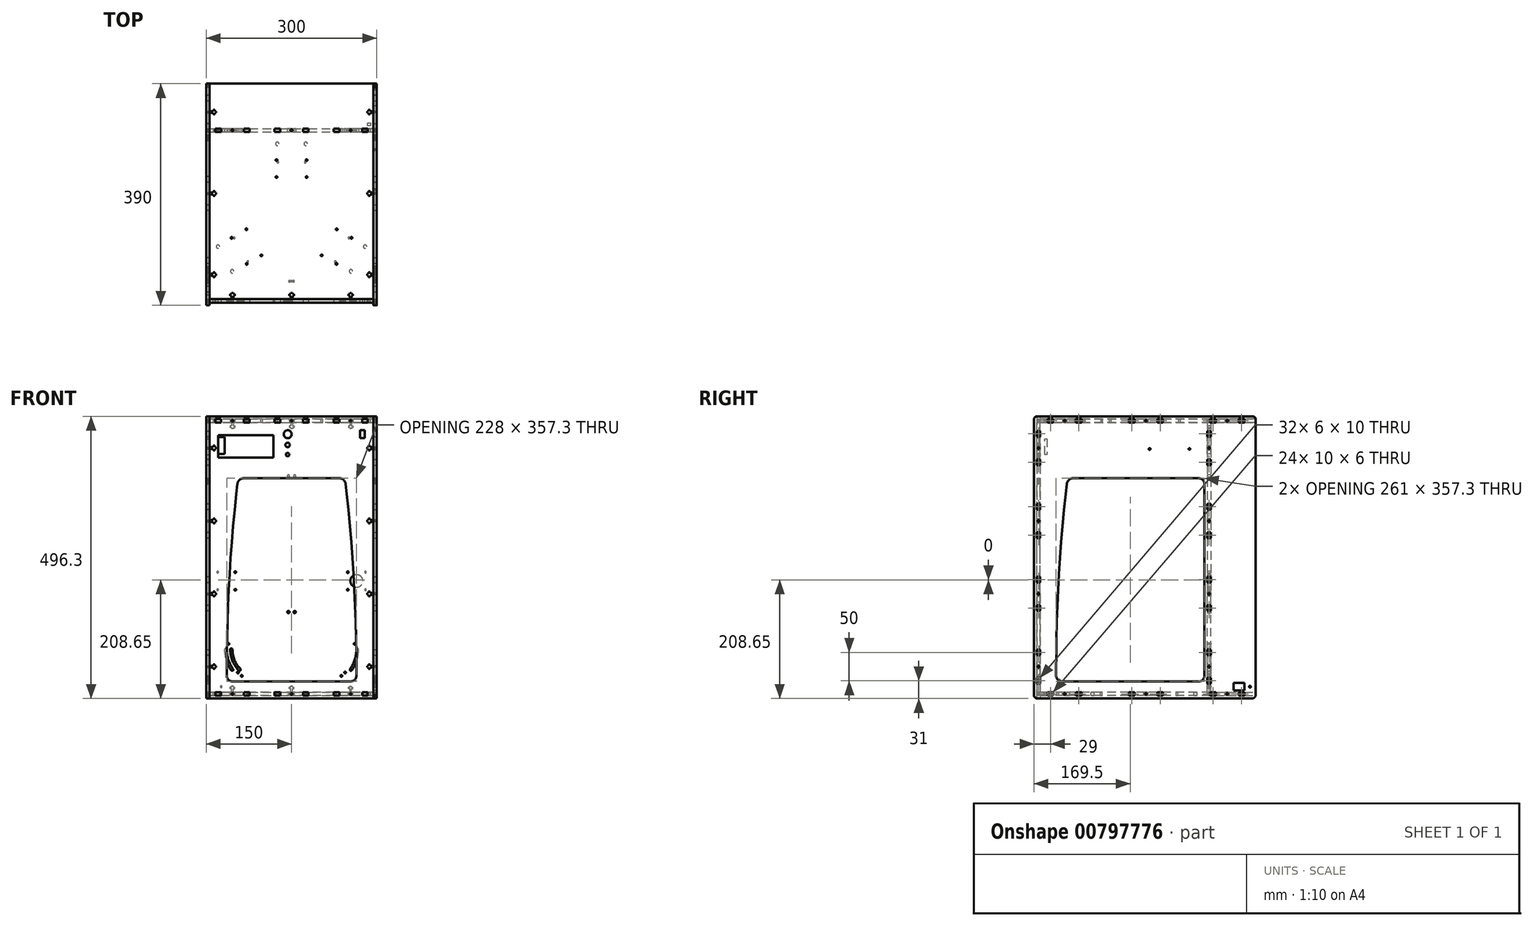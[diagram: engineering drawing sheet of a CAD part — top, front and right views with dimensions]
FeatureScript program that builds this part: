
annotation { "Feature Type Name" : "Feature", "Feature Type Description" : "" }
export const myFeature = defineFeature(function(context is Context, id is Id, definition is map)
    precondition{}
    {
        {
            var Q0;
            Q0=qCreatedBy(makeId("Top.planeOp"),FACE);
            cPlane(context, id + "F0", {"entities" : qUnion([Q0]), "cplaneType" : CPlaneType.OFFSET, "offset" : 237.15 * mm, "width" : 150 * mm, "height" : 150 * mm});
        }
        {
            var Q0;
            Q0=qCreatedBy(makeId("Top.planeOp"),FACE);
            cPlane(context, id + "F1", {"entities" : qUnion([Q0]), "cplaneType" : CPlaneType.OFFSET, "offset" : 237.15 * mm, "oppositeDirection" : true, "width" : 150 * mm, "height" : 150 * mm});
        }
        {
            var Q0;
            Q0=qCreatedBy(id+"F0.planeOp",FACE);
            var sketch = newSketch(context, id + "F2", { "sketchPlane" : qUnion([Q0])});
            skLineSegment(sketch, "E0", {"start": v(-144, 159.5) * mm, "end": v(-150, 159.5) * mm});
            skLineSegment(sketch, "E1", {"start": v(84, 104.5) * mm, "end": v(74, 104.5) * mm});
            skCircle(sketch, "E2", {"center": v(-105.48, -81.65) * mm, "radius": 1.5 * mm});
            skCircle(sketch, "E3", {"center": v(-104, 107.5) * mm, "radius": 1.5 * mm});
            skLineSegment(sketch, "E4", {"start": v(-138, 141) * mm, "end": v(-138, 143.5) * mm});
            skLineSegment(sketch, "E5", {"start": v(-150, 109.5) * mm, "end": v(-150, 119.5) * mm});
            skLineSegment(sketch, "E6", {"start": v(-144, 109.5) * mm, "end": v(-150, 109.5) * mm});
            skLineSegment(sketch, "E7", {"start": v(-144, 119.5) * mm, "end": v(-150, 119.5) * mm});
            skCircle(sketch, "E8", {"center": v(0, 107.5) * mm, "radius": 1.5 * mm});
            skCircle(sketch, "E9", {"center": v(104, 107.5) * mm, "radius": 1.5 * mm});
            skLineSegment(sketch, "E10", {"start": v(-105.5, -189.5) * mm, "end": v(-124, -189.5) * mm});
            skLineSegment(sketch, "E11", {"start": v(-144, -189.5) * mm, "end": v(-144, -176.5) * mm});
            skLineSegment(sketch, "E12", {"start": v(-135, -148) * mm, "end": v(-133, -148) * mm});
            skLineSegment(sketch, "E13", {"start": v(-135, -145) * mm, "end": v(-133, -145) * mm});
            skLineSegment(sketch, "E14", {"start": v(-135, -5) * mm, "end": v(-133, -5) * mm});
            skLineSegment(sketch, "E15", {"start": v(-135, -2) * mm, "end": v(-133, -2) * mm});
            skLineSegment(sketch, "E16", {"start": v(-135, 138) * mm, "end": v(-133, 138) * mm});
            skLineSegment(sketch, "E17", {"start": v(-135, 141) * mm, "end": v(-133, 141) * mm});
            skLineSegment(sketch, "E18", {"start": v(144, 141) * mm, "end": v(138, 141) * mm});
            skLineSegment(sketch, "E19", {"start": v(144, 138) * mm, "end": v(138, 138) * mm});
            skLineSegment(sketch, "E20", {"start": v(144, -2) * mm, "end": v(138, -2) * mm});
            skLineSegment(sketch, "E21", {"start": v(144, -5) * mm, "end": v(138, -5) * mm});
            skLineSegment(sketch, "E22", {"start": v(144, -33.5) * mm, "end": v(144, -116.5) * mm});
            skLineSegment(sketch, "E23", {"start": v(144, -145) * mm, "end": v(138, -145) * mm});
            skLineSegment(sketch, "E24", {"start": v(144, -148) * mm, "end": v(138, -148) * mm});
            skLineSegment(sketch, "E25", {"start": v(-74, -189.5) * mm, "end": v(-74, -195.5) * mm});
            skLineSegment(sketch, "E26", {"start": v(102.5, -180.5) * mm, "end": v(100, -180.5) * mm});
            skLineSegment(sketch, "E27", {"start": v(102.5, -180.5) * mm, "end": v(102.5, -178.5) * mm});
            skLineSegment(sketch, "E28", {"start": v(-105.5, -183.5) * mm, "end": v(-108, -183.5) * mm});
            skLineSegment(sketch, "E29", {"start": v(144, 159.5) * mm, "end": v(144, 141) * mm});
            skLineSegment(sketch, "E30", {"start": v(135, -5) * mm, "end": v(133, -5) * mm});
            skLineSegment(sketch, "E31", {"start": v(-138, -5) * mm, "end": v(-138, -7.5) * mm});
            skLineSegment(sketch, "E32", {"start": v(134, -189.5) * mm, "end": v(134, -195.5) * mm});
            skLineSegment(sketch, "E33", {"start": v(-105.5, -180.5) * mm, "end": v(-108, -180.5) * mm});
            skLineSegment(sketch, "E34", {"start": v(-102.5, -180.5) * mm, "end": v(-100, -180.5) * mm});
            skLineSegment(sketch, "E35", {"start": v(-1.5, -189.5) * mm, "end": v(-20, -189.5) * mm});
            skLineSegment(sketch, "E36", {"start": v(134, 110.5) * mm, "end": v(134, 104.5) * mm});
            skLineSegment(sketch, "E37", {"start": v(-74, 104.5) * mm, "end": v(-74, 110.5) * mm});
            skLineSegment(sketch, "E38", {"start": v(74, 110.5) * mm, "end": v(84, 110.5) * mm});
            skLineSegment(sketch, "E39", {"start": v(144, -33.5) * mm, "end": v(150, -33.5) * mm});
            skLineSegment(sketch, "E40", {"start": v(144, 16.5) * mm, "end": v(144, -2) * mm});
            skLineSegment(sketch, "E41", {"start": v(150, 109.5) * mm, "end": v(150, 119.5) * mm});
            skLineSegment(sketch, "E42", {"start": v(135, 138) * mm, "end": v(133, 138) * mm});
            skLineSegment(sketch, "E43", {"start": v(144, -116.5) * mm, "end": v(150, -116.5) * mm});
            skLineSegment(sketch, "E44", {"start": v(144, 119.5) * mm, "end": v(150, 119.5) * mm});
            skLineSegment(sketch, "E45", {"start": v(144, -176.5) * mm, "end": v(150, -176.5) * mm});
            skLineSegment(sketch, "E46", {"start": v(138, -145) * mm, "end": v(138, -142.5) * mm});
            skLineSegment(sketch, "E47", {"start": v(144, 189.5) * mm, "end": v(144, 169.5) * mm});
            skLineSegment(sketch, "E48", {"start": v(135, -145) * mm, "end": v(135, -142.5) * mm});
            skLineSegment(sketch, "E49", {"start": v(133, -145) * mm, "end": v(133, -148) * mm});
            skLineSegment(sketch, "E50", {"start": v(135, 138) * mm, "end": v(135, 135.5) * mm});
            skLineSegment(sketch, "E51", {"start": v(138, -142.5) * mm, "end": v(135, -142.5) * mm});
            skLineSegment(sketch, "E52", {"start": v(150, -126.5) * mm, "end": v(150, -116.5) * mm});
            skLineSegment(sketch, "E53", {"start": v(138, 141) * mm, "end": v(138, 143.5) * mm});
            skLineSegment(sketch, "E54", {"start": v(144, -126.5) * mm, "end": v(144, -145) * mm});
            skLineSegment(sketch, "E55", {"start": v(144, 138) * mm, "end": v(144, 119.5) * mm});
            skLineSegment(sketch, "E56", {"start": v(150, 159.5) * mm, "end": v(150, 169.5) * mm});
            skLineSegment(sketch, "E57", {"start": v(135, -148) * mm, "end": v(133, -148) * mm});
            skLineSegment(sketch, "E58", {"start": v(135, -148) * mm, "end": v(135, -150.5) * mm});
            skLineSegment(sketch, "E59", {"start": v(138, 138) * mm, "end": v(138, 135.5) * mm});
            skLineSegment(sketch, "E60", {"start": v(144, 169.5) * mm, "end": v(150, 169.5) * mm});
            skLineSegment(sketch, "E61", {"start": v(144, 109.5) * mm, "end": v(144, 26.5) * mm});
            skLineSegment(sketch, "E62", {"start": v(138, -148) * mm, "end": v(138, -150.5) * mm});
            skLineSegment(sketch, "E63", {"start": v(-133, -2) * mm, "end": v(-133, -5) * mm});
            skLineSegment(sketch, "E64", {"start": v(144, -176.5) * mm, "end": v(144, -189.5) * mm});
            skLineSegment(sketch, "E65", {"start": v(144, -189.5) * mm, "end": v(134, -189.5) * mm});
            skLineSegment(sketch, "E66", {"start": v(105.5, -189.5) * mm, "end": v(105.5, -183.5) * mm});
            skLineSegment(sketch, "E67", {"start": v(105.5, -183.5) * mm, "end": v(108, -183.5) * mm});
            skLineSegment(sketch, "E68", {"start": v(108, -183.5) * mm, "end": v(108, -180.5) * mm});
            skLineSegment(sketch, "E69", {"start": v(100, -183.5) * mm, "end": v(100, -180.5) * mm});
            skLineSegment(sketch, "E70", {"start": v(102.5, -183.5) * mm, "end": v(100, -183.5) * mm});
            skLineSegment(sketch, "E71", {"start": v(102.5, -189.5) * mm, "end": v(102.5, -183.5) * mm});
            skLineSegment(sketch, "E72", {"start": v(74, -189.5) * mm, "end": v(30, -189.5) * mm});
            skLineSegment(sketch, "E73", {"start": v(-134, -189.5) * mm, "end": v(-144, -189.5) * mm});
            skLineSegment(sketch, "E74", {"start": v(-84, -189.5) * mm, "end": v(-102.5, -189.5) * mm});
            skLineSegment(sketch, "E75", {"start": v(124, -195.5) * mm, "end": v(134, -195.5) * mm});
            skLineSegment(sketch, "E76", {"start": v(-102.5, -180.5) * mm, "end": v(-102.5, -178.5) * mm});
            skLineSegment(sketch, "E77", {"start": v(-144, -5) * mm, "end": v(-138, -5) * mm});
            skLineSegment(sketch, "E78", {"start": v(-150, -166.5) * mm, "end": v(-150, -176.5) * mm});
            skLineSegment(sketch, "E79", {"start": v(-144, -166.5) * mm, "end": v(-144, -148) * mm});
            skLineSegment(sketch, "E80", {"start": v(-138, 135.5) * mm, "end": v(-135, 135.5) * mm});
            skLineSegment(sketch, "E81", {"start": v(-144, -148) * mm, "end": v(-138, -148) * mm});
            skLineSegment(sketch, "E82", {"start": v(-144, -2) * mm, "end": v(-144, 16.5) * mm});
            skLineSegment(sketch, "E83", {"start": v(-150, 26.5) * mm, "end": v(-150, 16.5) * mm});
            skLineSegment(sketch, "E84", {"start": v(135, -145) * mm, "end": v(133, -145) * mm});
            skLineSegment(sketch, "E85", {"start": v(-135, -2) * mm, "end": v(-135, 0.5) * mm});
            skLineSegment(sketch, "E86", {"start": v(-144, -23.5) * mm, "end": v(-144, -5) * mm});
            skLineSegment(sketch, "E87", {"start": v(-150, -116.5) * mm, "end": v(-150, -126.5) * mm});
            skLineSegment(sketch, "E88", {"start": v(144, 26.5) * mm, "end": v(150, 26.5) * mm});
            skLineSegment(sketch, "E89", {"start": v(-138, -148) * mm, "end": v(-138, -150.5) * mm});
            skLineSegment(sketch, "E90", {"start": v(-133, 138) * mm, "end": v(-133, 141) * mm});
            skLineSegment(sketch, "E91", {"start": v(144, 16.5) * mm, "end": v(150, 16.5) * mm});
            skLineSegment(sketch, "E92", {"start": v(-102.5, -178.5) * mm, "end": v(-105.5, -178.5) * mm});
            skLineSegment(sketch, "E93", {"start": v(-102.5, -183.5) * mm, "end": v(-100, -183.5) * mm});
            skLineSegment(sketch, "E94", {"start": v(105.5, -178.5) * mm, "end": v(102.5, -178.5) * mm});
            skLineSegment(sketch, "E95", {"start": v(84, -189.5) * mm, "end": v(84, -195.5) * mm});
            skLineSegment(sketch, "E96", {"start": v(105.5, -180.5) * mm, "end": v(105.5, -178.5) * mm});
            skLineSegment(sketch, "E97", {"start": v(135, 141) * mm, "end": v(135, 143.5) * mm});
            skLineSegment(sketch, "E98", {"start": v(144, 109.5) * mm, "end": v(150, 109.5) * mm});
            skLineSegment(sketch, "E99", {"start": v(150, -176.5) * mm, "end": v(150, -166.5) * mm});
            skLineSegment(sketch, "E100", {"start": v(144, -166.5) * mm, "end": v(150, -166.5) * mm});
            skLineSegment(sketch, "E101", {"start": v(144, 159.5) * mm, "end": v(150, 159.5) * mm});
            skLineSegment(sketch, "E102", {"start": v(138, 143.5) * mm, "end": v(135, 143.5) * mm});
            skLineSegment(sketch, "E103", {"start": v(135, 141) * mm, "end": v(133, 141) * mm});
            skLineSegment(sketch, "E104", {"start": v(-133, -148) * mm, "end": v(-133, -145) * mm});
            skLineSegment(sketch, "E105", {"start": v(144, -148) * mm, "end": v(144, -166.5) * mm});
            skLineSegment(sketch, "E106", {"start": v(144, -126.5) * mm, "end": v(150, -126.5) * mm});
            skLineSegment(sketch, "E107", {"start": v(-144, -145) * mm, "end": v(-144, -126.5) * mm});
            skLineSegment(sketch, "E108", {"start": v(-144, -145) * mm, "end": v(-138, -145) * mm});
            skLineSegment(sketch, "E109", {"start": v(150, -33.5) * mm, "end": v(150, -23.5) * mm});
            skLineSegment(sketch, "E110", {"start": v(-135, 141) * mm, "end": v(-135, 143.5) * mm});
            skLineSegment(sketch, "E111", {"start": v(-144, 169.5) * mm, "end": v(-150, 169.5) * mm});
            skLineSegment(sketch, "E112", {"start": v(-144, 141) * mm, "end": v(-138, 141) * mm});
            skLineSegment(sketch, "E113", {"start": v(-20, 104.5) * mm, "end": v(-30, 104.5) * mm});
            skLineSegment(sketch, "E114", {"start": v(-84, 104.5) * mm, "end": v(-74, 104.5) * mm});
            skLineSegment(sketch, "E115", {"start": v(-134, 104.5) * mm, "end": v(-134, 110.5) * mm});
            skLineSegment(sketch, "E116", {"start": v(30, 110.5) * mm, "end": v(30, 104.5) * mm});
            skLineSegment(sketch, "E117", {"start": v(-135, -145) * mm, "end": v(-135, -142.5) * mm});
            skLineSegment(sketch, "E118", {"start": v(-138, -142.5) * mm, "end": v(-135, -142.5) * mm});
            skLineSegment(sketch, "E119", {"start": v(-134, 110.5) * mm, "end": v(-124, 110.5) * mm});
            skLineSegment(sketch, "E120", {"start": v(144, -23.5) * mm, "end": v(150, -23.5) * mm});
            skLineSegment(sketch, "E121", {"start": v(-138, -7.5) * mm, "end": v(-135, -7.5) * mm});
            skLineSegment(sketch, "E122", {"start": v(-144, -116.5) * mm, "end": v(-150, -116.5) * mm});
            skLineSegment(sketch, "E123", {"start": v(-135, -5) * mm, "end": v(-135, -7.5) * mm});
            skLineSegment(sketch, "E124", {"start": v(-144, -116.5) * mm, "end": v(-144, -33.5) * mm});
            skLineSegment(sketch, "E125", {"start": v(-150, -23.5) * mm, "end": v(-150, -33.5) * mm});
            skLineSegment(sketch, "E126", {"start": v(-124, -195.5) * mm, "end": v(-124, -189.5) * mm});
            skLineSegment(sketch, "E127", {"start": v(-84, -195.5) * mm, "end": v(-74, -195.5) * mm});
            skLineSegment(sketch, "E128", {"start": v(102.5, -189.5) * mm, "end": v(84, -189.5) * mm});
            skLineSegment(sketch, "E129", {"start": v(124, -189.5) * mm, "end": v(105.5, -189.5) * mm});
            skLineSegment(sketch, "E130", {"start": v(-105.5, -180.5) * mm, "end": v(-105.5, -178.5) * mm});
            skLineSegment(sketch, "E131", {"start": v(133, 141) * mm, "end": v(133, 138) * mm});
            skLineSegment(sketch, "E132", {"start": v(138, 135.5) * mm, "end": v(135, 135.5) * mm});
            skLineSegment(sketch, "E133", {"start": v(-1.5, -189.5) * mm, "end": v(-1.5, -183.5) * mm});
            skLineSegment(sketch, "E134", {"start": v(4, -183.5) * mm, "end": v(4, -180.5) * mm});
            skLineSegment(sketch, "E135", {"start": v(-1.5, -183.5) * mm, "end": v(-4, -183.5) * mm});
            skLineSegment(sketch, "E136", {"start": v(20, -189.5) * mm, "end": v(20, -195.5) * mm});
            skLineSegment(sketch, "E137", {"start": v(1.5, -178.5) * mm, "end": v(-1.5, -178.5) * mm});
            skLineSegment(sketch, "E138", {"start": v(-30, -195.5) * mm, "end": v(-20, -195.5) * mm});
            skLineSegment(sketch, "E139", {"start": v(-1.5, -180.5) * mm, "end": v(-1.5, -178.5) * mm});
            skLineSegment(sketch, "E140", {"start": v(1.5, -189.5) * mm, "end": v(1.5, -183.5) * mm});
            skLineSegment(sketch, "E141", {"start": v(30, -189.5) * mm, "end": v(30, -195.5) * mm});
            skLineSegment(sketch, "E142", {"start": v(1.5, -180.5) * mm, "end": v(1.5, -178.5) * mm});
            skLineSegment(sketch, "E143", {"start": v(1.5, -180.5) * mm, "end": v(4, -180.5) * mm});
            skLineSegment(sketch, "E144", {"start": v(20, -195.5) * mm, "end": v(30, -195.5) * mm});
            skLineSegment(sketch, "E145", {"start": v(-4, -183.5) * mm, "end": v(-4, -180.5) * mm});
            skLineSegment(sketch, "E146", {"start": v(-20, -189.5) * mm, "end": v(-20, -195.5) * mm});
            skLineSegment(sketch, "E147", {"start": v(138, -2) * mm, "end": v(138, 0.5) * mm});
            skLineSegment(sketch, "E148", {"start": v(-144, 119.5) * mm, "end": v(-144, 138) * mm});
            skLineSegment(sketch, "E149", {"start": v(-144, 26.5) * mm, "end": v(-144, 109.5) * mm});
            skLineSegment(sketch, "E150", {"start": v(-138, 138) * mm, "end": v(-138, 135.5) * mm});
            skLineSegment(sketch, "E151", {"start": v(-138, -150.5) * mm, "end": v(-135, -150.5) * mm});
            skLineSegment(sketch, "E152", {"start": v(135, -5) * mm, "end": v(135, -7.5) * mm});
            skLineSegment(sketch, "E153", {"start": v(-144, -126.5) * mm, "end": v(-150, -126.5) * mm});
            skLineSegment(sketch, "E154", {"start": v(-30, -189.5) * mm, "end": v(-30, -195.5) * mm});
            skLineSegment(sketch, "E155", {"start": v(138, -150.5) * mm, "end": v(135, -150.5) * mm});
            skLineSegment(sketch, "E156", {"start": v(-138, 0.5) * mm, "end": v(-135, 0.5) * mm});
            skLineSegment(sketch, "E157", {"start": v(-102.5, -189.5) * mm, "end": v(-102.5, -183.5) * mm});
            skLineSegment(sketch, "E158", {"start": v(74, -195.5) * mm, "end": v(84, -195.5) * mm});
            skLineSegment(sketch, "E159", {"start": v(-100, -183.5) * mm, "end": v(-100, -180.5) * mm});
            skLineSegment(sketch, "E160", {"start": v(-150, 169.5) * mm, "end": v(-150, 159.5) * mm});
            skLineSegment(sketch, "E161", {"start": v(-135, 138) * mm, "end": v(-135, 135.5) * mm});
            skLineSegment(sketch, "E162", {"start": v(-144, 141) * mm, "end": v(-144, 159.5) * mm});
            skLineSegment(sketch, "E163", {"start": v(-144, 26.5) * mm, "end": v(-150, 26.5) * mm});
            skLineSegment(sketch, "E164", {"start": v(135, -2) * mm, "end": v(133, -2) * mm});
            skLineSegment(sketch, "E165", {"start": v(-144, 169.5) * mm, "end": v(-144, 189.5) * mm});
            skLineSegment(sketch, "E166", {"start": v(-144, 16.5) * mm, "end": v(-150, 16.5) * mm});
            skLineSegment(sketch, "E167", {"start": v(-135, -148) * mm, "end": v(-135, -150.5) * mm});
            skLineSegment(sketch, "E168", {"start": v(-138, -145) * mm, "end": v(-138, -142.5) * mm});
            skLineSegment(sketch, "E169", {"start": v(138, 0.5) * mm, "end": v(135, 0.5) * mm});
            skLineSegment(sketch, "E170", {"start": v(-144, -2) * mm, "end": v(-138, -2) * mm});
            skLineSegment(sketch, "E171", {"start": v(138, -7.5) * mm, "end": v(135, -7.5) * mm});
            skLineSegment(sketch, "E172", {"start": v(-144, -176.5) * mm, "end": v(-150, -176.5) * mm});
            skLineSegment(sketch, "E173", {"start": v(133, -2) * mm, "end": v(133, -5) * mm});
            skLineSegment(sketch, "E174", {"start": v(-134, -189.5) * mm, "end": v(-134, -195.5) * mm});
            skLineSegment(sketch, "E175", {"start": v(-144, 189.5) * mm, "end": v(144, 189.5) * mm});
            skLineSegment(sketch, "E176", {"start": v(-124, 110.5) * mm, "end": v(-124, 104.5) * mm});
            skLineSegment(sketch, "E177", {"start": v(-30, 110.5) * mm, "end": v(-20, 110.5) * mm});
            skLineSegment(sketch, "E178", {"start": v(20, 104.5) * mm, "end": v(30, 104.5) * mm});
            skLineSegment(sketch, "E179", {"start": v(74, 104.5) * mm, "end": v(74, 110.5) * mm});
            skLineSegment(sketch, "E180", {"start": v(134, 104.5) * mm, "end": v(124, 104.5) * mm});
            skLineSegment(sketch, "E181", {"start": v(-20, 110.5) * mm, "end": v(-20, 104.5) * mm});
            skLineSegment(sketch, "E182", {"start": v(-30, 104.5) * mm, "end": v(-30, 110.5) * mm});
            skLineSegment(sketch, "E183", {"start": v(-84, 110.5) * mm, "end": v(-84, 104.5) * mm});
            skLineSegment(sketch, "E184", {"start": v(-138, 143.5) * mm, "end": v(-135, 143.5) * mm});
            skLineSegment(sketch, "E185", {"start": v(-144, 138) * mm, "end": v(-138, 138) * mm});
            skLineSegment(sketch, "E186", {"start": v(144, -5) * mm, "end": v(144, -23.5) * mm});
            skLineSegment(sketch, "E187", {"start": v(-144, -166.5) * mm, "end": v(-150, -166.5) * mm});
            skLineSegment(sketch, "E188", {"start": v(138, -5) * mm, "end": v(138, -7.5) * mm});
            skLineSegment(sketch, "E189", {"start": v(135, -2) * mm, "end": v(135, 0.5) * mm});
            skLineSegment(sketch, "E190", {"start": v(-144, -23.5) * mm, "end": v(-150, -23.5) * mm});
            skLineSegment(sketch, "E191", {"start": v(150, 16.5) * mm, "end": v(150, 26.5) * mm});
            skLineSegment(sketch, "E192", {"start": v(-144, -33.5) * mm, "end": v(-150, -33.5) * mm});
            skLineSegment(sketch, "E193", {"start": v(-84, -189.5) * mm, "end": v(-84, -195.5) * mm});
            skLineSegment(sketch, "E194", {"start": v(74, -189.5) * mm, "end": v(74, -195.5) * mm});
            skLineSegment(sketch, "E195", {"start": v(105.5, -180.5) * mm, "end": v(108, -180.5) * mm});
            skLineSegment(sketch, "E196", {"start": v(-108, -183.5) * mm, "end": v(-108, -180.5) * mm});
            skLineSegment(sketch, "E197", {"start": v(124, -189.5) * mm, "end": v(124, -195.5) * mm});
            skLineSegment(sketch, "E198", {"start": v(-124, -195.5) * mm, "end": v(-134, -195.5) * mm});
            skLineSegment(sketch, "E199", {"start": v(-105.5, -189.5) * mm, "end": v(-105.5, -183.5) * mm});
            skLineSegment(sketch, "E200", {"start": v(20, 104.5) * mm, "end": v(20, 110.5) * mm});
            skLineSegment(sketch, "E201", {"start": v(20, 110.5) * mm, "end": v(30, 110.5) * mm});
            skLineSegment(sketch, "E202", {"start": v(-124, 104.5) * mm, "end": v(-134, 104.5) * mm});
            skLineSegment(sketch, "E203", {"start": v(124, 110.5) * mm, "end": v(134, 110.5) * mm});
            skLineSegment(sketch, "E204", {"start": v(84, 110.5) * mm, "end": v(84, 104.5) * mm});
            skLineSegment(sketch, "E205", {"start": v(-138, -2) * mm, "end": v(-138, 0.5) * mm});
            skLineSegment(sketch, "E206", {"start": v(1.5, -183.5) * mm, "end": v(4, -183.5) * mm});
            skLineSegment(sketch, "E207", {"start": v(-1.5, -180.5) * mm, "end": v(-4, -180.5) * mm});
            skLineSegment(sketch, "E208", {"start": v(20, -189.5) * mm, "end": v(1.5, -189.5) * mm});
            skLineSegment(sketch, "E209", {"start": v(-30, -189.5) * mm, "end": v(-74, -189.5) * mm});
            skLineSegment(sketch, "E210", {"start": v(124, 104.5) * mm, "end": v(124, 110.5) * mm});
            skLineSegment(sketch, "E211", {"start": v(-74, 110.5) * mm, "end": v(-84, 110.5) * mm});
            skCircle(sketch, "E212", {"center": v(-79.5, -66.65) * mm, "radius": 1.5 * mm});
            skCircle(sketch, "E213", {"center": v(-26.5, 55.15) * mm, "radius": 1.5 * mm});
            skCircle(sketch, "E214", {"center": v(-78.98, -127.55) * mm, "radius": 1.5 * mm});
            skCircle(sketch, "E215", {"center": v(-53, -112.55) * mm, "radius": 1.5 * mm});
            skCircle(sketch, "E216", {"center": v(-26.5, 25.15) * mm, "radius": 1.5 * mm});
            skCircle(sketch, "E217", {"center": v(26.5, 55.15) * mm, "radius": 1.5 * mm});
            skCircle(sketch, "E218", {"center": v(26.5, 25.15) * mm, "radius": 1.5 * mm});
            skCircle(sketch, "E219", {"center": v(105.48, -81.65) * mm, "radius": 1.5 * mm});
            skCircle(sketch, "E220", {"center": v(79.5, -66.65) * mm, "radius": 1.5 * mm});
            skCircle(sketch, "E221", {"center": v(53, -112.55) * mm, "radius": 1.5 * mm});
            skCircle(sketch, "E222", {"center": v(78.98, -127.55) * mm, "radius": 1.5 * mm});
            skLineSegment(sketch, "E223", {"start": v(0, 189.5) * mm, "end": v(0, -189.5) * mm, "construction": true});
            skSolve(sketch);
        }
        {
            var Q0;
            Q0 = qSketchRegion(id + "F2", true);
            extrude(context, id + "F3", {"entities" : qUnion([Q0]), "depth" : 6 * mm, "offsetDistance" : 25 * mm});
        }
        {
            var Q0;
            Q0=qCreatedBy(id+"F1.planeOp",FACE);
            var sketch = newSketch(context, id + "F4", { "sketchPlane" : qUnion([Q0])});
            skCircle(sketch, "E224", {"center": v(-129.41, -97.2) * mm, "radius": 3 * mm});
            skCircle(sketch, "E225", {"center": v(104.41, -140.5) * mm, "radius": 3 * mm});
            skLineSegment(sketch, "E226", {"start": v(134, -189.5) * mm, "end": v(144, -189.5) * mm});
            skCircle(sketch, "E227", {"center": v(0, 107.5) * mm, "radius": 1.5 * mm});
            skCircle(sketch, "E228", {"center": v(104, 107.5) * mm, "radius": 1.5 * mm});
            skCircle(sketch, "E229", {"center": v(-104.41, -140.5) * mm, "radius": 3 * mm});
            skLineSegment(sketch, "E230", {"start": v(84, 104.5) * mm, "end": v(74, 104.5) * mm});
            skLineSegment(sketch, "E231", {"start": v(84, 110.5) * mm, "end": v(84, 104.5) * mm});
            skLineSegment(sketch, "E232", {"start": v(124, 104.5) * mm, "end": v(134, 104.5) * mm});
            skLineSegment(sketch, "E233", {"start": v(-134, 104.5) * mm, "end": v(-124, 104.5) * mm});
            skLineSegment(sketch, "E234", {"start": v(-134, 110.5) * mm, "end": v(-134, 104.5) * mm});
            skLineSegment(sketch, "E235", {"start": v(134, 104.5) * mm, "end": v(134, 110.5) * mm});
            skLineSegment(sketch, "E236", {"start": v(-20, 104.5) * mm, "end": v(-20, 110.5) * mm});
            skLineSegment(sketch, "E237", {"start": v(-20, 110.5) * mm, "end": v(-30, 110.5) * mm});
            skLineSegment(sketch, "E238", {"start": v(74, 104.5) * mm, "end": v(74, 110.5) * mm});
            skLineSegment(sketch, "E239", {"start": v(-30, 110.5) * mm, "end": v(-30, 104.5) * mm});
            skLineSegment(sketch, "E240", {"start": v(134, 110.5) * mm, "end": v(124, 110.5) * mm});
            skLineSegment(sketch, "E241", {"start": v(124, 110.5) * mm, "end": v(124, 104.5) * mm});
            skLineSegment(sketch, "E242", {"start": v(74, 110.5) * mm, "end": v(84, 110.5) * mm});
            skLineSegment(sketch, "E243", {"start": v(-84, 110.5) * mm, "end": v(-84, 104.5) * mm});
            skLineSegment(sketch, "E244", {"start": v(-30, 104.5) * mm, "end": v(-20, 104.5) * mm});
            skLineSegment(sketch, "E245", {"start": v(-74, 110.5) * mm, "end": v(-84, 110.5) * mm});
            skLineSegment(sketch, "E246", {"start": v(-84, 104.5) * mm, "end": v(-74, 104.5) * mm});
            skLineSegment(sketch, "E247", {"start": v(-74, 104.5) * mm, "end": v(-74, 110.5) * mm});
            skLineSegment(sketch, "E248", {"start": v(-124, 104.5) * mm, "end": v(-124, 110.5) * mm});
            skCircle(sketch, "E249", {"center": v(129.41, -97.2) * mm, "radius": 3 * mm});
            skCircle(sketch, "E250", {"center": v(25, 83.65) * mm, "radius": 3 * mm});
            skLineSegment(sketch, "E251", {"start": v(-3.53, -156.55) * mm, "end": v(3.47, -156.55) * mm});
            skCircle(sketch, "E252", {"center": v(-25, 83.65) * mm, "radius": 3 * mm});
            skCircle(sketch, "E253", {"center": v(-104, 107.5) * mm, "radius": 1.5 * mm});
            skLineSegment(sketch, "E254", {"start": v(144, 189.5) * mm, "end": v(-144, 189.5) * mm});
            skArc(sketch, "E255", {"start": v(-3.53, -156.55) * mm, "mid": v(-5.03, -158.05) * mm, "end": v(-3.53, -159.55) * mm});
            skLineSegment(sketch, "E256", {"start": v(30, 104.5) * mm, "end": v(30, 110.5) * mm});
            skLineSegment(sketch, "E257", {"start": v(30, 110.5) * mm, "end": v(20, 110.5) * mm});
            skLineSegment(sketch, "E258", {"start": v(20, 104.5) * mm, "end": v(20, 110.5) * mm});
            skLineSegment(sketch, "E259", {"start": v(30, 104.5) * mm, "end": v(20, 104.5) * mm});
            skLineSegment(sketch, "E260", {"start": v(3.47, -159.55) * mm, "end": v(-3.53, -159.55) * mm});
            skLineSegment(sketch, "E261", {"start": v(144, 16.5) * mm, "end": v(150, 16.5) * mm});
            skLineSegment(sketch, "E262", {"start": v(144, 26.5) * mm, "end": v(150, 26.5) * mm});
            skLineSegment(sketch, "E263", {"start": v(144, -126.5) * mm, "end": v(150, -126.5) * mm});
            skLineSegment(sketch, "E264", {"start": v(144, -145) * mm, "end": v(138, -145) * mm});
            skLineSegment(sketch, "E265", {"start": v(138, -150.5) * mm, "end": v(135, -150.5) * mm});
            skLineSegment(sketch, "E266", {"start": v(135, -148) * mm, "end": v(133, -148) * mm});
            skLineSegment(sketch, "E267", {"start": v(138, -145) * mm, "end": v(138, -142.5) * mm});
            skLineSegment(sketch, "E268", {"start": v(138, -142.5) * mm, "end": v(135, -142.5) * mm});
            skLineSegment(sketch, "E269", {"start": v(150, -176.5) * mm, "end": v(150, -166.5) * mm});
            skLineSegment(sketch, "E270", {"start": v(144, -166.5) * mm, "end": v(150, -166.5) * mm});
            skLineSegment(sketch, "E271", {"start": v(135, -145) * mm, "end": v(133, -145) * mm});
            skLineSegment(sketch, "E272", {"start": v(144, -116.5) * mm, "end": v(150, -116.5) * mm});
            skLineSegment(sketch, "E273", {"start": v(138, -148) * mm, "end": v(138, -150.5) * mm});
            skLineSegment(sketch, "E274", {"start": v(144, -176.5) * mm, "end": v(150, -176.5) * mm});
            skArc(sketch, "E275", {"start": v(3.47, -159.55) * mm, "mid": v(4.97, -158.05) * mm, "end": v(3.47, -156.55) * mm});
            skLineSegment(sketch, "E276", {"start": v(134, 120.5) * mm, "end": v(139, 120.5) * mm});
            skLineSegment(sketch, "E277", {"start": v(134, 115.5) * mm, "end": v(134, 120.5) * mm});
            skLineSegment(sketch, "E278", {"start": v(139, 115.5) * mm, "end": v(134, 115.5) * mm});
            skLineSegment(sketch, "E279", {"start": v(139, 120.5) * mm, "end": v(139, 115.5) * mm});
            skLineSegment(sketch, "E280", {"start": v(-133, 141) * mm, "end": v(-133, 138) * mm});
            skLineSegment(sketch, "E281", {"start": v(-138, 141) * mm, "end": v(-138, 143.5) * mm});
            skLineSegment(sketch, "E282", {"start": v(-138, 138) * mm, "end": v(-138, 135.5) * mm});
            skLineSegment(sketch, "E283", {"start": v(-135, 141) * mm, "end": v(-135, 143.5) * mm});
            skLineSegment(sketch, "E284", {"start": v(-135, 141) * mm, "end": v(-133, 141) * mm});
            skLineSegment(sketch, "E285", {"start": v(-150, 169.5) * mm, "end": v(-150, 159.5) * mm});
            skLineSegment(sketch, "E286", {"start": v(-144, 109.5) * mm, "end": v(-150, 109.5) * mm});
            skLineSegment(sketch, "E287", {"start": v(-144, 169.5) * mm, "end": v(-144, 189.5) * mm});
            skLineSegment(sketch, "E288", {"start": v(-144, 138) * mm, "end": v(-138, 138) * mm});
            skLineSegment(sketch, "E289", {"start": v(-144, 141) * mm, "end": v(-138, 141) * mm});
            skLineSegment(sketch, "E290", {"start": v(-138, 143.5) * mm, "end": v(-135, 143.5) * mm});
            skLineSegment(sketch, "E291", {"start": v(-144, 169.5) * mm, "end": v(-150, 169.5) * mm});
            skLineSegment(sketch, "E292", {"start": v(-135, 138) * mm, "end": v(-135, 135.5) * mm});
            skLineSegment(sketch, "E293", {"start": v(-124, 110.5) * mm, "end": v(-134, 110.5) * mm});
            skLineSegment(sketch, "E294", {"start": v(102.5, -189.5) * mm, "end": v(102.5, -183.5) * mm});
            skLineSegment(sketch, "E295", {"start": v(124, -189.5) * mm, "end": v(124, -195.5) * mm});
            skLineSegment(sketch, "E296", {"start": v(105.5, -180.5) * mm, "end": v(108, -180.5) * mm});
            skLineSegment(sketch, "E297", {"start": v(124, -195.5) * mm, "end": v(134, -195.5) * mm});
            skLineSegment(sketch, "E298", {"start": v(105.5, -183.5) * mm, "end": v(108, -183.5) * mm});
            skLineSegment(sketch, "E299", {"start": v(84, -189.5) * mm, "end": v(84, -195.5) * mm});
            skLineSegment(sketch, "E300", {"start": v(134, -189.5) * mm, "end": v(134, -195.5) * mm});
            skLineSegment(sketch, "E301", {"start": v(105.5, -189.5) * mm, "end": v(105.5, -183.5) * mm});
            skLineSegment(sketch, "E302", {"start": v(105.5, -189.5) * mm, "end": v(124, -189.5) * mm});
            skLineSegment(sketch, "E303", {"start": v(108, -183.5) * mm, "end": v(108, -180.5) * mm});
            skLineSegment(sketch, "E304", {"start": v(84, -189.5) * mm, "end": v(102.5, -189.5) * mm});
            skLineSegment(sketch, "E305", {"start": v(74, -189.5) * mm, "end": v(74, -195.5) * mm});
            skLineSegment(sketch, "E306", {"start": v(105.5, -180.5) * mm, "end": v(105.5, -178.5) * mm});
            skLineSegment(sketch, "E307", {"start": v(102.5, -180.5) * mm, "end": v(102.5, -178.5) * mm});
            skLineSegment(sketch, "E308", {"start": v(105.5, -178.5) * mm, "end": v(102.5, -178.5) * mm});
            skLineSegment(sketch, "E309", {"start": v(102.5, -183.5) * mm, "end": v(100, -183.5) * mm});
            skLineSegment(sketch, "E310", {"start": v(-74, -189.5) * mm, "end": v(-30, -189.5) * mm});
            skLineSegment(sketch, "E311", {"start": v(-20, -189.5) * mm, "end": v(-20, -195.5) * mm});
            skLineSegment(sketch, "E312", {"start": v(30, -189.5) * mm, "end": v(30, -195.5) * mm});
            skLineSegment(sketch, "E313", {"start": v(-20, -189.5) * mm, "end": v(-1.5, -189.5) * mm});
            skLineSegment(sketch, "E314", {"start": v(144, 109.5) * mm, "end": v(144, 26.5) * mm});
            skLineSegment(sketch, "E315", {"start": v(144, 119.5) * mm, "end": v(144, 138) * mm});
            skLineSegment(sketch, "E316", {"start": v(144, 169.5) * mm, "end": v(144, 189.5) * mm});
            skLineSegment(sketch, "E317", {"start": v(144, 159.5) * mm, "end": v(150, 159.5) * mm});
            skLineSegment(sketch, "E318", {"start": v(144, 138) * mm, "end": v(138, 138) * mm});
            skLineSegment(sketch, "E319", {"start": v(138, 135.5) * mm, "end": v(135, 135.5) * mm});
            skLineSegment(sketch, "E320", {"start": v(135, 138) * mm, "end": v(135, 135.5) * mm});
            skLineSegment(sketch, "E321", {"start": v(144, 109.5) * mm, "end": v(150, 109.5) * mm});
            skLineSegment(sketch, "E322", {"start": v(144, 169.5) * mm, "end": v(150, 169.5) * mm});
            skLineSegment(sketch, "E323", {"start": v(135, 141) * mm, "end": v(135, 143.5) * mm});
            skLineSegment(sketch, "E324", {"start": v(133, 141) * mm, "end": v(133, 138) * mm});
            skLineSegment(sketch, "E325", {"start": v(150, 109.5) * mm, "end": v(150, 119.5) * mm});
            skLineSegment(sketch, "E326", {"start": v(135, 138) * mm, "end": v(133, 138) * mm});
            skLineSegment(sketch, "E327", {"start": v(138, 143.5) * mm, "end": v(135, 143.5) * mm});
            skLineSegment(sketch, "E328", {"start": v(138, 141) * mm, "end": v(138, 143.5) * mm});
            skLineSegment(sketch, "E329", {"start": v(150, 159.5) * mm, "end": v(150, 169.5) * mm});
            skLineSegment(sketch, "E330", {"start": v(144, 119.5) * mm, "end": v(150, 119.5) * mm});
            skLineSegment(sketch, "E331", {"start": v(144, 141) * mm, "end": v(138, 141) * mm});
            skLineSegment(sketch, "E332", {"start": v(135, 141) * mm, "end": v(133, 141) * mm});
            skLineSegment(sketch, "E333", {"start": v(138, 138) * mm, "end": v(138, 135.5) * mm});
            skLineSegment(sketch, "E334", {"start": v(144, 141) * mm, "end": v(144, 159.5) * mm});
            skLineSegment(sketch, "E335", {"start": v(-138, 135.5) * mm, "end": v(-135, 135.5) * mm});
            skLineSegment(sketch, "E336", {"start": v(-150, 119.5) * mm, "end": v(-150, 109.5) * mm});
            skLineSegment(sketch, "E337", {"start": v(-144, 159.5) * mm, "end": v(-150, 159.5) * mm});
            skLineSegment(sketch, "E338", {"start": v(-144, 119.5) * mm, "end": v(-144, 138) * mm});
            skLineSegment(sketch, "E339", {"start": v(-144, 119.5) * mm, "end": v(-150, 119.5) * mm});
            skLineSegment(sketch, "E340", {"start": v(-135, 138) * mm, "end": v(-133, 138) * mm});
            skLineSegment(sketch, "E341", {"start": v(-144, 141) * mm, "end": v(-144, 159.5) * mm});
            skLineSegment(sketch, "E342", {"start": v(-144, 109.5) * mm, "end": v(-144, 26.5) * mm});
            skLineSegment(sketch, "E343", {"start": v(-144, -189.5) * mm, "end": v(-134, -189.5) * mm});
            skLineSegment(sketch, "E344", {"start": v(-144, -176.5) * mm, "end": v(-144, -189.5) * mm});
            skLineSegment(sketch, "E345", {"start": v(144, -33.5) * mm, "end": v(144, -116.5) * mm});
            skLineSegment(sketch, "E346", {"start": v(144, -5) * mm, "end": v(138, -5) * mm});
            skLineSegment(sketch, "E347", {"start": v(133, -2) * mm, "end": v(133, -5) * mm});
            skLineSegment(sketch, "E348", {"start": v(144, -5) * mm, "end": v(144, -23.5) * mm});
            skLineSegment(sketch, "E349", {"start": v(138, -5) * mm, "end": v(138, -7.5) * mm});
            skLineSegment(sketch, "E350", {"start": v(135, -2) * mm, "end": v(135, 0.5) * mm});
            skLineSegment(sketch, "E351", {"start": v(138, 0.5) * mm, "end": v(135, 0.5) * mm});
            skLineSegment(sketch, "E352", {"start": v(144, -23.5) * mm, "end": v(150, -23.5) * mm});
            skLineSegment(sketch, "E353", {"start": v(138, -7.5) * mm, "end": v(135, -7.5) * mm});
            skLineSegment(sketch, "E354", {"start": v(135, -5) * mm, "end": v(135, -7.5) * mm});
            skLineSegment(sketch, "E355", {"start": v(144, 16.5) * mm, "end": v(144, -2) * mm});
            skLineSegment(sketch, "E356", {"start": v(135, -5) * mm, "end": v(133, -5) * mm});
            skLineSegment(sketch, "E357", {"start": v(144, -33.5) * mm, "end": v(150, -33.5) * mm});
            skLineSegment(sketch, "E358", {"start": v(138, -2) * mm, "end": v(138, 0.5) * mm});
            skLineSegment(sketch, "E359", {"start": v(150, -33.5) * mm, "end": v(150, -23.5) * mm});
            skLineSegment(sketch, "E360", {"start": v(150, 16.5) * mm, "end": v(150, 26.5) * mm});
            skLineSegment(sketch, "E361", {"start": v(135, -2) * mm, "end": v(133, -2) * mm});
            skLineSegment(sketch, "E362", {"start": v(144, -2) * mm, "end": v(138, -2) * mm});
            skCircle(sketch, "E363", {"center": v(24, 51.36) * mm, "radius": 1.5 * mm});
            skCircle(sketch, "E364", {"center": v(-24, 51.36) * mm, "radius": 1.5 * mm});
            skLineSegment(sketch, "E365", {"start": v(135, -145) * mm, "end": v(135, -142.5) * mm});
            skLineSegment(sketch, "E366", {"start": v(133, -145) * mm, "end": v(133, -148) * mm});
            skLineSegment(sketch, "E367", {"start": v(144, -148) * mm, "end": v(144, -166.5) * mm});
            skLineSegment(sketch, "E368", {"start": v(144, -148) * mm, "end": v(138, -148) * mm});
            skLineSegment(sketch, "E369", {"start": v(135, -148) * mm, "end": v(135, -150.5) * mm});
            skLineSegment(sketch, "E370", {"start": v(150, -126.5) * mm, "end": v(150, -116.5) * mm});
            skLineSegment(sketch, "E371", {"start": v(144, -126.5) * mm, "end": v(144, -145) * mm});
            skLineSegment(sketch, "E372", {"start": v(144, -176.5) * mm, "end": v(144, -189.5) * mm});
            skLineSegment(sketch, "E373", {"start": v(-138, -5) * mm, "end": v(-138, -7.5) * mm});
            skLineSegment(sketch, "E374", {"start": v(-138, -2) * mm, "end": v(-138, 0.5) * mm});
            skLineSegment(sketch, "E375", {"start": v(-135, -5) * mm, "end": v(-133, -5) * mm});
            skLineSegment(sketch, "E376", {"start": v(-150, 26.5) * mm, "end": v(-150, 16.5) * mm});
            skLineSegment(sketch, "E377", {"start": v(-150, -23.5) * mm, "end": v(-150, -33.5) * mm});
            skLineSegment(sketch, "E378", {"start": v(-144, 26.5) * mm, "end": v(-150, 26.5) * mm});
            skLineSegment(sketch, "E379", {"start": v(-135, -2) * mm, "end": v(-135, 0.5) * mm});
            skLineSegment(sketch, "E380", {"start": v(-135, -5) * mm, "end": v(-135, -7.5) * mm});
            skLineSegment(sketch, "E381", {"start": v(-144, -5) * mm, "end": v(-144, -23.5) * mm});
            skLineSegment(sketch, "E382", {"start": v(-144, -33.5) * mm, "end": v(-150, -33.5) * mm});
            skLineSegment(sketch, "E383", {"start": v(-144, -5) * mm, "end": v(-138, -5) * mm});
            skLineSegment(sketch, "E384", {"start": v(-144, -2) * mm, "end": v(-138, -2) * mm});
            skLineSegment(sketch, "E385", {"start": v(-133, -2) * mm, "end": v(-133, -5) * mm});
            skLineSegment(sketch, "E386", {"start": v(-144, 16.5) * mm, "end": v(-144, -2) * mm});
            skLineSegment(sketch, "E387", {"start": v(-144, 16.5) * mm, "end": v(-150, 16.5) * mm});
            skLineSegment(sketch, "E388", {"start": v(-138, 0.5) * mm, "end": v(-135, 0.5) * mm});
            skLineSegment(sketch, "E389", {"start": v(-135, -2) * mm, "end": v(-133, -2) * mm});
            skLineSegment(sketch, "E390", {"start": v(-144, -23.5) * mm, "end": v(-150, -23.5) * mm});
            skLineSegment(sketch, "E391", {"start": v(-138, -7.5) * mm, "end": v(-135, -7.5) * mm});
            skLineSegment(sketch, "E392", {"start": v(-144, -33.5) * mm, "end": v(-144, -116.5) * mm});
            skLineSegment(sketch, "E393", {"start": v(-144, -166.5) * mm, "end": v(-150, -166.5) * mm});
            skLineSegment(sketch, "E394", {"start": v(-150, -116.5) * mm, "end": v(-150, -126.5) * mm});
            skLineSegment(sketch, "E395", {"start": v(-138, -148) * mm, "end": v(-138, -150.5) * mm});
            skLineSegment(sketch, "E396", {"start": v(-135, -145) * mm, "end": v(-135, -142.5) * mm});
            skLineSegment(sketch, "E397", {"start": v(-144, -116.5) * mm, "end": v(-150, -116.5) * mm});
            skLineSegment(sketch, "E398", {"start": v(-138, -145) * mm, "end": v(-138, -142.5) * mm});
            skLineSegment(sketch, "E399", {"start": v(-150, -166.5) * mm, "end": v(-150, -176.5) * mm});
            skLineSegment(sketch, "E400", {"start": v(-144, -126.5) * mm, "end": v(-144, -145) * mm});
            skLineSegment(sketch, "E401", {"start": v(-144, -176.5) * mm, "end": v(-150, -176.5) * mm});
            skLineSegment(sketch, "E402", {"start": v(-135, -148) * mm, "end": v(-135, -150.5) * mm});
            skLineSegment(sketch, "E403", {"start": v(-144, -145) * mm, "end": v(-138, -145) * mm});
            skLineSegment(sketch, "E404", {"start": v(-144, -148) * mm, "end": v(-144, -166.5) * mm});
            skLineSegment(sketch, "E405", {"start": v(-133, -145) * mm, "end": v(-133, -148) * mm});
            skLineSegment(sketch, "E406", {"start": v(-144, -126.5) * mm, "end": v(-150, -126.5) * mm});
            skLineSegment(sketch, "E407", {"start": v(-138, -142.5) * mm, "end": v(-135, -142.5) * mm});
            skLineSegment(sketch, "E408", {"start": v(-138, -150.5) * mm, "end": v(-135, -150.5) * mm});
            skLineSegment(sketch, "E409", {"start": v(-144, -148) * mm, "end": v(-138, -148) * mm});
            skLineSegment(sketch, "E410", {"start": v(-135, -148) * mm, "end": v(-133, -148) * mm});
            skLineSegment(sketch, "E411", {"start": v(-135, -145) * mm, "end": v(-133, -145) * mm});
            skLineSegment(sketch, "E412", {"start": v(100, -183.5) * mm, "end": v(100, -180.5) * mm});
            skLineSegment(sketch, "E413", {"start": v(102.5, -180.5) * mm, "end": v(100, -180.5) * mm});
            skLineSegment(sketch, "E414", {"start": v(74, -195.5) * mm, "end": v(84, -195.5) * mm});
            skLineSegment(sketch, "E415", {"start": v(-1.5, -180.5) * mm, "end": v(-1.5, -178.5) * mm});
            skLineSegment(sketch, "E416", {"start": v(1.5, -189.5) * mm, "end": v(20, -189.5) * mm});
            skLineSegment(sketch, "E417", {"start": v(-1.5, -180.5) * mm, "end": v(-4, -180.5) * mm});
            skLineSegment(sketch, "E418", {"start": v(4, -183.5) * mm, "end": v(4, -180.5) * mm});
            skLineSegment(sketch, "E419", {"start": v(-1.5, -183.5) * mm, "end": v(-4, -183.5) * mm});
            skLineSegment(sketch, "E420", {"start": v(20, -195.5) * mm, "end": v(30, -195.5) * mm});
            skLineSegment(sketch, "E421", {"start": v(-30, -195.5) * mm, "end": v(-20, -195.5) * mm});
            skLineSegment(sketch, "E422", {"start": v(1.5, -180.5) * mm, "end": v(4, -180.5) * mm});
            skLineSegment(sketch, "E423", {"start": v(20, -189.5) * mm, "end": v(20, -195.5) * mm});
            skLineSegment(sketch, "E424", {"start": v(1.5, -183.5) * mm, "end": v(4, -183.5) * mm});
            skLineSegment(sketch, "E425", {"start": v(-30, -189.5) * mm, "end": v(-30, -195.5) * mm});
            skLineSegment(sketch, "E426", {"start": v(1.5, -178.5) * mm, "end": v(-1.5, -178.5) * mm});
            skLineSegment(sketch, "E427", {"start": v(-4, -183.5) * mm, "end": v(-4, -180.5) * mm});
            skLineSegment(sketch, "E428", {"start": v(-1.5, -189.5) * mm, "end": v(-1.5, -183.5) * mm});
            skLineSegment(sketch, "E429", {"start": v(1.5, -189.5) * mm, "end": v(1.5, -183.5) * mm});
            skLineSegment(sketch, "E430", {"start": v(1.5, -180.5) * mm, "end": v(1.5, -178.5) * mm});
            skLineSegment(sketch, "E431", {"start": v(30, -189.5) * mm, "end": v(74, -189.5) * mm});
            skLineSegment(sketch, "E432", {"start": v(-124, -189.5) * mm, "end": v(-124, -195.5) * mm});
            skLineSegment(sketch, "E433", {"start": v(-105.5, -180.5) * mm, "end": v(-108, -180.5) * mm});
            skLineSegment(sketch, "E434", {"start": v(-74, -189.5) * mm, "end": v(-74, -195.5) * mm});
            skLineSegment(sketch, "E435", {"start": v(-84, -195.5) * mm, "end": v(-74, -195.5) * mm});
            skLineSegment(sketch, "E436", {"start": v(-105.5, -183.5) * mm, "end": v(-108, -183.5) * mm});
            skLineSegment(sketch, "E437", {"start": v(-105.5, -189.5) * mm, "end": v(-105.5, -183.5) * mm});
            skLineSegment(sketch, "E438", {"start": v(-100, -183.5) * mm, "end": v(-100, -180.5) * mm});
            skLineSegment(sketch, "E439", {"start": v(-84, -189.5) * mm, "end": v(-84, -195.5) * mm});
            skLineSegment(sketch, "E440", {"start": v(-134, -189.5) * mm, "end": v(-134, -195.5) * mm});
            skLineSegment(sketch, "E441", {"start": v(-102.5, -189.5) * mm, "end": v(-84, -189.5) * mm});
            skLineSegment(sketch, "E442", {"start": v(-102.5, -178.5) * mm, "end": v(-105.5, -178.5) * mm});
            skLineSegment(sketch, "E443", {"start": v(-134, -195.5) * mm, "end": v(-124, -195.5) * mm});
            skLineSegment(sketch, "E444", {"start": v(-102.5, -180.5) * mm, "end": v(-102.5, -178.5) * mm});
            skLineSegment(sketch, "E445", {"start": v(-108, -183.5) * mm, "end": v(-108, -180.5) * mm});
            skLineSegment(sketch, "E446", {"start": v(-102.5, -180.5) * mm, "end": v(-100, -180.5) * mm});
            skLineSegment(sketch, "E447", {"start": v(-124, -189.5) * mm, "end": v(-105.5, -189.5) * mm});
            skLineSegment(sketch, "E448", {"start": v(-102.5, -183.5) * mm, "end": v(-100, -183.5) * mm});
            skLineSegment(sketch, "E449", {"start": v(-102.5, -189.5) * mm, "end": v(-102.5, -183.5) * mm});
            skLineSegment(sketch, "E450", {"start": v(-105.5, -180.5) * mm, "end": v(-105.5, -178.5) * mm});
            skCircle(sketch, "E451", {"center": v(100.95, -81.92) * mm, "radius": 1.5 * mm});
            skCircle(sketch, "E452", {"center": v(76.95, -123.49) * mm, "radius": 1.5 * mm});
            skCircle(sketch, "E453", {"center": v(-100.95, -81.92) * mm, "radius": 1.5 * mm});
            skCircle(sketch, "E454", {"center": v(-76.95, -123.49) * mm, "radius": 1.5 * mm});
            skSolve(sketch);
        }
        {
            var Q0;
            Q0 = qSketchRegion(id + "F4", true);
            extrude(context, id + "F5", {"entities" : qUnion([Q0]), "oppositeDirection" : true, "depth" : 6 * mm, "offsetDistance" : 25 * mm});
        }
        {
            var Q0;
            Q0=makeQuery(id+"F3.opExtrude","SWEPT_FACE",FACE,{"disambiguationData":[OSD([sQuery(id+"F2.wireOp",EDGE,"E186")])]});
            cPlane(context, id + "F6", {"entities" : qUnion([Q0]), "cplaneType" : CPlaneType.OFFSET, "offset" : 0 * mm, "width" : 150 * mm, "height" : 150 * mm});
        }
        {
            var Q0;
            Q0=makeQuery(id+"F3.opExtrude","SWEPT_FACE",FACE,{"disambiguationData":[OSD([sQuery(id+"F2.wireOp",EDGE,"E86")])]});
            cPlane(context, id + "F7", {"entities" : qUnion([Q0]), "cplaneType" : CPlaneType.OFFSET, "offset" : 0 * mm, "width" : 150 * mm, "height" : 150 * mm});
        }
        {
            var Q0;
            Q0=qCreatedBy(id+"F6.planeOp",FACE);
            var sketch = newSketch(context, id + "F8", { "sketchPlane" : qUnion([Q0])});
            skCircle(sketch, "E455", {"center": v(107.5, 64.05) * mm, "radius": 1.5 * mm});
            skLineSegment(sketch, "E456", {"start": v(107.9, -62.6) * mm, "end": v(108.26, -62.75) * mm});
            skLineSegment(sketch, "E457", {"start": v(108.26, -62.75) * mm, "end": v(108.57, -62.99) * mm});
            skLineSegment(sketch, "E458", {"start": v(108.57, -62.99) * mm, "end": v(108.8, -63.3) * mm});
            skLineSegment(sketch, "E459", {"start": v(108.8, -63.3) * mm, "end": v(108.95, -63.66) * mm});
            skLineSegment(sketch, "E460", {"start": v(108.95, -63.66) * mm, "end": v(109, -64.05) * mm});
            skLineSegment(sketch, "E461", {"start": v(109, -64.05) * mm, "end": v(108.95, -64.44) * mm});
            skLineSegment(sketch, "E462", {"start": v(108.95, -64.44) * mm, "end": v(108.8, -64.8) * mm});
            skLineSegment(sketch, "E463", {"start": v(108.8, -64.8) * mm, "end": v(108.57, -65.11) * mm});
            skLineSegment(sketch, "E464", {"start": v(108.57, -65.11) * mm, "end": v(108.26, -65.35) * mm});
            skLineSegment(sketch, "E465", {"start": v(108.26, -65.35) * mm, "end": v(107.9, -65.5) * mm});
            skLineSegment(sketch, "E466", {"start": v(107.9, -65.5) * mm, "end": v(107.5, -65.55) * mm});
            skLineSegment(sketch, "E467", {"start": v(107.5, -65.55) * mm, "end": v(107.12, -65.5) * mm});
            skLineSegment(sketch, "E468", {"start": v(107.12, -65.5) * mm, "end": v(106.76, -65.35) * mm});
            skLineSegment(sketch, "E469", {"start": v(106.76, -65.35) * mm, "end": v(106.45, -65.11) * mm});
            skLineSegment(sketch, "E470", {"start": v(106.45, -65.11) * mm, "end": v(106.2, -64.8) * mm});
            skLineSegment(sketch, "E471", {"start": v(106.2, -64.8) * mm, "end": v(106.06, -64.44) * mm});
            skLineSegment(sketch, "E472", {"start": v(106.06, -64.44) * mm, "end": v(106, -64.05) * mm});
            skLineSegment(sketch, "E473", {"start": v(106, -64.05) * mm, "end": v(106.06, -63.66) * mm});
            skLineSegment(sketch, "E474", {"start": v(106.06, -63.66) * mm, "end": v(106.2, -63.3) * mm});
            skLineSegment(sketch, "E475", {"start": v(106.2, -63.3) * mm, "end": v(106.45, -62.99) * mm});
            skLineSegment(sketch, "E476", {"start": v(106.45, -62.99) * mm, "end": v(106.76, -62.75) * mm});
            skLineSegment(sketch, "E477", {"start": v(106.76, -62.75) * mm, "end": v(107.12, -62.6) * mm});
            skLineSegment(sketch, "E478", {"start": v(107.12, -62.6) * mm, "end": v(107.5, -62.55) * mm});
            skLineSegment(sketch, "E479", {"start": v(107.5, -62.55) * mm, "end": v(107.9, -62.6) * mm});
            skLineSegment(sketch, "E480", {"start": v(-193.25, 190.85) * mm, "end": v(-193.56, 191.09) * mm});
            skLineSegment(sketch, "E481", {"start": v(-193.56, 191.09) * mm, "end": v(-193.8, 191.4) * mm});
            skLineSegment(sketch, "E482", {"start": v(-193.8, 191.4) * mm, "end": v(-193.95, 191.76) * mm});
            skLineSegment(sketch, "E483", {"start": v(-193.95, 191.76) * mm, "end": v(-194, 192.15) * mm});
            skLineSegment(sketch, "E484", {"start": v(-194, 192.15) * mm, "end": v(-193.95, 192.54) * mm});
            skLineSegment(sketch, "E485", {"start": v(-193.95, 192.54) * mm, "end": v(-193.8, 192.9) * mm});
            skLineSegment(sketch, "E486", {"start": v(-193.8, 192.9) * mm, "end": v(-193.56, 193.21) * mm});
            skLineSegment(sketch, "E487", {"start": v(-193.56, 193.21) * mm, "end": v(-193.25, 193.45) * mm});
            skLineSegment(sketch, "E488", {"start": v(-193.25, 193.45) * mm, "end": v(-192.89, 193.6) * mm});
            skLineSegment(sketch, "E489", {"start": v(-192.89, 193.6) * mm, "end": v(-192.5, 193.65) * mm});
            skLineSegment(sketch, "E490", {"start": v(-192.5, 193.65) * mm, "end": v(-192.11, 193.6) * mm});
            skLineSegment(sketch, "E491", {"start": v(-192.11, 193.6) * mm, "end": v(-191.75, 193.45) * mm});
            skLineSegment(sketch, "E492", {"start": v(-191.75, 193.45) * mm, "end": v(-191.44, 193.21) * mm});
            skLineSegment(sketch, "E493", {"start": v(-191.44, 193.21) * mm, "end": v(-191.2, 192.9) * mm});
            skLineSegment(sketch, "E494", {"start": v(-191.2, 192.9) * mm, "end": v(-191.05, 192.54) * mm});
            skLineSegment(sketch, "E495", {"start": v(-191.05, 192.54) * mm, "end": v(-191, 192.15) * mm});
            skLineSegment(sketch, "E496", {"start": v(-191, 192.15) * mm, "end": v(-191.05, 191.76) * mm});
            skLineSegment(sketch, "E497", {"start": v(-191.05, 191.76) * mm, "end": v(-191.2, 191.4) * mm});
            skLineSegment(sketch, "E498", {"start": v(-191.2, 191.4) * mm, "end": v(-191.44, 191.09) * mm});
            skLineSegment(sketch, "E499", {"start": v(-191.44, 191.09) * mm, "end": v(-191.75, 190.85) * mm});
            skLineSegment(sketch, "E500", {"start": v(-191.75, 190.85) * mm, "end": v(-192.11, 190.7) * mm});
            skLineSegment(sketch, "E501", {"start": v(-192.11, 190.7) * mm, "end": v(-192.5, 190.65) * mm});
            skLineSegment(sketch, "E502", {"start": v(-192.5, 190.65) * mm, "end": v(-192.89, 190.7) * mm});
            skLineSegment(sketch, "E503", {"start": v(-192.89, 190.7) * mm, "end": v(-193.25, 190.85) * mm});
            skLineSegment(sketch, "E504", {"start": v(89.5, -218.15) * mm, "end": v(90.8, -218.06) * mm});
            skLineSegment(sketch, "E505", {"start": v(90.8, -218.06) * mm, "end": v(92.09, -217.8) * mm});
            skLineSegment(sketch, "E506", {"start": v(92.09, -217.8) * mm, "end": v(93.33, -217.39) * mm});
            skLineSegment(sketch, "E507", {"start": v(93.33, -217.39) * mm, "end": v(94.5, -216.81) * mm});
            skLineSegment(sketch, "E508", {"start": v(94.5, -216.81) * mm, "end": v(95.59, -216.08) * mm});
            skLineSegment(sketch, "E509", {"start": v(95.59, -216.08) * mm, "end": v(96.57, -215.22) * mm});
            skLineSegment(sketch, "E510", {"start": v(96.57, -215.22) * mm, "end": v(97.43, -214.24) * mm});
            skLineSegment(sketch, "E511", {"start": v(97.43, -214.24) * mm, "end": v(98.16, -213.15) * mm});
            skLineSegment(sketch, "E512", {"start": v(98.16, -213.15) * mm, "end": v(98.74, -211.98) * mm});
            skLineSegment(sketch, "E513", {"start": v(98.74, -211.98) * mm, "end": v(99.16, -210.74) * mm});
            skLineSegment(sketch, "E514", {"start": v(99.16, -210.74) * mm, "end": v(99.41, -209.46) * mm});
            skLineSegment(sketch, "E515", {"start": v(99.41, -209.46) * mm, "end": v(99.5, -208.15) * mm});
            skLineSegment(sketch, "E516", {"start": v(-189.5, 44.05) * mm, "end": v(-195.5, 44.05) * mm});
            skLineSegment(sketch, "E517", {"start": v(-192.5, 62.55) * mm, "end": v(-192.89, 62.6) * mm});
            skLineSegment(sketch, "E518", {"start": v(-192.89, 62.6) * mm, "end": v(-193.25, 62.75) * mm});
            skLineSegment(sketch, "E519", {"start": v(-193.25, 62.75) * mm, "end": v(-193.56, 62.99) * mm});
            skLineSegment(sketch, "E520", {"start": v(-193.56, 62.99) * mm, "end": v(-193.8, 63.3) * mm});
            skLineSegment(sketch, "E521", {"start": v(-193.8, 63.3) * mm, "end": v(-193.95, 63.66) * mm});
            skLineSegment(sketch, "E522", {"start": v(-193.95, 63.66) * mm, "end": v(-194, 64.05) * mm});
            skLineSegment(sketch, "E523", {"start": v(-194, 64.05) * mm, "end": v(-193.95, 64.44) * mm});
            skLineSegment(sketch, "E524", {"start": v(-193.95, 64.44) * mm, "end": v(-193.8, 64.8) * mm});
            skLineSegment(sketch, "E525", {"start": v(-193.8, 64.8) * mm, "end": v(-193.56, 65.11) * mm});
            skLineSegment(sketch, "E526", {"start": v(-193.56, 65.11) * mm, "end": v(-193.25, 65.35) * mm});
            skLineSegment(sketch, "E527", {"start": v(-193.25, 65.35) * mm, "end": v(-192.89, 65.5) * mm});
            skLineSegment(sketch, "E528", {"start": v(-192.89, 65.5) * mm, "end": v(-192.5, 65.55) * mm});
            skLineSegment(sketch, "E529", {"start": v(-192.5, 65.55) * mm, "end": v(-192.11, 65.5) * mm});
            skLineSegment(sketch, "E530", {"start": v(-192.11, 65.5) * mm, "end": v(-191.75, 65.35) * mm});
            skLineSegment(sketch, "E531", {"start": v(-191.75, 65.35) * mm, "end": v(-191.44, 65.11) * mm});
            skLineSegment(sketch, "E532", {"start": v(-191.44, 65.11) * mm, "end": v(-191.2, 64.8) * mm});
            skLineSegment(sketch, "E533", {"start": v(-191.2, 64.8) * mm, "end": v(-191.05, 64.44) * mm});
            skLineSegment(sketch, "E534", {"start": v(-191.05, 64.44) * mm, "end": v(-191, 64.05) * mm});
            skLineSegment(sketch, "E535", {"start": v(-191, 64.05) * mm, "end": v(-191.05, 63.66) * mm});
            skLineSegment(sketch, "E536", {"start": v(-191.05, 63.66) * mm, "end": v(-191.2, 63.3) * mm});
            skLineSegment(sketch, "E537", {"start": v(-191.2, 63.3) * mm, "end": v(-191.44, 62.99) * mm});
            skLineSegment(sketch, "E538", {"start": v(-191.44, 62.99) * mm, "end": v(-191.75, 62.75) * mm});
            skLineSegment(sketch, "E539", {"start": v(-191.75, 62.75) * mm, "end": v(-192.11, 62.6) * mm});
            skLineSegment(sketch, "E540", {"start": v(-192.11, 62.6) * mm, "end": v(-192.5, 62.55) * mm});
            skLineSegment(sketch, "E541", {"start": v(-189.5, 34.05) * mm, "end": v(-189.5, 44.05) * mm});
            skLineSegment(sketch, "E542", {"start": v(-195.5, 34.05) * mm, "end": v(-189.5, 34.05) * mm});
            skLineSegment(sketch, "E543", {"start": v(-189.5, 94.05) * mm, "end": v(-195.5, 94.05) * mm});
            skLineSegment(sketch, "E544", {"start": v(169.6, -234.15) * mm, "end": v(169.6, -220.85) * mm});
            skLineSegment(sketch, "E545", {"start": v(150.6, -220.85) * mm, "end": v(150.6, -234.15) * mm});
            skLineSegment(sketch, "E546", {"start": v(169.6, -220.85) * mm, "end": v(150.6, -220.85) * mm});
            skLineSegment(sketch, "E547", {"start": v(189.5, 242.15) * mm, "end": v(189.5, -242.15) * mm});
            skLineSegment(sketch, "E548", {"start": v(-195.5, 94.05) * mm, "end": v(-195.5, 84.05) * mm});
            skLineSegment(sketch, "E549", {"start": v(-195.5, 84.05) * mm, "end": v(-189.5, 84.05) * mm});
            skLineSegment(sketch, "E550", {"start": v(-189.5, 84.05) * mm, "end": v(-189.5, 94.05) * mm});
            skLineSegment(sketch, "E551", {"start": v(110.5, -94.05) * mm, "end": v(104.5, -94.05) * mm});
            skLineSegment(sketch, "E552", {"start": v(106.2, -191.4) * mm, "end": v(106.45, -191.09) * mm});
            skLineSegment(sketch, "E553", {"start": v(106.45, -191.09) * mm, "end": v(106.76, -190.85) * mm});
            skLineSegment(sketch, "E554", {"start": v(106.76, -190.85) * mm, "end": v(107.12, -190.7) * mm});
            skLineSegment(sketch, "E555", {"start": v(107.12, -190.7) * mm, "end": v(107.5, -190.65) * mm});
            skLineSegment(sketch, "E556", {"start": v(107.5, -190.65) * mm, "end": v(107.9, -190.7) * mm});
            skLineSegment(sketch, "E557", {"start": v(107.9, -190.7) * mm, "end": v(108.26, -190.85) * mm});
            skLineSegment(sketch, "E558", {"start": v(108.26, -190.85) * mm, "end": v(108.57, -191.09) * mm});
            skLineSegment(sketch, "E559", {"start": v(108.57, -191.09) * mm, "end": v(108.8, -191.4) * mm});
            skLineSegment(sketch, "E560", {"start": v(108.8, -191.4) * mm, "end": v(108.95, -191.76) * mm});
            skLineSegment(sketch, "E561", {"start": v(108.95, -191.76) * mm, "end": v(109, -192.15) * mm});
            skLineSegment(sketch, "E562", {"start": v(109, -192.15) * mm, "end": v(108.95, -192.54) * mm});
            skLineSegment(sketch, "E563", {"start": v(108.95, -192.54) * mm, "end": v(108.8, -192.9) * mm});
            skLineSegment(sketch, "E564", {"start": v(108.8, -192.9) * mm, "end": v(108.57, -193.21) * mm});
            skLineSegment(sketch, "E565", {"start": v(108.57, -193.21) * mm, "end": v(108.26, -193.45) * mm});
            skLineSegment(sketch, "E566", {"start": v(108.26, -193.45) * mm, "end": v(107.9, -193.6) * mm});
            skLineSegment(sketch, "E567", {"start": v(107.9, -193.6) * mm, "end": v(107.5, -193.65) * mm});
            skLineSegment(sketch, "E568", {"start": v(107.5, -193.65) * mm, "end": v(107.12, -193.6) * mm});
            skLineSegment(sketch, "E569", {"start": v(107.12, -193.6) * mm, "end": v(106.76, -193.45) * mm});
            skLineSegment(sketch, "E570", {"start": v(106.76, -193.45) * mm, "end": v(106.45, -193.21) * mm});
            skLineSegment(sketch, "E571", {"start": v(106.45, -193.21) * mm, "end": v(106.2, -192.9) * mm});
            skLineSegment(sketch, "E572", {"start": v(106.2, -192.9) * mm, "end": v(106.06, -192.54) * mm});
            skLineSegment(sketch, "E573", {"start": v(106.06, -192.54) * mm, "end": v(106, -192.15) * mm});
            skLineSegment(sketch, "E574", {"start": v(106, -192.15) * mm, "end": v(106.06, -191.76) * mm});
            skLineSegment(sketch, "E575", {"start": v(106.06, -191.76) * mm, "end": v(106.2, -191.4) * mm});
            skLineSegment(sketch, "E576", {"start": v(139.5, 241.65) * mm, "end": v(139.88, 241.6) * mm});
            skLineSegment(sketch, "E577", {"start": v(139.88, 241.6) * mm, "end": v(140.24, 241.45) * mm});
            skLineSegment(sketch, "E578", {"start": v(140.24, 241.45) * mm, "end": v(140.55, 241.21) * mm});
            skLineSegment(sketch, "E579", {"start": v(140.55, 241.21) * mm, "end": v(140.8, 240.9) * mm});
            skLineSegment(sketch, "E580", {"start": v(140.8, 240.9) * mm, "end": v(140.94, 240.54) * mm});
            skLineSegment(sketch, "E581", {"start": v(140.94, 240.54) * mm, "end": v(141, 240.15) * mm});
            skLineSegment(sketch, "E582", {"start": v(141, 240.15) * mm, "end": v(140.94, 239.76) * mm});
            skLineSegment(sketch, "E583", {"start": v(140.94, 239.76) * mm, "end": v(140.8, 239.4) * mm});
            skLineSegment(sketch, "E584", {"start": v(140.8, 239.4) * mm, "end": v(140.55, 239.09) * mm});
            skLineSegment(sketch, "E585", {"start": v(140.55, 239.09) * mm, "end": v(140.24, 238.85) * mm});
            skLineSegment(sketch, "E586", {"start": v(140.24, 238.85) * mm, "end": v(139.88, 238.7) * mm});
            skLineSegment(sketch, "E587", {"start": v(139.88, 238.7) * mm, "end": v(139.5, 238.65) * mm});
            skLineSegment(sketch, "E588", {"start": v(139.5, 238.65) * mm, "end": v(139.1, 238.7) * mm});
            skLineSegment(sketch, "E589", {"start": v(139.1, 238.7) * mm, "end": v(138.74, 238.85) * mm});
            skLineSegment(sketch, "E590", {"start": v(138.74, 238.85) * mm, "end": v(138.43, 239.09) * mm});
            skLineSegment(sketch, "E591", {"start": v(138.43, 239.09) * mm, "end": v(138.2, 239.4) * mm});
            skLineSegment(sketch, "E592", {"start": v(138.2, 239.4) * mm, "end": v(138.05, 239.76) * mm});
            skLineSegment(sketch, "E593", {"start": v(138.05, 239.76) * mm, "end": v(138, 240.15) * mm});
            skLineSegment(sketch, "E594", {"start": v(138, 240.15) * mm, "end": v(138.05, 240.54) * mm});
            skLineSegment(sketch, "E595", {"start": v(138.05, 240.54) * mm, "end": v(138.2, 240.9) * mm});
            skLineSegment(sketch, "E596", {"start": v(138.2, 240.9) * mm, "end": v(138.43, 241.21) * mm});
            skLineSegment(sketch, "E597", {"start": v(138.43, 241.21) * mm, "end": v(138.74, 241.45) * mm});
            skLineSegment(sketch, "E598", {"start": v(138.74, 241.45) * mm, "end": v(139.1, 241.6) * mm});
            skLineSegment(sketch, "E599", {"start": v(139.1, 241.6) * mm, "end": v(139.5, 241.65) * mm});
            skLineSegment(sketch, "E600", {"start": v(104.5, -94.05) * mm, "end": v(104.5, -84.05) * mm});
            skLineSegment(sketch, "E601", {"start": v(104.5, -84.05) * mm, "end": v(110.5, -84.05) * mm});
            skLineSegment(sketch, "E602", {"start": v(110.5, -84.05) * mm, "end": v(110.5, -94.05) * mm});
            skLineSegment(sketch, "E603", {"start": v(159.5, 237.15) * mm, "end": v(159.5, 243.15) * mm});
            skLineSegment(sketch, "E604", {"start": v(169.5, 243.15) * mm, "end": v(159.5, 243.15) * mm});
            skLineSegment(sketch, "E605", {"start": v(169.5, 243.15) * mm, "end": v(169.5, 237.15) * mm});
            skLineSegment(sketch, "E606", {"start": v(169.5, 237.15) * mm, "end": v(159.5, 237.15) * mm});
            skLineSegment(sketch, "E607", {"start": v(110.5, -162.15) * mm, "end": v(110.5, -172.15) * mm});
            skLineSegment(sketch, "E608", {"start": v(110.5, -172.15) * mm, "end": v(104.5, -172.15) * mm});
            skLineSegment(sketch, "E609", {"start": v(106.44, 193.21) * mm, "end": v(106.75, 193.45) * mm});
            skLineSegment(sketch, "E610", {"start": v(106.75, 193.45) * mm, "end": v(107.11, 193.6) * mm});
            skLineSegment(sketch, "E611", {"start": v(107.11, 193.6) * mm, "end": v(107.5, 193.65) * mm});
            skLineSegment(sketch, "E612", {"start": v(107.5, 193.65) * mm, "end": v(107.89, 193.6) * mm});
            skLineSegment(sketch, "E613", {"start": v(107.89, 193.6) * mm, "end": v(108.25, 193.45) * mm});
            skLineSegment(sketch, "E614", {"start": v(108.25, 193.45) * mm, "end": v(108.56, 193.21) * mm});
            skLineSegment(sketch, "E615", {"start": v(108.56, 193.21) * mm, "end": v(108.8, 192.9) * mm});
            skLineSegment(sketch, "E616", {"start": v(108.8, 192.9) * mm, "end": v(108.95, 192.54) * mm});
            skLineSegment(sketch, "E617", {"start": v(108.95, 192.54) * mm, "end": v(109, 192.15) * mm});
            skLineSegment(sketch, "E618", {"start": v(109, 192.15) * mm, "end": v(108.95, 191.76) * mm});
            skLineSegment(sketch, "E619", {"start": v(108.95, 191.76) * mm, "end": v(108.8, 191.4) * mm});
            skLineSegment(sketch, "E620", {"start": v(108.8, 191.4) * mm, "end": v(108.56, 191.09) * mm});
            skLineSegment(sketch, "E621", {"start": v(108.56, 191.09) * mm, "end": v(108.25, 190.85) * mm});
            skLineSegment(sketch, "E622", {"start": v(108.25, 190.85) * mm, "end": v(107.89, 190.7) * mm});
            skLineSegment(sketch, "E623", {"start": v(107.89, 190.7) * mm, "end": v(107.5, 190.65) * mm});
            skLineSegment(sketch, "E624", {"start": v(107.5, 190.65) * mm, "end": v(107.11, 190.7) * mm});
            skLineSegment(sketch, "E625", {"start": v(107.11, 190.7) * mm, "end": v(106.75, 190.85) * mm});
            skLineSegment(sketch, "E626", {"start": v(106.75, 190.85) * mm, "end": v(106.44, 191.09) * mm});
            skLineSegment(sketch, "E627", {"start": v(106.44, 191.09) * mm, "end": v(106.2, 191.4) * mm});
            skLineSegment(sketch, "E628", {"start": v(106.2, 191.4) * mm, "end": v(106.05, 191.76) * mm});
            skLineSegment(sketch, "E629", {"start": v(106.05, 191.76) * mm, "end": v(106, 192.15) * mm});
            skLineSegment(sketch, "E630", {"start": v(106, 192.15) * mm, "end": v(106.05, 192.54) * mm});
            skLineSegment(sketch, "E631", {"start": v(106.05, 192.54) * mm, "end": v(106.2, 192.9) * mm});
            skLineSegment(sketch, "E632", {"start": v(106.2, 192.9) * mm, "end": v(106.44, 193.21) * mm});
            skLineSegment(sketch, "E633", {"start": v(140.8, -239.4) * mm, "end": v(140.95, -239.76) * mm});
            skLineSegment(sketch, "E634", {"start": v(140.95, -239.76) * mm, "end": v(141, -240.15) * mm});
            skLineSegment(sketch, "E635", {"start": v(141, -240.15) * mm, "end": v(140.95, -240.54) * mm});
            skLineSegment(sketch, "E636", {"start": v(140.95, -240.54) * mm, "end": v(140.8, -240.9) * mm});
            skLineSegment(sketch, "E637", {"start": v(140.8, -240.9) * mm, "end": v(140.56, -241.21) * mm});
            skLineSegment(sketch, "E638", {"start": v(140.56, -241.21) * mm, "end": v(140.25, -241.45) * mm});
            skLineSegment(sketch, "E639", {"start": v(140.25, -241.45) * mm, "end": v(139.89, -241.6) * mm});
            skLineSegment(sketch, "E640", {"start": v(139.89, -241.6) * mm, "end": v(139.5, -241.65) * mm});
            skLineSegment(sketch, "E641", {"start": v(139.5, -241.65) * mm, "end": v(139.11, -241.6) * mm});
            skLineSegment(sketch, "E642", {"start": v(139.11, -241.6) * mm, "end": v(138.75, -241.45) * mm});
            skLineSegment(sketch, "E643", {"start": v(138.75, -241.45) * mm, "end": v(138.44, -241.21) * mm});
            skLineSegment(sketch, "E644", {"start": v(138.44, -241.21) * mm, "end": v(138.2, -240.9) * mm});
            skLineSegment(sketch, "E645", {"start": v(138.2, -240.9) * mm, "end": v(138.05, -240.54) * mm});
            skLineSegment(sketch, "E646", {"start": v(138.05, -240.54) * mm, "end": v(138, -240.15) * mm});
            skLineSegment(sketch, "E647", {"start": v(138, -240.15) * mm, "end": v(138.05, -239.76) * mm});
            skLineSegment(sketch, "E648", {"start": v(138.05, -239.76) * mm, "end": v(138.2, -239.4) * mm});
            skLineSegment(sketch, "E649", {"start": v(138.2, -239.4) * mm, "end": v(138.44, -239.09) * mm});
            skLineSegment(sketch, "E650", {"start": v(138.44, -239.09) * mm, "end": v(138.75, -238.85) * mm});
            skLineSegment(sketch, "E651", {"start": v(138.75, -238.85) * mm, "end": v(139.11, -238.7) * mm});
            skLineSegment(sketch, "E652", {"start": v(139.11, -238.7) * mm, "end": v(139.5, -238.65) * mm});
            skLineSegment(sketch, "E653", {"start": v(139.5, -238.65) * mm, "end": v(139.89, -238.7) * mm});
            skLineSegment(sketch, "E654", {"start": v(139.89, -238.7) * mm, "end": v(140.25, -238.85) * mm});
            skLineSegment(sketch, "E655", {"start": v(140.25, -238.85) * mm, "end": v(140.56, -239.09) * mm});
            skLineSegment(sketch, "E656", {"start": v(140.56, -239.09) * mm, "end": v(140.8, -239.4) * mm});
            skLineSegment(sketch, "E657", {"start": v(104.5, -172.15) * mm, "end": v(104.5, -162.15) * mm});
            skLineSegment(sketch, "E658", {"start": v(104.5, -162.15) * mm, "end": v(110.5, -162.15) * mm});
            skLineSegment(sketch, "E659", {"start": v(104.5, -222.15) * mm, "end": v(104.5, -212.15) * mm});
            skLineSegment(sketch, "E660", {"start": v(104.5, -212.15) * mm, "end": v(110.5, -212.15) * mm});
            skLineSegment(sketch, "E661", {"start": v(110.5, -212.15) * mm, "end": v(110.5, -222.15) * mm});
            skLineSegment(sketch, "E662", {"start": v(110.5, -222.15) * mm, "end": v(104.5, -222.15) * mm});
            skLineSegment(sketch, "E663", {"start": v(-189.5, 212.15) * mm, "end": v(-189.5, 222.15) * mm});
            skLineSegment(sketch, "E664", {"start": v(-145, 240.15) * mm, "end": v(-145.05, 239.76) * mm});
            skLineSegment(sketch, "E665", {"start": v(-145.05, 239.76) * mm, "end": v(-145.2, 239.4) * mm});
            skLineSegment(sketch, "E666", {"start": v(-145.2, 239.4) * mm, "end": v(-145.44, 239.09) * mm});
            skLineSegment(sketch, "E667", {"start": v(-145.44, 239.09) * mm, "end": v(-145.75, 238.85) * mm});
            skLineSegment(sketch, "E668", {"start": v(-145.75, 238.85) * mm, "end": v(-146.11, 238.7) * mm});
            skLineSegment(sketch, "E669", {"start": v(-146.11, 238.7) * mm, "end": v(-146.5, 238.65) * mm});
            skLineSegment(sketch, "E670", {"start": v(-146.5, 238.65) * mm, "end": v(-146.89, 238.7) * mm});
            skLineSegment(sketch, "E671", {"start": v(-146.89, 238.7) * mm, "end": v(-147.25, 238.85) * mm});
            skLineSegment(sketch, "E672", {"start": v(-147.25, 238.85) * mm, "end": v(-147.56, 239.09) * mm});
            skLineSegment(sketch, "E673", {"start": v(-147.56, 239.09) * mm, "end": v(-147.8, 239.4) * mm});
            skLineSegment(sketch, "E674", {"start": v(-147.8, 239.4) * mm, "end": v(-147.95, 239.76) * mm});
            skLineSegment(sketch, "E675", {"start": v(-147.95, 239.76) * mm, "end": v(-148, 240.15) * mm});
            skLineSegment(sketch, "E676", {"start": v(-148, 240.15) * mm, "end": v(-147.95, 240.54) * mm});
            skLineSegment(sketch, "E677", {"start": v(-147.95, 240.54) * mm, "end": v(-147.8, 240.9) * mm});
            skLineSegment(sketch, "E678", {"start": v(-147.8, 240.9) * mm, "end": v(-147.56, 241.21) * mm});
            skLineSegment(sketch, "E679", {"start": v(-147.56, 241.21) * mm, "end": v(-147.25, 241.45) * mm});
            skLineSegment(sketch, "E680", {"start": v(-147.25, 241.45) * mm, "end": v(-146.89, 241.6) * mm});
            skLineSegment(sketch, "E681", {"start": v(-146.89, 241.6) * mm, "end": v(-146.5, 241.65) * mm});
            skLineSegment(sketch, "E682", {"start": v(-146.5, 241.65) * mm, "end": v(-146.11, 241.6) * mm});
            skLineSegment(sketch, "E683", {"start": v(-146.11, 241.6) * mm, "end": v(-145.75, 241.45) * mm});
            skLineSegment(sketch, "E684", {"start": v(-145.75, 241.45) * mm, "end": v(-145.44, 241.21) * mm});
            skLineSegment(sketch, "E685", {"start": v(-145.44, 241.21) * mm, "end": v(-145.2, 240.9) * mm});
            skLineSegment(sketch, "E686", {"start": v(-145.2, 240.9) * mm, "end": v(-145.05, 240.54) * mm});
            skLineSegment(sketch, "E687", {"start": v(-145.05, 240.54) * mm, "end": v(-145, 240.15) * mm});
            skLineSegment(sketch, "E688", {"start": v(-191, -64.05) * mm, "end": v(-191.05, -64.44) * mm});
            skLineSegment(sketch, "E689", {"start": v(-191.05, -64.44) * mm, "end": v(-191.2, -64.8) * mm});
            skLineSegment(sketch, "E690", {"start": v(-191.2, -64.8) * mm, "end": v(-191.44, -65.11) * mm});
            skLineSegment(sketch, "E691", {"start": v(-191.44, -65.11) * mm, "end": v(-191.75, -65.35) * mm});
            skLineSegment(sketch, "E692", {"start": v(-191.75, -65.35) * mm, "end": v(-192.11, -65.5) * mm});
            skLineSegment(sketch, "E693", {"start": v(-192.11, -65.5) * mm, "end": v(-192.5, -65.55) * mm});
            skLineSegment(sketch, "E694", {"start": v(-192.5, -65.55) * mm, "end": v(-192.89, -65.5) * mm});
            skLineSegment(sketch, "E695", {"start": v(-192.89, -65.5) * mm, "end": v(-193.25, -65.35) * mm});
            skLineSegment(sketch, "E696", {"start": v(-193.25, -65.35) * mm, "end": v(-193.56, -65.11) * mm});
            skLineSegment(sketch, "E697", {"start": v(-193.56, -65.11) * mm, "end": v(-193.8, -64.8) * mm});
            skLineSegment(sketch, "E698", {"start": v(-193.8, -64.8) * mm, "end": v(-193.95, -64.44) * mm});
            skLineSegment(sketch, "E699", {"start": v(-193.95, -64.44) * mm, "end": v(-194, -64.05) * mm});
            skLineSegment(sketch, "E700", {"start": v(-194, -64.05) * mm, "end": v(-193.95, -63.66) * mm});
            skLineSegment(sketch, "E701", {"start": v(-193.95, -63.66) * mm, "end": v(-193.8, -63.3) * mm});
            skLineSegment(sketch, "E702", {"start": v(-193.8, -63.3) * mm, "end": v(-193.56, -62.99) * mm});
            skLineSegment(sketch, "E703", {"start": v(-193.56, -62.99) * mm, "end": v(-193.25, -62.75) * mm});
            skLineSegment(sketch, "E704", {"start": v(-193.25, -62.75) * mm, "end": v(-192.89, -62.6) * mm});
            skLineSegment(sketch, "E705", {"start": v(-192.89, -62.6) * mm, "end": v(-192.5, -62.55) * mm});
            skLineSegment(sketch, "E706", {"start": v(-192.5, -62.55) * mm, "end": v(-192.11, -62.6) * mm});
            skLineSegment(sketch, "E707", {"start": v(-192.11, -62.6) * mm, "end": v(-191.75, -62.75) * mm});
            skLineSegment(sketch, "E708", {"start": v(-191.75, -62.75) * mm, "end": v(-191.44, -62.99) * mm});
            skLineSegment(sketch, "E709", {"start": v(-191.44, -62.99) * mm, "end": v(-191.2, -63.3) * mm});
            skLineSegment(sketch, "E710", {"start": v(-191.2, -63.3) * mm, "end": v(-191.05, -63.66) * mm});
            skLineSegment(sketch, "E711", {"start": v(-191.05, -63.66) * mm, "end": v(-191, -64.05) * mm});
            skLineSegment(sketch, "E712", {"start": v(-195.5, -84.05) * mm, "end": v(-195.5, -94.05) * mm});
            skLineSegment(sketch, "E713", {"start": v(-195.5, -44.05) * mm, "end": v(-189.5, -44.05) * mm});
            skLineSegment(sketch, "E714", {"start": v(-195.5, -34.05) * mm, "end": v(-195.5, -44.05) * mm});
            skLineSegment(sketch, "E715", {"start": v(-161.5, -198.15) * mm, "end": v(-161.36, -169.98) * mm});
            skLineSegment(sketch, "E716", {"start": v(-161.36, -169.98) * mm, "end": v(-160.94, -141.8) * mm});
            skLineSegment(sketch, "E717", {"start": v(-160.94, -141.8) * mm, "end": v(-160.25, -113.64) * mm});
            skLineSegment(sketch, "E718", {"start": v(-160.25, -113.64) * mm, "end": v(-159.28, -85.48) * mm});
            skLineSegment(sketch, "E719", {"start": v(-159.28, -85.48) * mm, "end": v(-158.02, -57.34) * mm});
            skLineSegment(sketch, "E720", {"start": v(-158.02, -57.34) * mm, "end": v(-156.5, -29.2) * mm});
            skLineSegment(sketch, "E721", {"start": v(-156.5, -29.2) * mm, "end": v(-154.69, -1.09) * mm});
            skLineSegment(sketch, "E722", {"start": v(-154.69, -1.09) * mm, "end": v(-152.6, 27) * mm});
            skLineSegment(sketch, "E723", {"start": v(-152.6, 27) * mm, "end": v(-150.24, 55.08) * mm});
            skLineSegment(sketch, "E724", {"start": v(-150.24, 55.08) * mm, "end": v(-147.6, 83.13) * mm});
            skLineSegment(sketch, "E725", {"start": v(-147.6, 83.13) * mm, "end": v(-144.7, 111.16) * mm});
            skLineSegment(sketch, "E726", {"start": v(-144.7, 111.16) * mm, "end": v(-142.64, 129.15) * mm});
            skLineSegment(sketch, "E727", {"start": v(-2.2, 239.4) * mm, "end": v(-2.44, 239.09) * mm});
            skLineSegment(sketch, "E728", {"start": v(-2.44, 239.09) * mm, "end": v(-2.75, 238.85) * mm});
            skLineSegment(sketch, "E729", {"start": v(-2.75, 238.85) * mm, "end": v(-3.11, 238.7) * mm});
            skLineSegment(sketch, "E730", {"start": v(-3.11, 238.7) * mm, "end": v(-3.5, 238.65) * mm});
            skLineSegment(sketch, "E731", {"start": v(-3.5, 238.65) * mm, "end": v(-3.89, 238.7) * mm});
            skLineSegment(sketch, "E732", {"start": v(-3.89, 238.7) * mm, "end": v(-4.25, 238.85) * mm});
            skLineSegment(sketch, "E733", {"start": v(-4.25, 238.85) * mm, "end": v(-4.56, 239.09) * mm});
            skLineSegment(sketch, "E734", {"start": v(-4.56, 239.09) * mm, "end": v(-4.8, 239.4) * mm});
            skLineSegment(sketch, "E735", {"start": v(-4.8, 239.4) * mm, "end": v(-4.95, 239.76) * mm});
            skLineSegment(sketch, "E736", {"start": v(-4.95, 239.76) * mm, "end": v(-5, 240.15) * mm});
            skLineSegment(sketch, "E737", {"start": v(-5, 240.15) * mm, "end": v(-4.95, 240.54) * mm});
            skLineSegment(sketch, "E738", {"start": v(-4.95, 240.54) * mm, "end": v(-4.8, 240.9) * mm});
            skLineSegment(sketch, "E739", {"start": v(-4.8, 240.9) * mm, "end": v(-4.56, 241.21) * mm});
            skLineSegment(sketch, "E740", {"start": v(-4.56, 241.21) * mm, "end": v(-4.25, 241.45) * mm});
            skLineSegment(sketch, "E741", {"start": v(-4.25, 241.45) * mm, "end": v(-3.89, 241.6) * mm});
            skLineSegment(sketch, "E742", {"start": v(-3.89, 241.6) * mm, "end": v(-3.5, 241.65) * mm});
            skLineSegment(sketch, "E743", {"start": v(-3.5, 241.65) * mm, "end": v(-3.11, 241.6) * mm});
            skLineSegment(sketch, "E744", {"start": v(-3.11, 241.6) * mm, "end": v(-2.75, 241.45) * mm});
            skLineSegment(sketch, "E745", {"start": v(-2.75, 241.45) * mm, "end": v(-2.44, 241.21) * mm});
            skLineSegment(sketch, "E746", {"start": v(-2.44, 241.21) * mm, "end": v(-2.2, 240.9) * mm});
            skLineSegment(sketch, "E747", {"start": v(-2.2, 240.9) * mm, "end": v(-2.05, 240.54) * mm});
            skLineSegment(sketch, "E748", {"start": v(-2.05, 240.54) * mm, "end": v(-2, 240.15) * mm});
            skLineSegment(sketch, "E749", {"start": v(-2, 240.15) * mm, "end": v(-2.05, 239.76) * mm});
            skLineSegment(sketch, "E750", {"start": v(-2.05, 239.76) * mm, "end": v(-2.2, 239.4) * mm});
            skLineSegment(sketch, "E751", {"start": v(104.5, 172.15) * mm, "end": v(110.5, 172.15) * mm});
            skLineSegment(sketch, "E752", {"start": v(110.5, 162.15) * mm, "end": v(104.5, 162.15) * mm});
            skLineSegment(sketch, "E753", {"start": v(109.5, 237.15) * mm, "end": v(109.5, 243.15) * mm});
            skLineSegment(sketch, "E754", {"start": v(119.5, 243.15) * mm, "end": v(109.5, 243.15) * mm});
            skLineSegment(sketch, "E755", {"start": v(119.5, 243.15) * mm, "end": v(119.5, 237.15) * mm});
            skCircle(sketch, "E756", {"center": v(-192.5, -192.15) * mm, "radius": 1.5 * mm});
            skLineSegment(sketch, "E757", {"start": v(-195.5, -222.15) * mm, "end": v(-189.5, -222.15) * mm});
            skLineSegment(sketch, "E758", {"start": v(-189.5, -44.05) * mm, "end": v(-189.5, -34.05) * mm});
            skLineSegment(sketch, "E759", {"start": v(-189.5, -34.05) * mm, "end": v(-195.5, -34.05) * mm});
            skLineSegment(sketch, "E760", {"start": v(110.5, 94.05) * mm, "end": v(104.5, 94.05) * mm});
            skLineSegment(sketch, "E761", {"start": v(110.5, 84.05) * mm, "end": v(110.5, 94.05) * mm});
            skLineSegment(sketch, "E762", {"start": v(110.5, 222.15) * mm, "end": v(110.5, 212.15) * mm});
            skLineSegment(sketch, "E763", {"start": v(110.5, 212.15) * mm, "end": v(104.5, 212.15) * mm});
            skLineSegment(sketch, "E764", {"start": v(104.5, 212.15) * mm, "end": v(104.5, 222.15) * mm});
            skLineSegment(sketch, "E765", {"start": v(104.5, 222.15) * mm, "end": v(110.5, 222.15) * mm});
            skLineSegment(sketch, "E766", {"start": v(104.5, 44.05) * mm, "end": v(104.5, 34.05) * mm});
            skLineSegment(sketch, "E767", {"start": v(110.5, 44.05) * mm, "end": v(104.5, 44.05) * mm});
            skLineSegment(sketch, "E768", {"start": v(110.5, 34.05) * mm, "end": v(110.5, 44.05) * mm});
            skLineSegment(sketch, "E769", {"start": v(104.5, 34.05) * mm, "end": v(110.5, 34.05) * mm});
            skLineSegment(sketch, "E770", {"start": v(16.5, 237.15) * mm, "end": v(16.5, 243.15) * mm});
            skLineSegment(sketch, "E771", {"start": v(26.5, 243.15) * mm, "end": v(16.5, 243.15) * mm});
            skLineSegment(sketch, "E772", {"start": v(26.5, 243.15) * mm, "end": v(26.5, 237.15) * mm});
            skLineSegment(sketch, "E773", {"start": v(26.5, 237.15) * mm, "end": v(16.5, 237.15) * mm});
            skLineSegment(sketch, "E774", {"start": v(-126.5, 237.15) * mm, "end": v(-126.5, 243.15) * mm});
            skLineSegment(sketch, "E775", {"start": v(-116.5, 243.15) * mm, "end": v(-116.5, 237.15) * mm});
            skLineSegment(sketch, "E776", {"start": v(-116.5, 237.15) * mm, "end": v(-126.5, 237.15) * mm});
            skLineSegment(sketch, "E777", {"start": v(-176.5, 237.15) * mm, "end": v(-176.5, 243.15) * mm});
            skLineSegment(sketch, "E778", {"start": v(-176.5, 243.15) * mm, "end": v(-166.5, 243.15) * mm});
            skLineSegment(sketch, "E779", {"start": v(-166.5, 243.15) * mm, "end": v(-166.5, 237.15) * mm});
            skLineSegment(sketch, "E780", {"start": v(-166.5, 237.15) * mm, "end": v(-176.5, 237.15) * mm});
            skLineSegment(sketch, "E781", {"start": v(-2.2, -239.4) * mm, "end": v(-2.05, -239.76) * mm});
            skLineSegment(sketch, "E782", {"start": v(-2.05, -239.76) * mm, "end": v(-2, -240.15) * mm});
            skLineSegment(sketch, "E783", {"start": v(-2, -240.15) * mm, "end": v(-2.05, -240.54) * mm});
            skLineSegment(sketch, "E784", {"start": v(-2.05, -240.54) * mm, "end": v(-2.2, -240.9) * mm});
            skLineSegment(sketch, "E785", {"start": v(-2.2, -240.9) * mm, "end": v(-2.44, -241.21) * mm});
            skLineSegment(sketch, "E786", {"start": v(-2.44, -241.21) * mm, "end": v(-2.75, -241.45) * mm});
            skLineSegment(sketch, "E787", {"start": v(-2.75, -241.45) * mm, "end": v(-3.11, -241.6) * mm});
            skLineSegment(sketch, "E788", {"start": v(-3.11, -241.6) * mm, "end": v(-3.5, -241.65) * mm});
            skLineSegment(sketch, "E789", {"start": v(-3.5, -241.65) * mm, "end": v(-3.89, -241.6) * mm});
            skLineSegment(sketch, "E790", {"start": v(-3.89, -241.6) * mm, "end": v(-4.25, -241.45) * mm});
            skLineSegment(sketch, "E791", {"start": v(-4.25, -241.45) * mm, "end": v(-4.56, -241.21) * mm});
            skLineSegment(sketch, "E792", {"start": v(-4.56, -241.21) * mm, "end": v(-4.8, -240.9) * mm});
            skLineSegment(sketch, "E793", {"start": v(-4.8, -240.9) * mm, "end": v(-4.95, -240.54) * mm});
            skLineSegment(sketch, "E794", {"start": v(-4.95, -240.54) * mm, "end": v(-5, -240.15) * mm});
            skLineSegment(sketch, "E795", {"start": v(-5, -240.15) * mm, "end": v(-4.95, -239.76) * mm});
            skLineSegment(sketch, "E796", {"start": v(-4.95, -239.76) * mm, "end": v(-4.8, -239.4) * mm});
            skLineSegment(sketch, "E797", {"start": v(-4.8, -239.4) * mm, "end": v(-4.56, -239.09) * mm});
            skLineSegment(sketch, "E798", {"start": v(-4.56, -239.09) * mm, "end": v(-4.25, -238.85) * mm});
            skLineSegment(sketch, "E799", {"start": v(-4.25, -238.85) * mm, "end": v(-3.89, -238.7) * mm});
            skLineSegment(sketch, "E800", {"start": v(-3.89, -238.7) * mm, "end": v(-3.5, -238.65) * mm});
            skLineSegment(sketch, "E801", {"start": v(-3.5, -238.65) * mm, "end": v(-3.11, -238.7) * mm});
            skLineSegment(sketch, "E802", {"start": v(-3.11, -238.7) * mm, "end": v(-2.75, -238.85) * mm});
            skLineSegment(sketch, "E803", {"start": v(-2.75, -238.85) * mm, "end": v(-2.44, -239.09) * mm});
            skLineSegment(sketch, "E804", {"start": v(-2.44, -239.09) * mm, "end": v(-2.2, -239.4) * mm});
            skLineSegment(sketch, "E805", {"start": v(-33.5, -243.15) * mm, "end": v(-33.5, -237.15) * mm});
            skLineSegment(sketch, "E806", {"start": v(-166.5, -237.15) * mm, "end": v(-166.5, -243.15) * mm});
            skLineSegment(sketch, "E807", {"start": v(-176.5, -237.15) * mm, "end": v(-166.5, -237.15) * mm});
            skLineSegment(sketch, "E808", {"start": v(-145.05, -240.54) * mm, "end": v(-145.2, -240.9) * mm});
            skLineSegment(sketch, "E809", {"start": v(-145.2, -240.9) * mm, "end": v(-145.44, -241.21) * mm});
            skLineSegment(sketch, "E810", {"start": v(-145.44, -241.21) * mm, "end": v(-145.75, -241.45) * mm});
            skLineSegment(sketch, "E811", {"start": v(-145.75, -241.45) * mm, "end": v(-146.11, -241.6) * mm});
            skLineSegment(sketch, "E812", {"start": v(-146.11, -241.6) * mm, "end": v(-146.5, -241.65) * mm});
            skLineSegment(sketch, "E813", {"start": v(-146.5, -241.65) * mm, "end": v(-146.89, -241.6) * mm});
            skLineSegment(sketch, "E814", {"start": v(-146.89, -241.6) * mm, "end": v(-147.25, -241.45) * mm});
            skLineSegment(sketch, "E815", {"start": v(-147.25, -241.45) * mm, "end": v(-147.56, -241.21) * mm});
            skLineSegment(sketch, "E816", {"start": v(-147.56, -241.21) * mm, "end": v(-147.8, -240.9) * mm});
            skLineSegment(sketch, "E817", {"start": v(-147.8, -240.9) * mm, "end": v(-147.95, -240.54) * mm});
            skLineSegment(sketch, "E818", {"start": v(-147.95, -240.54) * mm, "end": v(-148, -240.15) * mm});
            skLineSegment(sketch, "E819", {"start": v(-148, -240.15) * mm, "end": v(-147.95, -239.76) * mm});
            skLineSegment(sketch, "E820", {"start": v(-147.95, -239.76) * mm, "end": v(-147.8, -239.4) * mm});
            skLineSegment(sketch, "E821", {"start": v(-147.8, -239.4) * mm, "end": v(-147.56, -239.09) * mm});
            skLineSegment(sketch, "E822", {"start": v(-147.56, -239.09) * mm, "end": v(-147.25, -238.85) * mm});
            skLineSegment(sketch, "E823", {"start": v(-147.25, -238.85) * mm, "end": v(-146.89, -238.7) * mm});
            skLineSegment(sketch, "E824", {"start": v(-146.89, -238.7) * mm, "end": v(-146.5, -238.65) * mm});
            skLineSegment(sketch, "E825", {"start": v(-146.5, -238.65) * mm, "end": v(-146.11, -238.7) * mm});
            skLineSegment(sketch, "E826", {"start": v(-146.11, -238.7) * mm, "end": v(-145.75, -238.85) * mm});
            skLineSegment(sketch, "E827", {"start": v(-145.75, -238.85) * mm, "end": v(-145.44, -239.09) * mm});
            skLineSegment(sketch, "E828", {"start": v(-145.44, -239.09) * mm, "end": v(-145.2, -239.4) * mm});
            skLineSegment(sketch, "E829", {"start": v(-145.2, -239.4) * mm, "end": v(-145.05, -239.76) * mm});
            skLineSegment(sketch, "E830", {"start": v(-145.05, -239.76) * mm, "end": v(-145, -240.15) * mm});
            skLineSegment(sketch, "E831", {"start": v(-145, -240.15) * mm, "end": v(-145.05, -240.54) * mm});
            skLineSegment(sketch, "E832", {"start": v(-116.5, -237.15) * mm, "end": v(-116.5, -243.15) * mm});
            skLineSegment(sketch, "E833", {"start": v(-116.5, -237.15) * mm, "end": v(-126.5, -237.15) * mm});
            skLineSegment(sketch, "E834", {"start": v(-126.5, -243.15) * mm, "end": v(-116.5, -243.15) * mm});
            skLineSegment(sketch, "E835", {"start": v(-200.5, -242.15) * mm, "end": v(-200.3, -243.7) * mm});
            skLineSegment(sketch, "E836", {"start": v(-200.3, -243.7) * mm, "end": v(-199.7, -245.15) * mm});
            skLineSegment(sketch, "E837", {"start": v(-199.7, -245.15) * mm, "end": v(-198.74, -246.4) * mm});
            skLineSegment(sketch, "E838", {"start": v(-198.74, -246.4) * mm, "end": v(-197.5, -247.35) * mm});
            skLineSegment(sketch, "E839", {"start": v(-197.5, -247.35) * mm, "end": v(-196.05, -247.95) * mm});
            skLineSegment(sketch, "E840", {"start": v(-196.05, -247.95) * mm, "end": v(-194.5, -248.15) * mm});
            skLineSegment(sketch, "E841", {"start": v(-194.5, -248.15) * mm, "end": v(183.5, -248.15) * mm});
            skArc(sketch, "E842", {"start": v(183.5, -248.15) * mm, "mid": v(187.74, -246.4) * mm, "end": v(189.5, -242.15) * mm});
            skLineSegment(sketch, "E843", {"start": v(183.5, 248.15) * mm, "end": v(185.05, 247.95) * mm});
            skLineSegment(sketch, "E844", {"start": v(185.05, 247.95) * mm, "end": v(186.5, 247.35) * mm});
            skLineSegment(sketch, "E845", {"start": v(186.5, 247.35) * mm, "end": v(187.74, 246.4) * mm});
            skLineSegment(sketch, "E846", {"start": v(187.74, 246.4) * mm, "end": v(188.7, 245.15) * mm});
            skLineSegment(sketch, "E847", {"start": v(188.7, 245.15) * mm, "end": v(189.3, 243.7) * mm});
            skLineSegment(sketch, "E848", {"start": v(189.3, 243.7) * mm, "end": v(189.5, 242.15) * mm});
            skLineSegment(sketch, "E849", {"start": v(-142.64, 129.15) * mm, "end": v(-142.4, 130.5) * mm});
            skLineSegment(sketch, "E850", {"start": v(-142.4, 130.5) * mm, "end": v(-142, 131.8) * mm});
            skLineSegment(sketch, "E851", {"start": v(-142, 131.8) * mm, "end": v(-141.45, 133.06) * mm});
            skLineSegment(sketch, "E852", {"start": v(-141.45, 133.06) * mm, "end": v(-140.75, 134.23) * mm});
            skLineSegment(sketch, "E853", {"start": v(-140.75, 134.23) * mm, "end": v(-139.9, 135.31) * mm});
            skLineSegment(sketch, "E854", {"start": v(-139.9, 135.31) * mm, "end": v(-138.94, 136.29) * mm});
            skLineSegment(sketch, "E855", {"start": v(-138.94, 136.29) * mm, "end": v(-137.87, 137.13) * mm});
            skLineSegment(sketch, "E856", {"start": v(-137.87, 137.13) * mm, "end": v(-136.7, 137.85) * mm});
            skLineSegment(sketch, "E857", {"start": v(-136.7, 137.85) * mm, "end": v(-135.45, 138.4) * mm});
            skLineSegment(sketch, "E858", {"start": v(-135.45, 138.4) * mm, "end": v(-134.15, 138.82) * mm});
            skLineSegment(sketch, "E859", {"start": v(-134.15, 138.82) * mm, "end": v(-132.8, 139.07) * mm});
            skLineSegment(sketch, "E860", {"start": v(-132.8, 139.07) * mm, "end": v(-131.44, 139.15) * mm});
            skLineSegment(sketch, "E861", {"start": v(16.5, -243.15) * mm, "end": v(16.5, -237.15) * mm});
            skLineSegment(sketch, "E862", {"start": v(-126.5, -237.15) * mm, "end": v(-126.5, -243.15) * mm});
            skLineSegment(sketch, "E863", {"start": v(-166.5, -243.15) * mm, "end": v(-176.5, -243.15) * mm});
            skLineSegment(sketch, "E864", {"start": v(-176.5, -243.15) * mm, "end": v(-176.5, -237.15) * mm});
            skLineSegment(sketch, "E865", {"start": v(-189.5, -94.05) * mm, "end": v(-189.5, -84.05) * mm});
            skLineSegment(sketch, "E866", {"start": v(-195.5, -94.05) * mm, "end": v(-189.5, -94.05) * mm});
            skLineSegment(sketch, "E867", {"start": v(89.5, -218.15) * mm, "end": v(-151.5, -218.15) * mm});
            skLineSegment(sketch, "E868", {"start": v(99.5, 129.15) * mm, "end": v(99.5, -208.15) * mm});
            skArc(sketch, "E869", {"start": v(99.5, 129.15) * mm, "mid": v(96.57, 136.22) * mm, "end": v(89.5, 139.15) * mm});
            skLineSegment(sketch, "E870", {"start": v(-189.5, -84.05) * mm, "end": v(-195.5, -84.05) * mm});
            skLineSegment(sketch, "E871", {"start": v(109.5, -243.15) * mm, "end": v(119.5, -243.15) * mm});
            skLineSegment(sketch, "E872", {"start": v(159.5, -243.15) * mm, "end": v(159.5, -237.15) * mm});
            skLineSegment(sketch, "E873", {"start": v(169.5, -243.15) * mm, "end": v(169.5, -237.15) * mm});
            skLineSegment(sketch, "E874", {"start": v(159.5, -243.15) * mm, "end": v(169.5, -243.15) * mm});
            skLineSegment(sketch, "E875", {"start": v(-131.44, 139.15) * mm, "end": v(89.5, 139.15) * mm});
            skLineSegment(sketch, "E876", {"start": v(-161.5, -198.15) * mm, "end": v(-161.5, -208.15) * mm});
            skLineSegment(sketch, "E877", {"start": v(-161.5, -208.15) * mm, "end": v(-161.41, -209.46) * mm});
            skLineSegment(sketch, "E878", {"start": v(-161.41, -209.46) * mm, "end": v(-161.16, -210.74) * mm});
            skLineSegment(sketch, "E879", {"start": v(-161.16, -210.74) * mm, "end": v(-160.74, -211.98) * mm});
            skLineSegment(sketch, "E880", {"start": v(-160.74, -211.98) * mm, "end": v(-160.16, -213.15) * mm});
            skLineSegment(sketch, "E881", {"start": v(-160.16, -213.15) * mm, "end": v(-159.43, -214.24) * mm});
            skLineSegment(sketch, "E882", {"start": v(-159.43, -214.24) * mm, "end": v(-158.57, -215.22) * mm});
            skLineSegment(sketch, "E883", {"start": v(-158.57, -215.22) * mm, "end": v(-157.59, -216.08) * mm});
            skLineSegment(sketch, "E884", {"start": v(-157.59, -216.08) * mm, "end": v(-156.5, -216.81) * mm});
            skLineSegment(sketch, "E885", {"start": v(-156.5, -216.81) * mm, "end": v(-155.33, -217.39) * mm});
            skLineSegment(sketch, "E886", {"start": v(-155.33, -217.39) * mm, "end": v(-154.09, -217.8) * mm});
            skLineSegment(sketch, "E887", {"start": v(-154.09, -217.8) * mm, "end": v(-152.8, -218.06) * mm});
            skLineSegment(sketch, "E888", {"start": v(-152.8, -218.06) * mm, "end": v(-151.5, -218.15) * mm});
            skLineSegment(sketch, "E889", {"start": v(-195.5, -162.15) * mm, "end": v(-195.5, -172.15) * mm});
            skLineSegment(sketch, "E890", {"start": v(-189.5, -172.15) * mm, "end": v(-189.5, -162.15) * mm});
            skLineSegment(sketch, "E891", {"start": v(-189.5, -162.15) * mm, "end": v(-195.5, -162.15) * mm});
            skLineSegment(sketch, "E892", {"start": v(-195.5, -172.15) * mm, "end": v(-189.5, -172.15) * mm});
            skLineSegment(sketch, "E893", {"start": v(-189.5, -222.15) * mm, "end": v(-189.5, -212.15) * mm});
            skLineSegment(sketch, "E894", {"start": v(-195.5, -212.15) * mm, "end": v(-195.5, -222.15) * mm});
            skLineSegment(sketch, "E895", {"start": v(-189.5, -212.15) * mm, "end": v(-195.5, -212.15) * mm});
            skLineSegment(sketch, "E896", {"start": v(-23.5, -243.15) * mm, "end": v(-23.5, -237.15) * mm});
            skLineSegment(sketch, "E897", {"start": v(-23.5, -243.15) * mm, "end": v(-33.5, -243.15) * mm});
            skLineSegment(sketch, "E898", {"start": v(26.5, -237.15) * mm, "end": v(26.5, -243.15) * mm});
            skLineSegment(sketch, "E899", {"start": v(26.5, -243.15) * mm, "end": v(16.5, -243.15) * mm});
            skLineSegment(sketch, "E900", {"start": v(-23.5, -237.15) * mm, "end": v(-33.5, -237.15) * mm});
            skLineSegment(sketch, "E901", {"start": v(26.5, -237.15) * mm, "end": v(16.5, -237.15) * mm});
            skArc(sketch, "E902", {"start": v(-194.5, 248.15) * mm, "mid": v(-198.74, 246.4) * mm, "end": v(-200.5, 242.15) * mm});
            skCircle(sketch, "E903", {"center": v(179.5, -227.5) * mm, "radius": 1.5 * mm});
            skLineSegment(sketch, "E904", {"start": v(183.5, 248.15) * mm, "end": v(-194.5, 248.15) * mm});
            skLineSegment(sketch, "E905", {"start": v(-200.5, 242.15) * mm, "end": v(-200.5, -242.15) * mm});
            skLineSegment(sketch, "E906", {"start": v(-189.5, 222.15) * mm, "end": v(-195.5, 222.15) * mm});
            skLineSegment(sketch, "E907", {"start": v(-195.5, 212.15) * mm, "end": v(-189.5, 212.15) * mm});
            skLineSegment(sketch, "E908", {"start": v(-195.5, 222.15) * mm, "end": v(-195.5, 212.15) * mm});
            skLineSegment(sketch, "E909", {"start": v(104.5, 162.15) * mm, "end": v(104.5, 172.15) * mm});
            skLineSegment(sketch, "E910", {"start": v(110.5, 172.15) * mm, "end": v(110.5, 162.15) * mm});
            skLineSegment(sketch, "E911", {"start": v(-23.5, 243.15) * mm, "end": v(-23.5, 237.15) * mm});
            skLineSegment(sketch, "E912", {"start": v(-23.5, 237.15) * mm, "end": v(-33.5, 237.15) * mm});
            skLineSegment(sketch, "E913", {"start": v(-33.5, 237.15) * mm, "end": v(-33.5, 243.15) * mm});
            skLineSegment(sketch, "E914", {"start": v(-23.5, 243.15) * mm, "end": v(-33.5, 243.15) * mm});
            skLineSegment(sketch, "E915", {"start": v(169.5, -237.15) * mm, "end": v(159.5, -237.15) * mm});
            skLineSegment(sketch, "E916", {"start": v(104.5, 84.05) * mm, "end": v(110.5, 84.05) * mm});
            skLineSegment(sketch, "E917", {"start": v(104.5, 94.05) * mm, "end": v(104.5, 84.05) * mm});
            skLineSegment(sketch, "E918", {"start": v(110.5, -44.05) * mm, "end": v(104.5, -44.05) * mm});
            skLineSegment(sketch, "E919", {"start": v(104.5, -44.05) * mm, "end": v(104.5, -34.05) * mm});
            skLineSegment(sketch, "E920", {"start": v(104.5, -34.05) * mm, "end": v(110.5, -34.05) * mm});
            skLineSegment(sketch, "E921", {"start": v(110.5, -34.05) * mm, "end": v(110.5, -44.05) * mm});
            skLineSegment(sketch, "E922", {"start": v(150.6, -234.15) * mm, "end": v(169.6, -234.15) * mm});
            skLineSegment(sketch, "E923", {"start": v(119.5, 237.15) * mm, "end": v(109.5, 237.15) * mm});
            skLineSegment(sketch, "E924", {"start": v(-116.5, 243.15) * mm, "end": v(-126.5, 243.15) * mm});
            skLineSegment(sketch, "E925", {"start": v(-195.5, 44.05) * mm, "end": v(-195.5, 34.05) * mm});
            skLineSegment(sketch, "E926", {"start": v(-189.5, 172.15) * mm, "end": v(-195.5, 172.15) * mm});
            skLineSegment(sketch, "E927", {"start": v(-189.5, 162.15) * mm, "end": v(-189.5, 172.15) * mm});
            skLineSegment(sketch, "E928", {"start": v(-195.5, 162.15) * mm, "end": v(-189.5, 162.15) * mm});
            skLineSegment(sketch, "E929", {"start": v(-195.5, 172.15) * mm, "end": v(-195.5, 162.15) * mm});
            skLineSegment(sketch, "E930", {"start": v(119.5, -243.15) * mm, "end": v(119.5, -237.15) * mm});
            skLineSegment(sketch, "E931", {"start": v(109.5, -243.15) * mm, "end": v(109.5, -237.15) * mm});
            skLineSegment(sketch, "E932", {"start": v(119.5, -237.15) * mm, "end": v(109.5, -237.15) * mm});
            skCircle(sketch, "E933", {"center": v(3.03, 190.6) * mm, "radius": 1.5 * mm});
            skLineSegment(sketch, "E934", {"start": v(71.73, 191.35) * mm, "end": v(71.97, 191.66) * mm});
            skLineSegment(sketch, "E935", {"start": v(71.97, 191.66) * mm, "end": v(72.28, 191.9) * mm});
            skLineSegment(sketch, "E936", {"start": v(72.28, 191.9) * mm, "end": v(72.64, 192.05) * mm});
            skLineSegment(sketch, "E937", {"start": v(72.64, 192.05) * mm, "end": v(73.03, 192.1) * mm});
            skLineSegment(sketch, "E938", {"start": v(73.03, 192.1) * mm, "end": v(73.42, 192.05) * mm});
            skLineSegment(sketch, "E939", {"start": v(73.42, 192.05) * mm, "end": v(73.78, 191.9) * mm});
            skLineSegment(sketch, "E940", {"start": v(73.78, 191.9) * mm, "end": v(74.1, 191.66) * mm});
            skLineSegment(sketch, "E941", {"start": v(74.1, 191.66) * mm, "end": v(74.33, 191.35) * mm});
            skLineSegment(sketch, "E942", {"start": v(74.33, 191.35) * mm, "end": v(74.48, 190.99) * mm});
            skLineSegment(sketch, "E943", {"start": v(74.48, 190.99) * mm, "end": v(74.53, 190.6) * mm});
            skLineSegment(sketch, "E944", {"start": v(74.53, 190.6) * mm, "end": v(74.48, 190.21) * mm});
            skLineSegment(sketch, "E945", {"start": v(74.48, 190.21) * mm, "end": v(74.33, 189.85) * mm});
            skLineSegment(sketch, "E946", {"start": v(74.33, 189.85) * mm, "end": v(74.1, 189.54) * mm});
            skLineSegment(sketch, "E947", {"start": v(74.1, 189.54) * mm, "end": v(73.78, 189.3) * mm});
            skLineSegment(sketch, "E948", {"start": v(73.78, 189.3) * mm, "end": v(73.42, 189.15) * mm});
            skLineSegment(sketch, "E949", {"start": v(73.42, 189.15) * mm, "end": v(73.03, 189.1) * mm});
            skLineSegment(sketch, "E950", {"start": v(73.03, 189.1) * mm, "end": v(72.64, 189.15) * mm});
            skLineSegment(sketch, "E951", {"start": v(72.64, 189.15) * mm, "end": v(72.28, 189.3) * mm});
            skLineSegment(sketch, "E952", {"start": v(72.28, 189.3) * mm, "end": v(71.97, 189.54) * mm});
            skLineSegment(sketch, "E953", {"start": v(71.97, 189.54) * mm, "end": v(71.73, 189.85) * mm});
            skLineSegment(sketch, "E954", {"start": v(71.73, 189.85) * mm, "end": v(71.58, 190.21) * mm});
            skLineSegment(sketch, "E955", {"start": v(71.58, 190.21) * mm, "end": v(71.53, 190.6) * mm});
            skLineSegment(sketch, "E956", {"start": v(71.53, 190.6) * mm, "end": v(71.58, 190.99) * mm});
            skLineSegment(sketch, "E957", {"start": v(71.58, 190.99) * mm, "end": v(71.73, 191.35) * mm});
            skPoint(sketch, "E958.0", {"position": v(26.5, 237.15) * mm});
            skSolve(sketch);
        }
        {
            var Q0;
            Q0 = qSketchRegion(id + "F8", true);
            extrude(context, id + "F9", {"entities" : qUnion([Q0]), "depth" : 6 * mm, "offsetDistance" : 25 * mm});
        }
        {
            var Q0;
            Q0=qCreatedBy(id+"F7.planeOp",FACE);
            var sketch = newSketch(context, id + "F10", { "sketchPlane" : qUnion([Q0])});
            skPoint(sketch, "E959.0", {"position": v(-26.5, 237.15) * mm});
            skLineSegment(sketch, "E960.MirrorCS", {"start": v(-139.89, 238.7) * mm, "end": v(-140.25, 238.85) * mm});
            skLineSegment(sketch, "E961.MirrorCS", {"start": v(-140.25, 238.85) * mm, "end": v(-140.56, 239.09) * mm});
            skLineSegment(sketch, "E962.MirrorCS", {"start": v(-140.56, 239.09) * mm, "end": v(-140.8, 239.4) * mm});
            skLineSegment(sketch, "E963.MirrorCS", {"start": v(-140.8, 239.4) * mm, "end": v(-140.95, 239.76) * mm});
            skLineSegment(sketch, "E964.MirrorCS", {"start": v(-140.95, 239.76) * mm, "end": v(-141, 240.15) * mm});
            skLineSegment(sketch, "E965.MirrorCS", {"start": v(-141, 240.15) * mm, "end": v(-140.95, 240.54) * mm});
            skLineSegment(sketch, "E966.MirrorCS", {"start": v(-140.95, 240.54) * mm, "end": v(-140.8, 240.9) * mm});
            skLineSegment(sketch, "E967.MirrorCS", {"start": v(4.24, 241.45) * mm, "end": v(4.56, 241.21) * mm});
            skLineSegment(sketch, "E968.MirrorCS", {"start": v(-140.8, 240.9) * mm, "end": v(-140.56, 241.21) * mm});
            skLineSegment(sketch, "E969.MirrorCS", {"start": v(2, 240.15) * mm, "end": v(2.05, 240.54) * mm});
            skLineSegment(sketch, "E970.MirrorCS", {"start": v(-140.56, 241.21) * mm, "end": v(-140.25, 241.45) * mm});
            skLineSegment(sketch, "E971.MirrorCS", {"start": v(2.05, 240.54) * mm, "end": v(2.2, 240.9) * mm});
            skLineSegment(sketch, "E972.MirrorCS", {"start": v(-138.05, 240.54) * mm, "end": v(-138, 240.15) * mm});
            skLineSegment(sketch, "E973.MirrorCS", {"start": v(2.2, 240.9) * mm, "end": v(2.43, 241.21) * mm});
            skLineSegment(sketch, "E974.MirrorCS", {"start": v(-140.25, 241.45) * mm, "end": v(-139.89, 241.6) * mm});
            skLineSegment(sketch, "E975.MirrorCS", {"start": v(2.43, 241.21) * mm, "end": v(2.74, 241.45) * mm});
            skLineSegment(sketch, "E976.MirrorCS", {"start": v(193.25, 190.85) * mm, "end": v(193.56, 191.09) * mm});
            skLineSegment(sketch, "E977.MirrorCS", {"start": v(-138, 240.15) * mm, "end": v(-138.05, 239.76) * mm});
            skLineSegment(sketch, "E978.MirrorCS", {"start": v(2.74, 241.45) * mm, "end": v(3.1, 241.6) * mm});
            skLineSegment(sketch, "E979.MirrorCS", {"start": v(191.05, 191.76) * mm, "end": v(191.2, 191.4) * mm});
            skLineSegment(sketch, "E980.MirrorCS", {"start": v(-139.89, 241.6) * mm, "end": v(-139.5, 241.65) * mm});
            skLineSegment(sketch, "E981.MirrorCS", {"start": v(3.1, 241.6) * mm, "end": v(3.5, 241.65) * mm});
            skLineSegment(sketch, "E982.MirrorCS", {"start": v(193.56, 191.09) * mm, "end": v(193.8, 191.4) * mm});
            skLineSegment(sketch, "E983.MirrorCS", {"start": v(192.89, 62.6) * mm, "end": v(193.25, 62.75) * mm});
            skLineSegment(sketch, "E984.MirrorCS", {"start": v(-138.05, 239.76) * mm, "end": v(-138.2, 239.4) * mm});
            skLineSegment(sketch, "E985.MirrorCS", {"start": v(3.5, 241.65) * mm, "end": v(3.88, 241.6) * mm});
            skLineSegment(sketch, "E986.MirrorCS", {"start": v(191.2, 191.4) * mm, "end": v(191.44, 191.09) * mm});
            skLineSegment(sketch, "E987.MirrorCS", {"start": v(193.25, 62.75) * mm, "end": v(193.56, 62.99) * mm});
            skLineSegment(sketch, "E988.MirrorCS", {"start": v(2, -240.15) * mm, "end": v(2.05, -239.76) * mm});
            skLineSegment(sketch, "E989.MirrorCS", {"start": v(-139.5, 241.65) * mm, "end": v(-139.11, 241.6) * mm});
            skLineSegment(sketch, "E990.MirrorCS", {"start": v(4.56, 239.09) * mm, "end": v(4.24, 238.85) * mm});
            skLineSegment(sketch, "E991.MirrorCS", {"start": v(193.56, 62.99) * mm, "end": v(193.8, 63.3) * mm});
            skLineSegment(sketch, "E992.MirrorCS", {"start": v(193.8, 191.4) * mm, "end": v(193.95, 191.76) * mm});
            skLineSegment(sketch, "E993.MirrorCS", {"start": v(193.25, 65.35) * mm, "end": v(192.89, 65.5) * mm});
            skLineSegment(sketch, "E994.MirrorCS", {"start": v(4.24, -238.85) * mm, "end": v(4.55, -239.09) * mm});
            skLineSegment(sketch, "E995.MirrorCS", {"start": v(-138.2, 239.4) * mm, "end": v(-138.44, 239.09) * mm});
            skLineSegment(sketch, "E996.MirrorCS", {"start": v(3.88, 241.6) * mm, "end": v(4.24, 241.45) * mm});
            skLineSegment(sketch, "E997.MirrorCS", {"start": v(193.8, 192.9) * mm, "end": v(193.56, 193.21) * mm});
            skLineSegment(sketch, "E998.MirrorCS", {"start": v(193.8, 63.3) * mm, "end": v(193.95, 63.66) * mm});
            skLineSegment(sketch, "E999.MirrorCS", {"start": v(191.44, 191.09) * mm, "end": v(191.75, 190.85) * mm});
            skLineSegment(sketch, "E1000.MirrorCS", {"start": v(192.89, 65.5) * mm, "end": v(192.5, 65.55) * mm});
            skLineSegment(sketch, "E1001.MirrorCS", {"start": v(2.05, -239.76) * mm, "end": v(2.2, -239.4) * mm});
            skLineSegment(sketch, "E1002.MirrorCS", {"start": v(-139.11, 241.6) * mm, "end": v(-138.75, 241.45) * mm});
            skLineSegment(sketch, "E1003.MirrorCS", {"start": v(2.2, -239.4) * mm, "end": v(2.43, -239.09) * mm});
            skLineSegment(sketch, "E1004.MirrorCS", {"start": v(4.24, 238.85) * mm, "end": v(3.88, 238.7) * mm});
            skLineSegment(sketch, "E1005.MirrorCS", {"start": v(193.56, 193.21) * mm, "end": v(193.25, 193.45) * mm});
            skLineSegment(sketch, "E1006.MirrorCS", {"start": v(193.95, 63.66) * mm, "end": v(194, 64.05) * mm});
            skLineSegment(sketch, "E1007.MirrorCS", {"start": v(192.5, 65.55) * mm, "end": v(192.11, 65.5) * mm});
            skLineSegment(sketch, "E1008.MirrorCS", {"start": v(193.95, 191.76) * mm, "end": v(194, 192.15) * mm});
            skLineSegment(sketch, "E1009.MirrorCS", {"start": v(-138.44, 239.09) * mm, "end": v(-138.75, 238.85) * mm});
            skLineSegment(sketch, "E1010.MirrorCS", {"start": v(2.43, -239.09) * mm, "end": v(2.74, -238.85) * mm});
            skLineSegment(sketch, "E1011.MirrorCS", {"start": v(3.88, 238.7) * mm, "end": v(3.5, 238.65) * mm});
            skLineSegment(sketch, "E1012.MirrorCS", {"start": v(193.25, 193.45) * mm, "end": v(192.89, 193.6) * mm});
            skLineSegment(sketch, "E1013.MirrorCS", {"start": v(4.55, -241.21) * mm, "end": v(4.24, -241.45) * mm});
            skLineSegment(sketch, "E1014.MirrorCS", {"start": v(194, 64.05) * mm, "end": v(193.95, 64.44) * mm});
            skLineSegment(sketch, "E1015.MirrorCS", {"start": v(192.11, 65.5) * mm, "end": v(191.75, 65.35) * mm});
            skLineSegment(sketch, "E1016.MirrorCS", {"start": v(191.75, 190.85) * mm, "end": v(192.11, 190.7) * mm});
            skLineSegment(sketch, "E1017.MirrorCS", {"start": v(-138.75, 241.45) * mm, "end": v(-138.44, 241.21) * mm});
            skLineSegment(sketch, "E1018.MirrorCS", {"start": v(2.74, -238.85) * mm, "end": v(3.1, -238.7) * mm});
            skLineSegment(sketch, "E1019.MirrorCS", {"start": v(191.05, 63.66) * mm, "end": v(191.2, 63.3) * mm});
            skLineSegment(sketch, "E1020.MirrorCS", {"start": v(3.5, 238.65) * mm, "end": v(3.1, 238.7) * mm});
            skLineSegment(sketch, "E1021.MirrorCS", {"start": v(192.89, 193.6) * mm, "end": v(192.5, 193.65) * mm});
            skLineSegment(sketch, "E1022.MirrorCS", {"start": v(4.24, -241.45) * mm, "end": v(3.88, -241.6) * mm});
            skLineSegment(sketch, "E1023.MirrorCS", {"start": v(191.75, 65.35) * mm, "end": v(191.44, 65.11) * mm});
            skLineSegment(sketch, "E1024.MirrorCS", {"start": v(194, 192.15) * mm, "end": v(193.95, 192.54) * mm});
            skLineSegment(sketch, "E1025.MirrorCS", {"start": v(4.56, 241.21) * mm, "end": v(4.8, 240.9) * mm});
            skLineSegment(sketch, "E1026.MirrorCS", {"start": v(4.55, -239.09) * mm, "end": v(4.8, -239.4) * mm});
            skLineSegment(sketch, "E1027.MirrorCS", {"start": v(3.1, -238.7) * mm, "end": v(3.5, -238.65) * mm});
            skLineSegment(sketch, "E1028.MirrorCS", {"start": v(-138.75, 238.85) * mm, "end": v(-139.11, 238.7) * mm});
            skLineSegment(sketch, "E1029.MirrorCS", {"start": v(191.2, 63.3) * mm, "end": v(191.44, 62.99) * mm});
            skLineSegment(sketch, "E1030.MirrorCS", {"start": v(3.1, 238.7) * mm, "end": v(2.74, 238.85) * mm});
            skLineSegment(sketch, "E1031.MirrorCS", {"start": v(192.5, 193.65) * mm, "end": v(192.11, 193.6) * mm});
            skLineSegment(sketch, "E1032.MirrorCS", {"start": v(3.88, -241.6) * mm, "end": v(3.5, -241.65) * mm});
            skLineSegment(sketch, "E1033.MirrorCS", {"start": v(193.95, 64.44) * mm, "end": v(193.8, 64.8) * mm});
            skLineSegment(sketch, "E1034.MirrorCS", {"start": v(192.11, 190.7) * mm, "end": v(192.5, 190.65) * mm});
            skLineSegment(sketch, "E1035.MirrorCS", {"start": v(4.8, 240.9) * mm, "end": v(4.94, 240.54) * mm});
            skLineSegment(sketch, "E1036.MirrorCS", {"start": v(4.8, -239.4) * mm, "end": v(4.94, -239.76) * mm});
            skLineSegment(sketch, "E1037.MirrorCS", {"start": v(3.5, -238.65) * mm, "end": v(3.88, -238.7) * mm});
            skLineSegment(sketch, "E1038.MirrorCS", {"start": v(-138.44, 241.21) * mm, "end": v(-138.2, 240.9) * mm});
            skLineSegment(sketch, "E1039.MirrorCS", {"start": v(191.44, 62.99) * mm, "end": v(191.75, 62.75) * mm});
            skLineSegment(sketch, "E1040.MirrorCS", {"start": v(2.74, 238.85) * mm, "end": v(2.43, 239.09) * mm});
            skLineSegment(sketch, "E1041.MirrorCS", {"start": v(192.11, 193.6) * mm, "end": v(191.75, 193.45) * mm});
            skLineSegment(sketch, "E1042.MirrorCS", {"start": v(3.5, -241.65) * mm, "end": v(3.1, -241.6) * mm});
            skLineSegment(sketch, "E1043.MirrorCS", {"start": v(191.44, 65.11) * mm, "end": v(191.2, 64.8) * mm});
            skLineSegment(sketch, "E1044.MirrorCS", {"start": v(193.95, 192.54) * mm, "end": v(193.8, 192.9) * mm});
            skLineSegment(sketch, "E1045.MirrorCS", {"start": v(4.94, -239.76) * mm, "end": v(5, -240.15) * mm});
            skLineSegment(sketch, "E1046.MirrorCS", {"start": v(4.94, 240.54) * mm, "end": v(5, 240.15) * mm});
            skLineSegment(sketch, "E1047.MirrorCS", {"start": v(2.2, -240.9) * mm, "end": v(2.05, -240.54) * mm});
            skLineSegment(sketch, "E1048.MirrorCS", {"start": v(-139.11, 238.7) * mm, "end": v(-139.5, 238.65) * mm});
            skLineSegment(sketch, "E1049.MirrorCS", {"start": v(191.75, 62.75) * mm, "end": v(192.11, 62.6) * mm});
            skLineSegment(sketch, "E1050.MirrorCS", {"start": v(2.43, 239.09) * mm, "end": v(2.2, 239.4) * mm});
            skLineSegment(sketch, "E1051.MirrorCS", {"start": v(191.75, 193.45) * mm, "end": v(191.44, 193.21) * mm});
            skLineSegment(sketch, "E1052.MirrorCS", {"start": v(3.1, -241.6) * mm, "end": v(2.74, -241.45) * mm});
            skLineSegment(sketch, "E1053.MirrorCS", {"start": v(193.8, 64.8) * mm, "end": v(193.56, 65.11) * mm});
            skLineSegment(sketch, "E1054.MirrorCS", {"start": v(192.5, 190.65) * mm, "end": v(192.89, 190.7) * mm});
            skLineSegment(sketch, "E1055.MirrorCS", {"start": v(5, -240.15) * mm, "end": v(4.94, -240.54) * mm});
            skLineSegment(sketch, "E1056.MirrorCS", {"start": v(5, 240.15) * mm, "end": v(4.94, 239.76) * mm});
            skLineSegment(sketch, "E1057.MirrorCS", {"start": v(3.88, -238.7) * mm, "end": v(4.24, -238.85) * mm});
            skLineSegment(sketch, "E1058.MirrorCS", {"start": v(-138.2, 240.9) * mm, "end": v(-138.05, 240.54) * mm});
            skLineSegment(sketch, "E1059.MirrorCS", {"start": v(192.11, 62.6) * mm, "end": v(192.5, 62.55) * mm});
            skLineSegment(sketch, "E1060.MirrorCS", {"start": v(2.2, 239.4) * mm, "end": v(2.05, 239.76) * mm});
            skLineSegment(sketch, "E1061.MirrorCS", {"start": v(191.44, 193.21) * mm, "end": v(191.2, 192.9) * mm});
            skLineSegment(sketch, "E1062.MirrorCS", {"start": v(2.74, -241.45) * mm, "end": v(2.43, -241.21) * mm});
            skLineSegment(sketch, "E1063.MirrorCS", {"start": v(23.5, -243.15) * mm, "end": v(33.5, -243.15) * mm});
            skLineSegment(sketch, "E1064.MirrorCS", {"start": v(189.5, 212.15) * mm, "end": v(195.5, 212.15) * mm});
            skLineSegment(sketch, "E1065.MirrorCS", {"start": v(191.05, 64.44) * mm, "end": v(191, 64.05) * mm});
            skLineSegment(sketch, "E1066.MirrorCS", {"start": v(192.89, 190.7) * mm, "end": v(193.25, 190.85) * mm});
            skLineSegment(sketch, "E1067.MirrorCS", {"start": v(189.5, 222.15) * mm, "end": v(189.5, 212.15) * mm});
            skLineSegment(sketch, "E1068.MirrorCS", {"start": v(191.2, 64.8) * mm, "end": v(191.05, 64.44) * mm});
            skLineSegment(sketch, "E1069.MirrorCS", {"start": v(181.56, 208.79) * mm, "end": v(177.56, 208.77) * mm});
            skLineSegment(sketch, "E1070.MirrorCS", {"start": v(4.94, -240.54) * mm, "end": v(4.8, -240.9) * mm});
            skLineSegment(sketch, "E1071.MirrorCS", {"start": v(4.94, 239.76) * mm, "end": v(4.8, 239.4) * mm});
            skLineSegment(sketch, "E1072.MirrorCS", {"start": v(191, 192.15) * mm, "end": v(191.05, 191.76) * mm});
            skLineSegment(sketch, "E1073.MirrorCS", {"start": v(195.5, 84.05) * mm, "end": v(195.5, 94.05) * mm});
            skLineSegment(sketch, "E1074.MirrorCS", {"start": v(-159.5, 237.15) * mm, "end": v(-159.5, 243.15) * mm});
            skLineSegment(sketch, "E1075.MirrorCS", {"start": v(2.05, -240.54) * mm, "end": v(2, -240.15) * mm});
            skLineSegment(sketch, "E1076.MirrorCS", {"start": v(192.5, 62.55) * mm, "end": v(192.89, 62.6) * mm});
            skLineSegment(sketch, "E1077.MirrorCS", {"start": v(23.5, 243.15) * mm, "end": v(23.5, 237.15) * mm});
            skLineSegment(sketch, "E1078.MirrorCS", {"start": v(2.05, 239.76) * mm, "end": v(2, 240.15) * mm});
            skLineSegment(sketch, "E1079.MirrorCS", {"start": v(-139.5, 238.65) * mm, "end": v(-139.89, 238.7) * mm});
            skLineSegment(sketch, "E1080.MirrorCS", {"start": v(33.5, -243.15) * mm, "end": v(33.5, -237.15) * mm});
            skLineSegment(sketch, "E1081.MirrorCS", {"start": v(189.5, 94.05) * mm, "end": v(189.5, 84.05) * mm});
            skLineSegment(sketch, "E1082.MirrorCS", {"start": v(195.5, 222.15) * mm, "end": v(195.5, 212.15) * mm});
            skLineSegment(sketch, "E1083.MirrorCS", {"start": v(191.2, 192.9) * mm, "end": v(191.05, 192.54) * mm});
            skLineSegment(sketch, "E1084.MirrorCS", {"start": v(2.43, -241.21) * mm, "end": v(2.2, -240.9) * mm});
            skLineSegment(sketch, "E1085.MirrorCS", {"start": v(23.5, -237.15) * mm, "end": v(33.5, -237.15) * mm});
            skLineSegment(sketch, "E1086.MirrorCS", {"start": v(189.5, 84.05) * mm, "end": v(195.5, 84.05) * mm});
            skLineSegment(sketch, "E1087.MirrorCS", {"start": v(-119.5, 243.15) * mm, "end": v(-119.5, 237.15) * mm});
            skLineSegment(sketch, "E1088.MirrorCS", {"start": v(23.5, -243.15) * mm, "end": v(23.5, -237.15) * mm});
            skLineSegment(sketch, "E1089.MirrorCS", {"start": v(195.5, 44.05) * mm, "end": v(189.5, 44.05) * mm});
            skLineSegment(sketch, "E1090.MirrorCS", {"start": v(-16.5, 237.15) * mm, "end": v(-16.5, 243.15) * mm});
            skLineSegment(sketch, "E1091.MirrorCS", {"start": v(181.56, 180.79) * mm, "end": v(181.56, 208.79) * mm});
            skLineSegment(sketch, "E1092.MirrorCS", {"start": v(191, 64.05) * mm, "end": v(191.05, 63.66) * mm});
            skLineSegment(sketch, "E1093.MirrorCS", {"start": v(177.56, 180.77) * mm, "end": v(181.56, 180.79) * mm});
            skLineSegment(sketch, "E1094.MirrorCS", {"start": v(177.56, 208.77) * mm, "end": v(177.56, 180.77) * mm});
            skLineSegment(sketch, "E1095.MirrorCS", {"start": v(195.5, 222.15) * mm, "end": v(189.5, 222.15) * mm});
            skLineSegment(sketch, "E1096.MirrorCS", {"start": v(193.56, 65.11) * mm, "end": v(193.25, 65.35) * mm});
            skLineSegment(sketch, "E1097.MirrorCS", {"start": v(4.8, 239.4) * mm, "end": v(4.56, 239.09) * mm});
            skLineSegment(sketch, "E1098.MirrorCS", {"start": v(4.8, -240.9) * mm, "end": v(4.55, -241.21) * mm});
            skLineSegment(sketch, "E1099.MirrorCS", {"start": v(189.5, 172.15) * mm, "end": v(195.5, 172.15) * mm});
            skLineSegment(sketch, "E1100.MirrorCS", {"start": v(23.5, 237.15) * mm, "end": v(33.5, 237.15) * mm});
            skLineSegment(sketch, "E1101.MirrorCS", {"start": v(-16.5, -243.15) * mm, "end": v(-16.5, -237.15) * mm});
            skLineSegment(sketch, "E1102.MirrorCS", {"start": v(-169.5, 243.15) * mm, "end": v(-159.5, 243.15) * mm});
            skLineSegment(sketch, "E1103.MirrorCS", {"start": v(195.5, 94.05) * mm, "end": v(189.5, 94.05) * mm});
            skLineSegment(sketch, "E1104.MirrorCS", {"start": v(-169.5, 237.15) * mm, "end": v(-159.5, 237.15) * mm});
            skLineSegment(sketch, "E1105.MirrorCS", {"start": v(-106.45, 62.99) * mm, "end": v(-106.76, 62.75) * mm});
            skLineSegment(sketch, "E1106.MirrorCS", {"start": v(23.5, 243.15) * mm, "end": v(33.5, 243.15) * mm});
            skLineSegment(sketch, "E1107.MirrorCS", {"start": v(191.05, 192.54) * mm, "end": v(191, 192.15) * mm});
            skLineSegment(sketch, "E1108.MirrorCS", {"start": v(-108.95, 63.66) * mm, "end": v(-109, 64.05) * mm});
            skLineSegment(sketch, "E1109.MirrorCS", {"start": v(-107.9, -65.5) * mm, "end": v(-108.26, -65.35) * mm});
            skLineSegment(sketch, "E1110.MirrorCS", {"start": v(-106.76, 62.75) * mm, "end": v(-107.12, 62.6) * mm});
            skLineSegment(sketch, "E1111.MirrorCS", {"start": v(-108.26, -65.35) * mm, "end": v(-108.57, -65.11) * mm});
            skLineSegment(sketch, "E1112.MirrorCS", {"start": v(-109, 64.05) * mm, "end": v(-108.95, 64.44) * mm});
            skLineSegment(sketch, "E1113.MirrorCS", {"start": v(-108.57, -65.11) * mm, "end": v(-108.8, -64.8) * mm});
            skLineSegment(sketch, "E1114.MirrorCS", {"start": v(-107.12, 62.6) * mm, "end": v(-107.5, 62.55) * mm});
            skLineSegment(sketch, "E1115.MirrorCS", {"start": v(-108.8, -64.8) * mm, "end": v(-108.95, -64.44) * mm});
            skLineSegment(sketch, "E1116.MirrorCS", {"start": v(-108.95, 64.44) * mm, "end": v(-108.8, 64.8) * mm});
            skLineSegment(sketch, "E1117.MirrorCS", {"start": v(-108.95, -64.44) * mm, "end": v(-109, -64.05) * mm});
            skLineSegment(sketch, "E1118.MirrorCS", {"start": v(-106.76, -62.75) * mm, "end": v(-106.45, -62.99) * mm});
            skLineSegment(sketch, "E1119.MirrorCS", {"start": v(-108.8, 64.8) * mm, "end": v(-108.57, 65.11) * mm});
            skLineSegment(sketch, "E1120.MirrorCS", {"start": v(-107.5, 62.55) * mm, "end": v(-107.9, 62.6) * mm});
            skLineSegment(sketch, "E1121.MirrorCS", {"start": v(-109, -64.05) * mm, "end": v(-108.95, -63.66) * mm});
            skLineSegment(sketch, "E1122.MirrorCS", {"start": v(-106.45, -62.99) * mm, "end": v(-106.2, -63.3) * mm});
            skLineSegment(sketch, "E1123.MirrorCS", {"start": v(-108.57, 65.11) * mm, "end": v(-108.26, 65.35) * mm});
            skLineSegment(sketch, "E1124.MirrorCS", {"start": v(-107.9, 62.6) * mm, "end": v(-108.26, 62.75) * mm});
            skLineSegment(sketch, "E1125.MirrorCS", {"start": v(-106.06, -63.66) * mm, "end": v(-106, -64.05) * mm});
            skLineSegment(sketch, "E1126.MirrorCS", {"start": v(-106.2, -63.3) * mm, "end": v(-106.06, -63.66) * mm});
            skLineSegment(sketch, "E1127.MirrorCS", {"start": v(-108.26, 65.35) * mm, "end": v(-107.9, 65.5) * mm});
            skLineSegment(sketch, "E1128.MirrorCS", {"start": v(-108.26, 62.75) * mm, "end": v(-108.57, 62.99) * mm});
            skLineSegment(sketch, "E1129.MirrorCS", {"start": v(-106, -64.05) * mm, "end": v(-106.06, -64.44) * mm});
            skLineSegment(sketch, "E1130.MirrorCS", {"start": v(-108.95, -63.66) * mm, "end": v(-108.8, -63.3) * mm});
            skLineSegment(sketch, "E1131.MirrorCS", {"start": v(-107.9, 65.5) * mm, "end": v(-107.5, 65.55) * mm});
            skLineSegment(sketch, "E1132.MirrorCS", {"start": v(-108.57, 62.99) * mm, "end": v(-108.8, 63.3) * mm});
            skLineSegment(sketch, "E1133.MirrorCS", {"start": v(-106.06, -64.44) * mm, "end": v(-106.2, -64.8) * mm});
            skLineSegment(sketch, "E1134.MirrorCS", {"start": v(-108.8, -63.3) * mm, "end": v(-108.57, -62.99) * mm});
            skLineSegment(sketch, "E1135.MirrorCS", {"start": v(-107.5, 65.55) * mm, "end": v(-107.12, 65.5) * mm});
            skLineSegment(sketch, "E1136.MirrorCS", {"start": v(-108.8, 63.3) * mm, "end": v(-108.95, 63.66) * mm});
            skLineSegment(sketch, "E1137.MirrorCS", {"start": v(-106.2, -64.8) * mm, "end": v(-106.45, -65.11) * mm});
            skLineSegment(sketch, "E1138.MirrorCS", {"start": v(-108.57, -62.99) * mm, "end": v(-108.26, -62.75) * mm});
            skLineSegment(sketch, "E1139.MirrorCS", {"start": v(-106.06, 64.44) * mm, "end": v(-106, 64.05) * mm});
            skLineSegment(sketch, "E1140.MirrorCS", {"start": v(-107.12, 65.5) * mm, "end": v(-106.76, 65.35) * mm});
            skLineSegment(sketch, "E1141.MirrorCS", {"start": v(-106.45, -65.11) * mm, "end": v(-106.76, -65.35) * mm});
            skLineSegment(sketch, "E1142.MirrorCS", {"start": v(-108.26, -62.75) * mm, "end": v(-107.9, -62.6) * mm});
            skLineSegment(sketch, "E1143.MirrorCS", {"start": v(-106, 64.05) * mm, "end": v(-106.06, 63.66) * mm});
            skLineSegment(sketch, "E1144.MirrorCS", {"start": v(-106.76, 65.35) * mm, "end": v(-106.45, 65.11) * mm});
            skLineSegment(sketch, "E1145.MirrorCS", {"start": v(-106.76, -65.35) * mm, "end": v(-107.12, -65.5) * mm});
            skLineSegment(sketch, "E1146.MirrorCS", {"start": v(-107.9, -62.6) * mm, "end": v(-107.5, -62.55) * mm});
            skLineSegment(sketch, "E1147.MirrorCS", {"start": v(-106.06, 63.66) * mm, "end": v(-106.2, 63.3) * mm});
            skLineSegment(sketch, "E1148.MirrorCS", {"start": v(-106.45, 65.11) * mm, "end": v(-106.2, 64.8) * mm});
            skLineSegment(sketch, "E1149.MirrorCS", {"start": v(-107.12, -65.5) * mm, "end": v(-107.5, -65.55) * mm});
            skLineSegment(sketch, "E1150.MirrorCS", {"start": v(-110.5, 84.05) * mm, "end": v(-104.5, 84.05) * mm});
            skLineSegment(sketch, "E1151.MirrorCS", {"start": v(-107.5, -62.55) * mm, "end": v(-107.12, -62.6) * mm});
            skLineSegment(sketch, "E1152.MirrorCS", {"start": v(-106.2, 63.3) * mm, "end": v(-106.45, 62.99) * mm});
            skLineSegment(sketch, "E1153.MirrorCS", {"start": v(-110.5, -44.05) * mm, "end": v(-104.5, -44.05) * mm});
            skLineSegment(sketch, "E1154.MirrorCS", {"start": v(-104.5, -44.05) * mm, "end": v(-104.5, -34.05) * mm});
            skLineSegment(sketch, "E1155.MirrorCS", {"start": v(-104.5, 44.05) * mm, "end": v(-110.5, 44.05) * mm});
            skLineSegment(sketch, "E1156.MirrorCS", {"start": v(-106.2, 64.8) * mm, "end": v(-106.06, 64.44) * mm});
            skLineSegment(sketch, "E1157.MirrorCS", {"start": v(-110.5, -34.05) * mm, "end": v(-110.5, -44.05) * mm});
            skLineSegment(sketch, "E1158.MirrorCS", {"start": v(-107.5, -65.55) * mm, "end": v(-107.9, -65.5) * mm});
            skLineSegment(sketch, "E1159.MirrorCS", {"start": v(-110.5, 94.05) * mm, "end": v(-110.5, 84.05) * mm});
            skLineSegment(sketch, "E1160.MirrorCS", {"start": v(-104.5, 84.05) * mm, "end": v(-104.5, 94.05) * mm});
            skLineSegment(sketch, "E1161.MirrorCS", {"start": v(-104.5, -84.05) * mm, "end": v(-110.5, -84.05) * mm});
            skLineSegment(sketch, "E1162.MirrorCS", {"start": v(-107.12, -62.6) * mm, "end": v(-106.76, -62.75) * mm});
            skLineSegment(sketch, "E1163.MirrorCS", {"start": v(166.5, -237.15) * mm, "end": v(176.5, -237.15) * mm});
            skLineSegment(sketch, "E1164.MirrorCS", {"start": v(-189.5, -242.15) * mm, "end": v(-189.3, -243.7) * mm});
            skLineSegment(sketch, "E1165.MirrorCS", {"start": v(166.5, -237.15) * mm, "end": v(166.5, -243.15) * mm});
            skLineSegment(sketch, "E1166.MirrorCS", {"start": v(176.5, -243.15) * mm, "end": v(176.5, -237.15) * mm});
            skLineSegment(sketch, "E1167.MirrorCS", {"start": v(-189.3, -243.7) * mm, "end": v(-188.7, -245.15) * mm});
            skLineSegment(sketch, "E1168.MirrorCS", {"start": v(166.5, -243.15) * mm, "end": v(176.5, -243.15) * mm});
            skCircle(sketch, "E1169.MirrorC", {"center": v(146.5, -240.15) * mm, "radius": 1.5 * mm});
            skLineSegment(sketch, "E1170.MirrorCS", {"start": v(-188.7, -245.15) * mm, "end": v(-187.74, -246.4) * mm});
            skLineSegment(sketch, "E1171.MirrorCS", {"start": v(126.5, -243.15) * mm, "end": v(126.5, -237.15) * mm});
            skLineSegment(sketch, "E1172.MirrorCS", {"start": v(-187.74, -246.4) * mm, "end": v(-186.5, -247.35) * mm});
            skLineSegment(sketch, "E1173.MirrorCS", {"start": v(189.5, 162.15) * mm, "end": v(195.5, 162.15) * mm});
            skLineSegment(sketch, "E1174.MirrorCS", {"start": v(189.5, -212.15) * mm, "end": v(189.5, -222.15) * mm});
            skLineSegment(sketch, "E1175.MirrorCS", {"start": v(-186.5, -247.35) * mm, "end": v(-185.05, -247.95) * mm});
            skLineSegment(sketch, "E1176.MirrorCS", {"start": v(-169.5, -243.15) * mm, "end": v(-169.5, -237.15) * mm});
            skLineSegment(sketch, "E1177.MirrorCS", {"start": v(195.5, 172.15) * mm, "end": v(195.5, 162.15) * mm});
            skLineSegment(sketch, "E1178.MirrorCS", {"start": v(189.5, 172.15) * mm, "end": v(189.5, 162.15) * mm});
            skLineSegment(sketch, "E1179.MirrorCS", {"start": v(-185.05, -247.95) * mm, "end": v(-183.5, -248.15) * mm});
            skLineSegment(sketch, "E1180.MirrorCS", {"start": v(-26.5, -243.15) * mm, "end": v(-16.5, -243.15) * mm});
            skLineSegment(sketch, "E1181.MirrorCS", {"start": v(-110.5, 162.15) * mm, "end": v(-104.5, 162.15) * mm});
            skLineSegment(sketch, "E1182.MirrorCS", {"start": v(189.5, 44.05) * mm, "end": v(189.5, 34.05) * mm});
            skLineSegment(sketch, "E1183.MirrorCS", {"start": v(195.5, 44.05) * mm, "end": v(195.5, 34.05) * mm});
            skLineSegment(sketch, "E1184.MirrorCS", {"start": v(195.5, -222.15) * mm, "end": v(195.5, -212.15) * mm});
            skLineSegment(sketch, "E1185.MirrorCS", {"start": v(-159.5, -243.15) * mm, "end": v(-159.5, -237.15) * mm});
            skLineSegment(sketch, "E1186.MirrorCS", {"start": v(189.5, -212.15) * mm, "end": v(195.5, -212.15) * mm});
            skLineSegment(sketch, "E1187.MirrorCS", {"start": v(189.5, 34.05) * mm, "end": v(195.5, 34.05) * mm});
            skLineSegment(sketch, "E1188.MirrorCS", {"start": v(-110.5, 172.15) * mm, "end": v(-110.5, 162.15) * mm});
            skLineSegment(sketch, "E1189.MirrorCS", {"start": v(-169.5, -237.15) * mm, "end": v(-159.5, -237.15) * mm});
            skLineSegment(sketch, "E1190.MirrorCS", {"start": v(-110.5, -222.15) * mm, "end": v(-104.5, -222.15) * mm});
            skLineSegment(sketch, "E1191.MirrorCS", {"start": v(-169.5, -243.15) * mm, "end": v(-159.5, -243.15) * mm});
            skArc(sketch, "E1192.MirrorCS", {"start": v(200.5, -242.15) * mm, "mid": v(198.74, -246.4) * mm, "end": v(194.5, -248.15) * mm});
            skLineSegment(sketch, "E1193.MirrorCS", {"start": v(-110.5, 44.05) * mm, "end": v(-110.5, 34.05) * mm});
            skLineSegment(sketch, "E1194.MirrorCS", {"start": v(-16.5, -237.15) * mm, "end": v(-26.5, -237.15) * mm});
            skLineSegment(sketch, "E1195.MirrorCS", {"start": v(176.5, 243.15) * mm, "end": v(166.5, 243.15) * mm});
            skLineSegment(sketch, "E1196.MirrorCS", {"start": v(195.5, -172.15) * mm, "end": v(195.5, -162.15) * mm});
            skLineSegment(sketch, "E1197.MirrorCS", {"start": v(-26.5, -243.15) * mm, "end": v(-26.5, -237.15) * mm});
            skLineSegment(sketch, "E1198.MirrorCS", {"start": v(-104.5, 172.15) * mm, "end": v(-104.5, 162.15) * mm});
            skLineSegment(sketch, "E1199.MirrorCS", {"start": v(195.5, -84.05) * mm, "end": v(195.5, -94.05) * mm});
            skLineSegment(sketch, "E1200.MirrorCS", {"start": v(166.5, 237.15) * mm, "end": v(176.5, 237.15) * mm});
            skLineSegment(sketch, "E1201.MirrorCS", {"start": v(-110.5, 212.15) * mm, "end": v(-104.5, 212.15) * mm});
            skLineSegment(sketch, "E1202.MirrorCS", {"start": v(116.5, -243.15) * mm, "end": v(126.5, -243.15) * mm});
            skLineSegment(sketch, "E1203.MirrorCS", {"start": v(189.5, -222.15) * mm, "end": v(195.5, -222.15) * mm});
            skArc(sketch, "E1204.MirrorCS", {"start": v(-189.5, 242.15) * mm, "mid": v(-187.74, 246.4) * mm, "end": v(-183.5, 248.15) * mm});
            skLineSegment(sketch, "E1205.MirrorCS", {"start": v(116.5, -237.15) * mm, "end": v(126.5, -237.15) * mm});
            skLineSegment(sketch, "E1206.MirrorCS", {"start": v(-104.5, -222.15) * mm, "end": v(-104.5, -212.15) * mm});
            skArc(sketch, "E1207.MirrorCS", {"start": v(194.5, 248.15) * mm, "mid": v(198.74, 246.4) * mm, "end": v(200.5, 242.15) * mm});
            skLineSegment(sketch, "E1208.MirrorCS", {"start": v(-119.5, -243.15) * mm, "end": v(-119.5, -237.15) * mm});
            skLineSegment(sketch, "E1209.MirrorCS", {"start": v(-169.5, 243.15) * mm, "end": v(-169.5, 237.15) * mm});
            skLineSegment(sketch, "E1210.MirrorCS", {"start": v(-110.5, 222.15) * mm, "end": v(-110.5, 212.15) * mm});
            skLineSegment(sketch, "E1211.MirrorCS", {"start": v(-119.5, -237.15) * mm, "end": v(-109.5, -237.15) * mm});
            skLineSegment(sketch, "E1212.MirrorCS", {"start": v(-110.5, -172.15) * mm, "end": v(-104.5, -172.15) * mm});
            skCircle(sketch, "E1213.MirrorC", {"center": v(-107.5, -192.15) * mm, "radius": 1.5 * mm});
            skLineSegment(sketch, "E1214.MirrorCS", {"start": v(-110.5, 34.05) * mm, "end": v(-104.5, 34.05) * mm});
            skLineSegment(sketch, "E1215.MirrorCS", {"start": v(-109.5, 237.15) * mm, "end": v(-109.5, 243.15) * mm});
            skLineSegment(sketch, "E1216.MirrorCS", {"start": v(-104.5, -94.05) * mm, "end": v(-104.5, -84.05) * mm});
            skLineSegment(sketch, "E1217.MirrorCS", {"start": v(195.5, -162.15) * mm, "end": v(189.5, -162.15) * mm});
            skLineSegment(sketch, "E1218.MirrorCS", {"start": v(176.5, 237.15) * mm, "end": v(176.5, 243.15) * mm});
            skLineSegment(sketch, "E1219.MirrorCS", {"start": v(189.5, -84.05) * mm, "end": v(189.5, -94.05) * mm});
            skLineSegment(sketch, "E1220.MirrorCS", {"start": v(189.5, -162.15) * mm, "end": v(189.5, -172.15) * mm});
            skLineSegment(sketch, "E1221.MirrorCS", {"start": v(189.5, -94.05) * mm, "end": v(195.5, -94.05) * mm});
            skLineSegment(sketch, "E1222.MirrorCS", {"start": v(189.5, -172.15) * mm, "end": v(195.5, -172.15) * mm});
            skLineSegment(sketch, "E1223.MirrorCS", {"start": v(166.5, 243.15) * mm, "end": v(166.5, 237.15) * mm});
            skLineSegment(sketch, "E1224.MirrorCS", {"start": v(189.5, -84.05) * mm, "end": v(195.5, -84.05) * mm});
            skLineSegment(sketch, "E1225.MirrorCS", {"start": v(-104.5, -212.15) * mm, "end": v(-110.5, -212.15) * mm});
            skCircle(sketch, "E1226.MirrorC", {"center": v(192.5, -192.15) * mm, "radius": 1.5 * mm});
            skLineSegment(sketch, "E1227.MirrorCS", {"start": v(116.5, -243.15) * mm, "end": v(116.5, -237.15) * mm});
            skLineSegment(sketch, "E1228.MirrorCS", {"start": v(195.5, -34.05) * mm, "end": v(195.5, -44.05) * mm});
            skCircle(sketch, "E1229.MirrorC", {"center": v(-139.5, -240.15) * mm, "radius": 1.5 * mm});
            skLineSegment(sketch, "E1230.MirrorCS", {"start": v(-104.5, -162.15) * mm, "end": v(-110.5, -162.15) * mm});
            skCircle(sketch, "E1231.MirrorC", {"center": v(192.5, -64.05) * mm, "radius": 1.5 * mm});
            skLineSegment(sketch, "E1232.MirrorCS", {"start": v(-110.5, -212.15) * mm, "end": v(-110.5, -222.15) * mm});
            skLineSegment(sketch, "E1233.MirrorCS", {"start": v(-119.5, 243.15) * mm, "end": v(-109.5, 243.15) * mm});
            skLineSegment(sketch, "E1234.MirrorCS", {"start": v(-104.5, 212.15) * mm, "end": v(-104.5, 222.15) * mm});
            skLineSegment(sketch, "E1235.MirrorCS", {"start": v(-119.5, 237.15) * mm, "end": v(-109.5, 237.15) * mm});
            skLineSegment(sketch, "E1236.MirrorCS", {"start": v(-104.5, -172.15) * mm, "end": v(-104.5, -162.15) * mm});
            skLineSegment(sketch, "E1237.MirrorCS", {"start": v(-109.5, -243.15) * mm, "end": v(-109.5, -237.15) * mm});
            skLineSegment(sketch, "E1238.MirrorCS", {"start": v(-119.5, -243.15) * mm, "end": v(-109.5, -243.15) * mm});
            skLineSegment(sketch, "E1239.MirrorCS", {"start": v(-110.5, -162.15) * mm, "end": v(-110.5, -172.15) * mm});
            skCircle(sketch, "E1240.MirrorC", {"center": v(-107.5, 192.15) * mm, "radius": 1.5 * mm});
            skLineSegment(sketch, "E1241.MirrorCS", {"start": v(-104.5, 34.05) * mm, "end": v(-104.5, 44.05) * mm});
            skLineSegment(sketch, "E1242.MirrorCS", {"start": v(-110.5, -94.05) * mm, "end": v(-104.5, -94.05) * mm});
            skLineSegment(sketch, "E1243.MirrorCS", {"start": v(-104.5, 222.15) * mm, "end": v(-110.5, 222.15) * mm});
            skLineSegment(sketch, "E1244.MirrorCS", {"start": v(189.5, -34.05) * mm, "end": v(189.5, -44.05) * mm});
            skLineSegment(sketch, "E1245.MirrorCS", {"start": v(189.5, -44.05) * mm, "end": v(195.5, -44.05) * mm});
            skLineSegment(sketch, "E1246.MirrorCS", {"start": v(-104.5, 94.05) * mm, "end": v(-110.5, 94.05) * mm});
            skLineSegment(sketch, "E1247.MirrorCS", {"start": v(-110.5, 172.15) * mm, "end": v(-104.5, 172.15) * mm});
            skLineSegment(sketch, "E1248.MirrorCS", {"start": v(195.5, -34.05) * mm, "end": v(189.5, -34.05) * mm});
            skLineSegment(sketch, "E1249.MirrorCS", {"start": v(33.5, 237.15) * mm, "end": v(33.5, 243.15) * mm});
            skLineSegment(sketch, "E1250.MirrorCS", {"start": v(116.5, 243.15) * mm, "end": v(126.5, 243.15) * mm});
            skLineSegment(sketch, "E1251.MirrorCS", {"start": v(-110.5, -84.05) * mm, "end": v(-110.5, -94.05) * mm});
            skLineSegment(sketch, "E1252.MirrorCS", {"start": v(116.5, 243.15) * mm, "end": v(116.5, 237.15) * mm});
            skLineSegment(sketch, "E1253.MirrorCS", {"start": v(126.5, 237.15) * mm, "end": v(126.5, 243.15) * mm});
            skLineSegment(sketch, "E1254.MirrorCS", {"start": v(-26.5, 237.15) * mm, "end": v(-16.5, 237.15) * mm});
            skLineSegment(sketch, "E1255.MirrorCS", {"start": v(116.5, 237.15) * mm, "end": v(126.5, 237.15) * mm});
            skCircle(sketch, "E1256.MirrorC", {"center": v(146.5, 240.15) * mm, "radius": 1.5 * mm});
            skLineSegment(sketch, "E1257.MirrorCS", {"start": v(-26.5, 243.15) * mm, "end": v(-16.5, 243.15) * mm});
            skLineSegment(sketch, "E1258.MirrorCS", {"start": v(-104.5, -34.05) * mm, "end": v(-110.5, -34.05) * mm});
            skLineSegment(sketch, "E1259.MirrorCS", {"start": v(-26.5, 243.15) * mm, "end": v(-26.5, 237.15) * mm});
            skLineSegment(sketch, "E1260.MirrorCS", {"start": v(-189.5, 242.15) * mm, "end": v(-189.5, -242.15) * mm});
            skLineSegment(sketch, "E1261.MirrorCS", {"start": v(-183.5, 248.15) * mm, "end": v(194.5, 248.15) * mm});
            skLineSegment(sketch, "E1262.MirrorCS", {"start": v(194.5, -248.15) * mm, "end": v(-183.5, -248.15) * mm});
            skLineSegment(sketch, "E1263", {"start": v(200.5, 242.15) * mm, "end": v(200.5, -242.15) * mm});
            skLineSegment(sketch, "E1264.MirrorCS", {"start": v(158.57, -215.22) * mm, "end": v(157.59, -216.08) * mm});
            skLineSegment(sketch, "E1265.MirrorCS", {"start": v(157.59, -216.08) * mm, "end": v(156.5, -216.81) * mm});
            skLineSegment(sketch, "E1266.MirrorCS", {"start": v(161.5, -208.15) * mm, "end": v(161.41, -209.46) * mm});
            skLineSegment(sketch, "E1267.MirrorCS", {"start": v(156.5, -216.81) * mm, "end": v(155.33, -217.39) * mm});
            skLineSegment(sketch, "E1268.MirrorCS", {"start": v(160.16, -213.15) * mm, "end": v(159.43, -214.24) * mm});
            skLineSegment(sketch, "E1269.MirrorCS", {"start": v(161.16, -210.74) * mm, "end": v(160.74, -211.98) * mm});
            skLineSegment(sketch, "E1270.MirrorCS", {"start": v(161.41, -209.46) * mm, "end": v(161.16, -210.74) * mm});
            skLineSegment(sketch, "E1271.MirrorCS", {"start": v(161.5, -198.15) * mm, "end": v(161.5, -208.15) * mm});
            skLineSegment(sketch, "E1272.MirrorCS", {"start": v(152.8, -218.06) * mm, "end": v(151.5, -218.15) * mm});
            skLineSegment(sketch, "E1273.MirrorCS", {"start": v(154.09, -217.8) * mm, "end": v(152.8, -218.06) * mm});
            skLineSegment(sketch, "E1274.MirrorCS", {"start": v(155.33, -217.39) * mm, "end": v(154.09, -217.8) * mm});
            skLineSegment(sketch, "E1275.MirrorCS", {"start": v(159.43, -214.24) * mm, "end": v(158.57, -215.22) * mm});
            skLineSegment(sketch, "E1276.MirrorCS", {"start": v(160.74, -211.98) * mm, "end": v(160.16, -213.15) * mm});
            skLineSegment(sketch, "E1277.MirrorCS", {"start": v(-95.59, -216.08) * mm, "end": v(-96.57, -215.22) * mm});
            skLineSegment(sketch, "E1278.MirrorCS", {"start": v(-89.5, -218.15) * mm, "end": v(-90.8, -218.06) * mm});
            skLineSegment(sketch, "E1279.MirrorCS", {"start": v(141.45, 133.06) * mm, "end": v(140.75, 134.23) * mm});
            skLineSegment(sketch, "E1280.MirrorCS", {"start": v(-96.57, -215.22) * mm, "end": v(-97.43, -214.24) * mm});
            skLineSegment(sketch, "E1281.MirrorCS", {"start": v(-92.09, -217.8) * mm, "end": v(-93.33, -217.39) * mm});
            skLineSegment(sketch, "E1282.MirrorCS", {"start": v(138.94, 136.29) * mm, "end": v(137.87, 137.13) * mm});
            skLineSegment(sketch, "E1283.MirrorCS", {"start": v(140.75, 134.23) * mm, "end": v(139.9, 135.31) * mm});
            skLineSegment(sketch, "E1284.MirrorCS", {"start": v(-98.74, -211.98) * mm, "end": v(-99.16, -210.74) * mm});
            skLineSegment(sketch, "E1285.MirrorCS", {"start": v(-97.43, -214.24) * mm, "end": v(-98.16, -213.15) * mm});
            skLineSegment(sketch, "E1286.MirrorCS", {"start": v(-93.33, -217.39) * mm, "end": v(-94.5, -216.81) * mm});
            skLineSegment(sketch, "E1287.MirrorCS", {"start": v(135.45, 138.4) * mm, "end": v(134.15, 138.82) * mm});
            skLineSegment(sketch, "E1288.MirrorCS", {"start": v(137.87, 137.13) * mm, "end": v(136.7, 137.85) * mm});
            skLineSegment(sketch, "E1289.MirrorCS", {"start": v(139.9, 135.31) * mm, "end": v(138.94, 136.29) * mm});
            skLineSegment(sketch, "E1290.MirrorCS", {"start": v(-99.41, -209.46) * mm, "end": v(-99.5, -208.15) * mm});
            skLineSegment(sketch, "E1291.MirrorCS", {"start": v(142.64, 129.15) * mm, "end": v(142.4, 130.5) * mm});
            skLineSegment(sketch, "E1292.MirrorCS", {"start": v(142, 131.8) * mm, "end": v(141.45, 133.06) * mm});
            skLineSegment(sketch, "E1293.MirrorCS", {"start": v(-99.16, -210.74) * mm, "end": v(-99.41, -209.46) * mm});
            skLineSegment(sketch, "E1294.MirrorCS", {"start": v(142.4, 130.5) * mm, "end": v(142, 131.8) * mm});
            skLineSegment(sketch, "E1295.MirrorCS", {"start": v(-98.16, -213.15) * mm, "end": v(-98.74, -211.98) * mm});
            skLineSegment(sketch, "E1296.MirrorCS", {"start": v(132.8, 139.07) * mm, "end": v(131.44, 139.15) * mm});
            skLineSegment(sketch, "E1297.MirrorCS", {"start": v(-94.5, -216.81) * mm, "end": v(-95.59, -216.08) * mm});
            skLineSegment(sketch, "E1298.MirrorCS", {"start": v(134.15, 138.82) * mm, "end": v(132.8, 139.07) * mm});
            skLineSegment(sketch, "E1299.MirrorCS", {"start": v(136.7, 137.85) * mm, "end": v(135.45, 138.4) * mm});
            skLineSegment(sketch, "E1300.MirrorCS", {"start": v(-90.8, -218.06) * mm, "end": v(-92.09, -217.8) * mm});
            skLineSegment(sketch, "E1301.MirrorCS", {"start": v(161.5, -198.15) * mm, "end": v(161.36, -169.98) * mm});
            skArc(sketch, "E1302.MirrorCS", {"start": v(-99.5, 129.15) * mm, "mid": v(-96.57, 136.22) * mm, "end": v(-89.5, 139.15) * mm});
            skLineSegment(sketch, "E1303.MirrorCS", {"start": v(144.7, 111.16) * mm, "end": v(142.64, 129.15) * mm});
            skLineSegment(sketch, "E1304.MirrorCS", {"start": v(150.24, 55.08) * mm, "end": v(147.6, 83.13) * mm});
            skLineSegment(sketch, "E1305.MirrorCS", {"start": v(152.6, 27) * mm, "end": v(150.24, 55.08) * mm});
            skLineSegment(sketch, "E1306.MirrorCS", {"start": v(147.6, 83.13) * mm, "end": v(144.7, 111.16) * mm});
            skLineSegment(sketch, "E1307.MirrorCS", {"start": v(156.5, -29.2) * mm, "end": v(154.69, -1.09) * mm});
            skLineSegment(sketch, "E1308.MirrorCS", {"start": v(154.69, -1.09) * mm, "end": v(152.6, 27) * mm});
            skLineSegment(sketch, "E1309.MirrorCS", {"start": v(159.28, -85.48) * mm, "end": v(158.02, -57.34) * mm});
            skLineSegment(sketch, "E1310.MirrorCS", {"start": v(158.02, -57.34) * mm, "end": v(156.5, -29.2) * mm});
            skLineSegment(sketch, "E1311.MirrorCS", {"start": v(160.25, -113.64) * mm, "end": v(159.28, -85.48) * mm});
            skLineSegment(sketch, "E1312.MirrorCS", {"start": v(160.94, -141.8) * mm, "end": v(160.25, -113.64) * mm});
            skLineSegment(sketch, "E1313.MirrorCS", {"start": v(161.36, -169.98) * mm, "end": v(160.94, -141.8) * mm});
            skLineSegment(sketch, "E1314.MirrorCS", {"start": v(-99.5, 129.15) * mm, "end": v(-99.5, -208.15) * mm});
            skLineSegment(sketch, "E1315.MirrorCS", {"start": v(131.44, 139.15) * mm, "end": v(-89.5, 139.15) * mm});
            skLineSegment(sketch, "E1316.MirrorCS", {"start": v(-89.5, -218.15) * mm, "end": v(151.5, -218.15) * mm});
            skSolve(sketch);
        }
        {
            var Q0;
            Q0 = qSketchRegion(id + "F10", true);
            extrude(context, id + "F11", {"entities" : qUnion([Q0]), "depth" : 6 * mm, "offsetDistance" : 25 * mm});
        }
        {
            var Q0;
            Q0=makeQuery(id+"F3.opExtrude","SWEPT_FACE",FACE,{"disambiguationData":[OSD([sQuery(id+"F2.wireOp",EDGE,"E35")])]});
            cPlane(context, id + "F12", {"entities" : qUnion([Q0]), "cplaneType" : CPlaneType.OFFSET, "offset" : 0 * mm, "width" : 150 * mm, "height" : 150 * mm});
        }
        {
            var Q0;
            Q0=qCreatedBy(id+"F12.planeOp",FACE);
            var sketch = newSketch(context, id + "F13", { "sketchPlane" : qUnion([Q0])});
            skLineSegment(sketch, "E1317", {"start": v(74, -243.15) * mm, "end": v(84, -243.15) * mm});
            skLineSegment(sketch, "E1318", {"start": v(74, -237.15) * mm, "end": v(74, -243.15) * mm});
            skLineSegment(sketch, "E1319", {"start": v(105.5, -240.15) * mm, "end": v(105.45, -240.54) * mm});
            skLineSegment(sketch, "E1320", {"start": v(105.45, -240.54) * mm, "end": v(105.3, -240.9) * mm});
            skLineSegment(sketch, "E1321", {"start": v(105.3, -240.9) * mm, "end": v(105.06, -241.21) * mm});
            skLineSegment(sketch, "E1322", {"start": v(105.06, -241.21) * mm, "end": v(104.75, -241.45) * mm});
            skLineSegment(sketch, "E1323", {"start": v(104.75, -241.45) * mm, "end": v(104.39, -241.6) * mm});
            skLineSegment(sketch, "E1324", {"start": v(104.39, -241.6) * mm, "end": v(104, -241.65) * mm});
            skLineSegment(sketch, "E1325", {"start": v(104, -241.65) * mm, "end": v(103.61, -241.6) * mm});
            skLineSegment(sketch, "E1326", {"start": v(103.61, -241.6) * mm, "end": v(103.25, -241.45) * mm});
            skLineSegment(sketch, "E1327", {"start": v(103.25, -241.45) * mm, "end": v(102.94, -241.21) * mm});
            skLineSegment(sketch, "E1328", {"start": v(102.94, -241.21) * mm, "end": v(102.7, -240.9) * mm});
            skLineSegment(sketch, "E1329", {"start": v(102.7, -240.9) * mm, "end": v(102.55, -240.54) * mm});
            skLineSegment(sketch, "E1330", {"start": v(102.55, -240.54) * mm, "end": v(102.5, -240.15) * mm});
            skLineSegment(sketch, "E1331", {"start": v(102.5, -240.15) * mm, "end": v(102.55, -239.76) * mm});
            skLineSegment(sketch, "E1332", {"start": v(102.55, -239.76) * mm, "end": v(102.7, -239.4) * mm});
            skLineSegment(sketch, "E1333", {"start": v(102.7, -239.4) * mm, "end": v(102.94, -239.09) * mm});
            skLineSegment(sketch, "E1334", {"start": v(102.94, -239.09) * mm, "end": v(103.25, -238.85) * mm});
            skLineSegment(sketch, "E1335", {"start": v(103.25, -238.85) * mm, "end": v(103.61, -238.7) * mm});
            skLineSegment(sketch, "E1336", {"start": v(103.61, -238.7) * mm, "end": v(104, -238.65) * mm});
            skLineSegment(sketch, "E1337", {"start": v(104, -238.65) * mm, "end": v(104.39, -238.7) * mm});
            skLineSegment(sketch, "E1338", {"start": v(104.39, -238.7) * mm, "end": v(104.75, -238.85) * mm});
            skLineSegment(sketch, "E1339", {"start": v(104.75, -238.85) * mm, "end": v(105.06, -239.09) * mm});
            skLineSegment(sketch, "E1340", {"start": v(105.06, -239.09) * mm, "end": v(105.3, -239.4) * mm});
            skLineSegment(sketch, "E1341", {"start": v(105.3, -239.4) * mm, "end": v(105.45, -239.76) * mm});
            skLineSegment(sketch, "E1342", {"start": v(105.45, -239.76) * mm, "end": v(105.5, -240.15) * mm});
            skLineSegment(sketch, "E1343", {"start": v(30, -243.15) * mm, "end": v(30, -237.15) * mm});
            skLineSegment(sketch, "E1344", {"start": v(-114, -198.15) * mm, "end": v(-113.86, -169.98) * mm});
            skLineSegment(sketch, "E1345", {"start": v(-113.86, -169.98) * mm, "end": v(-113.44, -141.8) * mm});
            skLineSegment(sketch, "E1346", {"start": v(-113.44, -141.8) * mm, "end": v(-112.75, -113.64) * mm});
            skLineSegment(sketch, "E1347", {"start": v(-112.75, -113.64) * mm, "end": v(-111.78, -85.48) * mm});
            skLineSegment(sketch, "E1348", {"start": v(-111.78, -85.48) * mm, "end": v(-110.52, -57.34) * mm});
            skLineSegment(sketch, "E1349", {"start": v(-110.52, -57.34) * mm, "end": v(-109, -29.2) * mm});
            skLineSegment(sketch, "E1350", {"start": v(-109, -29.2) * mm, "end": v(-107.19, -1.09) * mm});
            skLineSegment(sketch, "E1351", {"start": v(-107.19, -1.09) * mm, "end": v(-105.1, 27) * mm});
            skLineSegment(sketch, "E1352", {"start": v(-105.1, 27) * mm, "end": v(-102.74, 55.08) * mm});
            skLineSegment(sketch, "E1353", {"start": v(-102.74, 55.08) * mm, "end": v(-100.1, 83.13) * mm});
            skLineSegment(sketch, "E1354", {"start": v(-100.1, 83.13) * mm, "end": v(-97.2, 111.16) * mm});
            skLineSegment(sketch, "E1355", {"start": v(-97.2, 111.16) * mm, "end": v(-95.14, 129.15) * mm});
            skLineSegment(sketch, "E1356", {"start": v(1.45, 240.54) * mm, "end": v(1.5, 240.15) * mm});
            skLineSegment(sketch, "E1357", {"start": v(1.5, 240.15) * mm, "end": v(1.45, 239.76) * mm});
            skLineSegment(sketch, "E1358", {"start": v(1.45, 239.76) * mm, "end": v(1.3, 239.4) * mm});
            skLineSegment(sketch, "E1359", {"start": v(1.3, 239.4) * mm, "end": v(1.06, 239.09) * mm});
            skLineSegment(sketch, "E1360", {"start": v(1.06, 239.09) * mm, "end": v(0.75, 238.85) * mm});
            skLineSegment(sketch, "E1361", {"start": v(0.75, 238.85) * mm, "end": v(0.39, 238.7) * mm});
            skLineSegment(sketch, "E1362", {"start": v(0.39, 238.7) * mm, "end": v(0, 238.65) * mm});
            skLineSegment(sketch, "E1363", {"start": v(0, 238.65) * mm, "end": v(-0.39, 238.7) * mm});
            skLineSegment(sketch, "E1364", {"start": v(-0.39, 238.7) * mm, "end": v(-0.75, 238.85) * mm});
            skLineSegment(sketch, "E1365", {"start": v(-0.75, 238.85) * mm, "end": v(-1.06, 239.09) * mm});
            skLineSegment(sketch, "E1366", {"start": v(-1.06, 239.09) * mm, "end": v(-1.3, 239.4) * mm});
            skLineSegment(sketch, "E1367", {"start": v(-1.3, 239.4) * mm, "end": v(-1.45, 239.76) * mm});
            skLineSegment(sketch, "E1368", {"start": v(-1.45, 239.76) * mm, "end": v(-1.5, 240.15) * mm});
            skLineSegment(sketch, "E1369", {"start": v(-1.5, 240.15) * mm, "end": v(-1.45, 240.54) * mm});
            skLineSegment(sketch, "E1370", {"start": v(-1.45, 240.54) * mm, "end": v(-1.3, 240.9) * mm});
            skLineSegment(sketch, "E1371", {"start": v(-1.3, 240.9) * mm, "end": v(-1.06, 241.21) * mm});
            skLineSegment(sketch, "E1372", {"start": v(-1.06, 241.21) * mm, "end": v(-0.75, 241.45) * mm});
            skLineSegment(sketch, "E1373", {"start": v(-0.75, 241.45) * mm, "end": v(-0.39, 241.6) * mm});
            skLineSegment(sketch, "E1374", {"start": v(-0.39, 241.6) * mm, "end": v(0, 241.65) * mm});
            skLineSegment(sketch, "E1375", {"start": v(0, 241.65) * mm, "end": v(0.39, 241.6) * mm});
            skLineSegment(sketch, "E1376", {"start": v(0.39, 241.6) * mm, "end": v(0.75, 241.45) * mm});
            skLineSegment(sketch, "E1377", {"start": v(0.75, 241.45) * mm, "end": v(1.06, 241.21) * mm});
            skLineSegment(sketch, "E1378", {"start": v(1.06, 241.21) * mm, "end": v(1.3, 240.9) * mm});
            skLineSegment(sketch, "E1379", {"start": v(1.3, 240.9) * mm, "end": v(1.45, 240.54) * mm});
            skLineSegment(sketch, "E1380", {"start": v(135, 193.65) * mm, "end": v(133, 193.65) * mm});
            skLineSegment(sketch, "E1381", {"start": v(-31.82, 215.15) * mm, "end": v(-129, 215.15) * mm});
            skLineSegment(sketch, "E1382", {"start": v(-31.82, 175.45) * mm, "end": v(-31.82, 215.15) * mm});
            skLineSegment(sketch, "E1383", {"start": v(-7.69, 183.59) * mm, "end": v(-6.91, 183.69) * mm});
            skLineSegment(sketch, "E1384", {"start": v(-6.91, 183.69) * mm, "end": v(-6.76, 183.67) * mm});
            skLineSegment(sketch, "E1385", {"start": v(-6.76, 183.67) * mm, "end": v(-6.14, 183.59) * mm});
            skLineSegment(sketch, "E1386", {"start": v(-6.14, 183.59) * mm, "end": v(-5.41, 183.29) * mm});
            skLineSegment(sketch, "E1387", {"start": v(-5.41, 183.29) * mm, "end": v(-4.8, 182.81) * mm});
            skLineSegment(sketch, "E1388", {"start": v(-4.8, 182.81) * mm, "end": v(-4.31, 182.19) * mm});
            skLineSegment(sketch, "E1389", {"start": v(-4.31, 182.19) * mm, "end": v(-4.01, 181.47) * mm});
            skLineSegment(sketch, "E1390", {"start": v(-4.01, 181.47) * mm, "end": v(-3.91, 180.69) * mm});
            skLineSegment(sketch, "E1391", {"start": v(-3.91, 180.69) * mm, "end": v(-4.01, 179.91) * mm});
            skLineSegment(sketch, "E1392", {"start": v(-4.01, 179.91) * mm, "end": v(-4.31, 179.19) * mm});
            skLineSegment(sketch, "E1393", {"start": v(-4.31, 179.19) * mm, "end": v(-4.8, 178.57) * mm});
            skLineSegment(sketch, "E1394", {"start": v(-4.8, 178.57) * mm, "end": v(-5.41, 178.1) * mm});
            skLineSegment(sketch, "E1395", {"start": v(-5.41, 178.1) * mm, "end": v(-6.14, 177.8) * mm});
            skLineSegment(sketch, "E1396", {"start": v(-6.14, 177.8) * mm, "end": v(-6.76, 177.7) * mm});
            skLineSegment(sketch, "E1397", {"start": v(-6.76, 177.7) * mm, "end": v(-6.91, 177.69) * mm});
            skLineSegment(sketch, "E1398", {"start": v(-6.91, 177.69) * mm, "end": v(-7.69, 177.8) * mm});
            skLineSegment(sketch, "E1399", {"start": v(-7.69, 177.8) * mm, "end": v(-8.41, 178.1) * mm});
            skLineSegment(sketch, "E1400", {"start": v(-8.41, 178.1) * mm, "end": v(-9.03, 178.57) * mm});
            skLineSegment(sketch, "E1401", {"start": v(-9.03, 178.57) * mm, "end": v(-9.51, 179.19) * mm});
            skLineSegment(sketch, "E1402", {"start": v(-9.51, 179.19) * mm, "end": v(-9.81, 179.91) * mm});
            skLineSegment(sketch, "E1403", {"start": v(-9.81, 179.91) * mm, "end": v(-9.91, 180.69) * mm});
            skLineSegment(sketch, "E1404", {"start": v(-9.91, 180.69) * mm, "end": v(-9.81, 181.47) * mm});
            skLineSegment(sketch, "E1405", {"start": v(-9.81, 181.47) * mm, "end": v(-9.51, 182.19) * mm});
            skLineSegment(sketch, "E1406", {"start": v(-9.51, 182.19) * mm, "end": v(-9.03, 182.81) * mm});
            skLineSegment(sketch, "E1407", {"start": v(-9.03, 182.81) * mm, "end": v(-8.41, 183.29) * mm});
            skLineSegment(sketch, "E1408", {"start": v(-8.41, 183.29) * mm, "end": v(-7.69, 183.59) * mm});
            skLineSegment(sketch, "E1409", {"start": v(134, 237.15) * mm, "end": v(134, 243.15) * mm});
            skLineSegment(sketch, "E1410", {"start": v(-84, 237.15) * mm, "end": v(-74, 237.15) * mm});
            skLineSegment(sketch, "E1411", {"start": v(-84, 243.15) * mm, "end": v(-84, 237.15) * mm});
            skLineSegment(sketch, "E1412", {"start": v(-20, 237.15) * mm, "end": v(-20, 243.15) * mm});
            skLineSegment(sketch, "E1413", {"start": v(-30, 243.15) * mm, "end": v(-30, 237.15) * mm});
            skLineSegment(sketch, "E1414", {"start": v(20, 243.15) * mm, "end": v(20, 237.15) * mm});
            skLineSegment(sketch, "E1415", {"start": v(135, 193.65) * mm, "end": v(135, 196.15) * mm});
            skLineSegment(sketch, "E1416", {"start": v(138, 196.15) * mm, "end": v(135, 196.15) * mm});
            skLineSegment(sketch, "E1417", {"start": v(138, 193.65) * mm, "end": v(138, 196.15) * mm});
            skLineSegment(sketch, "E1418", {"start": v(144, 193.65) * mm, "end": v(138, 193.65) * mm});
            skLineSegment(sketch, "E1419", {"start": v(144, 193.65) * mm, "end": v(144, 212.15) * mm});
            skLineSegment(sketch, "E1420", {"start": v(144, 212.15) * mm, "end": v(150, 212.15) * mm});
            skLineSegment(sketch, "E1421", {"start": v(150, 212.15) * mm, "end": v(150, 222.15) * mm});
            skLineSegment(sketch, "E1422", {"start": v(144, 222.15) * mm, "end": v(150, 222.15) * mm});
            skLineSegment(sketch, "E1423", {"start": v(144, 222.15) * mm, "end": v(144, 248.15) * mm});
            skLineSegment(sketch, "E1424", {"start": v(-144, 248.15) * mm, "end": v(144, 248.15) * mm});
            skLineSegment(sketch, "E1425", {"start": v(-134, 243.15) * mm, "end": v(-134, 237.15) * mm});
            skLineSegment(sketch, "E1426", {"start": v(-20, 243.15) * mm, "end": v(-30, 243.15) * mm});
            skLineSegment(sketch, "E1427", {"start": v(138, 188.15) * mm, "end": v(135, 188.15) * mm});
            skLineSegment(sketch, "E1428", {"start": v(135, 190.65) * mm, "end": v(135, 188.15) * mm});
            skLineSegment(sketch, "E1429", {"start": v(135, 190.65) * mm, "end": v(133, 190.65) * mm});
            skLineSegment(sketch, "E1430", {"start": v(133, 193.65) * mm, "end": v(133, 190.65) * mm});
            skLineSegment(sketch, "E1431", {"start": v(144, 162.15) * mm, "end": v(150, 162.15) * mm});
            skLineSegment(sketch, "E1432", {"start": v(-105.06, 241.21) * mm, "end": v(-104.75, 241.45) * mm});
            skLineSegment(sketch, "E1433", {"start": v(-104.75, 241.45) * mm, "end": v(-104.39, 241.6) * mm});
            skLineSegment(sketch, "E1434", {"start": v(-104.39, 241.6) * mm, "end": v(-104, 241.65) * mm});
            skLineSegment(sketch, "E1435", {"start": v(-104, 241.65) * mm, "end": v(-103.61, 241.6) * mm});
            skLineSegment(sketch, "E1436", {"start": v(-103.61, 241.6) * mm, "end": v(-103.25, 241.45) * mm});
            skLineSegment(sketch, "E1437", {"start": v(-103.25, 241.45) * mm, "end": v(-102.94, 241.21) * mm});
            skLineSegment(sketch, "E1438", {"start": v(-102.94, 241.21) * mm, "end": v(-102.7, 240.9) * mm});
            skLineSegment(sketch, "E1439", {"start": v(-102.7, 240.9) * mm, "end": v(-102.55, 240.54) * mm});
            skLineSegment(sketch, "E1440", {"start": v(-102.55, 240.54) * mm, "end": v(-102.5, 240.15) * mm});
            skLineSegment(sketch, "E1441", {"start": v(-102.5, 240.15) * mm, "end": v(-102.55, 239.76) * mm});
            skLineSegment(sketch, "E1442", {"start": v(-102.55, 239.76) * mm, "end": v(-102.7, 239.4) * mm});
            skLineSegment(sketch, "E1443", {"start": v(-102.7, 239.4) * mm, "end": v(-102.94, 239.09) * mm});
            skLineSegment(sketch, "E1444", {"start": v(-102.94, 239.09) * mm, "end": v(-103.25, 238.85) * mm});
            skLineSegment(sketch, "E1445", {"start": v(-103.25, 238.85) * mm, "end": v(-103.61, 238.7) * mm});
            skLineSegment(sketch, "E1446", {"start": v(-103.61, 238.7) * mm, "end": v(-104, 238.65) * mm});
            skLineSegment(sketch, "E1447", {"start": v(-104, 238.65) * mm, "end": v(-104.39, 238.7) * mm});
            skLineSegment(sketch, "E1448", {"start": v(-104.39, 238.7) * mm, "end": v(-104.75, 238.85) * mm});
            skLineSegment(sketch, "E1449", {"start": v(-104.75, 238.85) * mm, "end": v(-105.06, 239.09) * mm});
            skLineSegment(sketch, "E1450", {"start": v(-105.06, 239.09) * mm, "end": v(-105.3, 239.4) * mm});
            skLineSegment(sketch, "E1451", {"start": v(-105.3, 239.4) * mm, "end": v(-105.45, 239.76) * mm});
            skLineSegment(sketch, "E1452", {"start": v(-105.45, 239.76) * mm, "end": v(-105.5, 240.15) * mm});
            skLineSegment(sketch, "E1453", {"start": v(-105.5, 240.15) * mm, "end": v(-105.45, 240.54) * mm});
            skLineSegment(sketch, "E1454", {"start": v(-105.45, 240.54) * mm, "end": v(-105.3, 240.9) * mm});
            skLineSegment(sketch, "E1455", {"start": v(-105.3, 240.9) * mm, "end": v(-105.06, 241.21) * mm});
            skLineSegment(sketch, "E1456", {"start": v(-129, 215.15) * mm, "end": v(-129, 175.45) * mm});
            skLineSegment(sketch, "E1457", {"start": v(-129, 175.45) * mm, "end": v(-31.82, 175.45) * mm});
            skLineSegment(sketch, "E1458", {"start": v(134, -243.15) * mm, "end": v(134, -237.15) * mm});
            skLineSegment(sketch, "E1459", {"start": v(0, -238.65) * mm, "end": v(0.39, -238.7) * mm});
            skLineSegment(sketch, "E1460", {"start": v(0.39, -238.7) * mm, "end": v(0.75, -238.85) * mm});
            skLineSegment(sketch, "E1461", {"start": v(0.75, -238.85) * mm, "end": v(1.06, -239.09) * mm});
            skLineSegment(sketch, "E1462", {"start": v(1.06, -239.09) * mm, "end": v(1.3, -239.4) * mm});
            skLineSegment(sketch, "E1463", {"start": v(1.3, -239.4) * mm, "end": v(1.45, -239.76) * mm});
            skLineSegment(sketch, "E1464", {"start": v(1.45, -239.76) * mm, "end": v(1.5, -240.15) * mm});
            skLineSegment(sketch, "E1465", {"start": v(1.5, -240.15) * mm, "end": v(1.45, -240.54) * mm});
            skLineSegment(sketch, "E1466", {"start": v(1.45, -240.54) * mm, "end": v(1.3, -240.9) * mm});
            skLineSegment(sketch, "E1467", {"start": v(1.3, -240.9) * mm, "end": v(1.06, -241.21) * mm});
            skLineSegment(sketch, "E1468", {"start": v(1.06, -241.21) * mm, "end": v(0.75, -241.45) * mm});
            skLineSegment(sketch, "E1469", {"start": v(0.75, -241.45) * mm, "end": v(0.39, -241.6) * mm});
            skLineSegment(sketch, "E1470", {"start": v(0.39, -241.6) * mm, "end": v(0, -241.65) * mm});
            skLineSegment(sketch, "E1471", {"start": v(0, -241.65) * mm, "end": v(-0.39, -241.6) * mm});
            skLineSegment(sketch, "E1472", {"start": v(-0.39, -241.6) * mm, "end": v(-0.75, -241.45) * mm});
            skLineSegment(sketch, "E1473", {"start": v(-0.75, -241.45) * mm, "end": v(-1.06, -241.21) * mm});
            skLineSegment(sketch, "E1474", {"start": v(-1.06, -241.21) * mm, "end": v(-1.3, -240.9) * mm});
            skLineSegment(sketch, "E1475", {"start": v(-1.3, -240.9) * mm, "end": v(-1.45, -240.54) * mm});
            skLineSegment(sketch, "E1476", {"start": v(-1.45, -240.54) * mm, "end": v(-1.5, -240.15) * mm});
            skLineSegment(sketch, "E1477", {"start": v(-1.5, -240.15) * mm, "end": v(-1.45, -239.76) * mm});
            skLineSegment(sketch, "E1478", {"start": v(-1.45, -239.76) * mm, "end": v(-1.3, -239.4) * mm});
            skLineSegment(sketch, "E1479", {"start": v(-1.3, -239.4) * mm, "end": v(-1.06, -239.09) * mm});
            skLineSegment(sketch, "E1480", {"start": v(-1.06, -239.09) * mm, "end": v(-0.75, -238.85) * mm});
            skLineSegment(sketch, "E1481", {"start": v(-0.75, -238.85) * mm, "end": v(-0.39, -238.7) * mm});
            skLineSegment(sketch, "E1482", {"start": v(-0.39, -238.7) * mm, "end": v(0, -238.65) * mm});
            skLineSegment(sketch, "E1483", {"start": v(-84, -243.15) * mm, "end": v(-74, -243.15) * mm});
            skLineSegment(sketch, "E1484", {"start": v(-84, -237.15) * mm, "end": v(-84, -243.15) * mm});
            skLineSegment(sketch, "E1485", {"start": v(-105.45, -240.54) * mm, "end": v(-105.5, -240.15) * mm});
            skLineSegment(sketch, "E1486", {"start": v(-105.5, -240.15) * mm, "end": v(-105.45, -239.76) * mm});
            skLineSegment(sketch, "E1487", {"start": v(-105.45, -239.76) * mm, "end": v(-105.3, -239.4) * mm});
            skLineSegment(sketch, "E1488", {"start": v(-105.3, -239.4) * mm, "end": v(-105.06, -239.09) * mm});
            skLineSegment(sketch, "E1489", {"start": v(-105.06, -239.09) * mm, "end": v(-104.75, -238.85) * mm});
            skLineSegment(sketch, "E1490", {"start": v(-104.75, -238.85) * mm, "end": v(-104.39, -238.7) * mm});
            skLineSegment(sketch, "E1491", {"start": v(-104.39, -238.7) * mm, "end": v(-104, -238.65) * mm});
            skLineSegment(sketch, "E1492", {"start": v(-104, -238.65) * mm, "end": v(-103.61, -238.7) * mm});
            skLineSegment(sketch, "E1493", {"start": v(-103.61, -238.7) * mm, "end": v(-103.25, -238.85) * mm});
            skLineSegment(sketch, "E1494", {"start": v(-103.25, -238.85) * mm, "end": v(-102.94, -239.09) * mm});
            skLineSegment(sketch, "E1495", {"start": v(-102.94, -239.09) * mm, "end": v(-102.7, -239.4) * mm});
            skLineSegment(sketch, "E1496", {"start": v(-102.7, -239.4) * mm, "end": v(-102.55, -239.76) * mm});
            skLineSegment(sketch, "E1497", {"start": v(-102.55, -239.76) * mm, "end": v(-102.5, -240.15) * mm});
            skLineSegment(sketch, "E1498", {"start": v(-102.5, -240.15) * mm, "end": v(-102.55, -240.54) * mm});
            skLineSegment(sketch, "E1499", {"start": v(-102.55, -240.54) * mm, "end": v(-102.7, -240.9) * mm});
            skLineSegment(sketch, "E1500", {"start": v(-102.7, -240.9) * mm, "end": v(-102.94, -241.21) * mm});
            skLineSegment(sketch, "E1501", {"start": v(-102.94, -241.21) * mm, "end": v(-103.25, -241.45) * mm});
            skLineSegment(sketch, "E1502", {"start": v(-103.25, -241.45) * mm, "end": v(-103.61, -241.6) * mm});
            skLineSegment(sketch, "E1503", {"start": v(-103.61, -241.6) * mm, "end": v(-104, -241.65) * mm});
            skLineSegment(sketch, "E1504", {"start": v(-104, -241.65) * mm, "end": v(-104.39, -241.6) * mm});
            skLineSegment(sketch, "E1505", {"start": v(-104.39, -241.6) * mm, "end": v(-104.75, -241.45) * mm});
            skLineSegment(sketch, "E1506", {"start": v(-104.75, -241.45) * mm, "end": v(-105.06, -241.21) * mm});
            skLineSegment(sketch, "E1507", {"start": v(-105.06, -241.21) * mm, "end": v(-105.3, -240.9) * mm});
            skLineSegment(sketch, "E1508", {"start": v(-105.3, -240.9) * mm, "end": v(-105.45, -240.54) * mm});
            skLineSegment(sketch, "E1509", {"start": v(-84, 139.15) * mm, "end": v(84, 139.15) * mm});
            skLineSegment(sketch, "E1510", {"start": v(-84, 139.15) * mm, "end": v(-85.36, 139.06) * mm});
            skLineSegment(sketch, "E1511", {"start": v(-85.36, 139.06) * mm, "end": v(-86.7, 138.8) * mm});
            skLineSegment(sketch, "E1512", {"start": v(-86.7, 138.8) * mm, "end": v(-88, 138.4) * mm});
            skLineSegment(sketch, "E1513", {"start": v(-88, 138.4) * mm, "end": v(-89.24, 137.83) * mm});
            skLineSegment(sketch, "E1514", {"start": v(-89.24, 137.83) * mm, "end": v(-90.4, 137.11) * mm});
            skLineSegment(sketch, "E1515", {"start": v(-90.4, 137.11) * mm, "end": v(-91.47, 136.26) * mm});
            skLineSegment(sketch, "E1516", {"start": v(-91.47, 136.26) * mm, "end": v(-92.43, 135.3) * mm});
            skLineSegment(sketch, "E1517", {"start": v(-92.43, 135.3) * mm, "end": v(-93.26, 134.22) * mm});
            skLineSegment(sketch, "E1518", {"start": v(-93.26, 134.22) * mm, "end": v(-93.96, 133.04) * mm});
            skLineSegment(sketch, "E1519", {"start": v(-93.96, 133.04) * mm, "end": v(-94.5, 131.8) * mm});
            skLineSegment(sketch, "E1520", {"start": v(-94.5, 131.8) * mm, "end": v(-94.9, 130.5) * mm});
            skLineSegment(sketch, "E1521", {"start": v(-94.9, 130.5) * mm, "end": v(-95.14, 129.15) * mm});
            skLineSegment(sketch, "E1522", {"start": v(30, 237.15) * mm, "end": v(30, 243.15) * mm});
            skLineSegment(sketch, "E1523", {"start": v(-124, 243.15) * mm, "end": v(-134, 243.15) * mm});
            skLineSegment(sketch, "E1524", {"start": v(-124, 237.15) * mm, "end": v(-124, 243.15) * mm});
            skLineSegment(sketch, "E1525", {"start": v(-134, 237.15) * mm, "end": v(-124, 237.15) * mm});
            skLineSegment(sketch, "E1526", {"start": v(124, 237.15) * mm, "end": v(134, 237.15) * mm});
            skLineSegment(sketch, "E1527", {"start": v(124, 243.15) * mm, "end": v(124, 237.15) * mm});
            skLineSegment(sketch, "E1528", {"start": v(134, 243.15) * mm, "end": v(124, 243.15) * mm});
            skLineSegment(sketch, "E1529", {"start": v(84, 237.15) * mm, "end": v(84, 243.15) * mm});
            skLineSegment(sketch, "E1530", {"start": v(74, 237.15) * mm, "end": v(84, 237.15) * mm});
            skLineSegment(sketch, "E1531", {"start": v(74, 243.15) * mm, "end": v(74, 237.15) * mm});
            skLineSegment(sketch, "E1532", {"start": v(20, 237.15) * mm, "end": v(30, 237.15) * mm});
            skLineSegment(sketch, "E1533", {"start": v(-74, 243.15) * mm, "end": v(-84, 243.15) * mm});
            skLineSegment(sketch, "E1534", {"start": v(-74, 237.15) * mm, "end": v(-74, 243.15) * mm});
            skLineSegment(sketch, "E1535", {"start": v(150, 172.15) * mm, "end": v(150, 162.15) * mm});
            skLineSegment(sketch, "E1536", {"start": v(144, 172.15) * mm, "end": v(150, 172.15) * mm});
            skLineSegment(sketch, "E1537", {"start": v(144, 172.15) * mm, "end": v(144, 190.65) * mm});
            skLineSegment(sketch, "E1538", {"start": v(144, 190.65) * mm, "end": v(138, 190.65) * mm});
            skLineSegment(sketch, "E1539", {"start": v(138, 190.65) * mm, "end": v(138, 188.15) * mm});
            skLineSegment(sketch, "E1540", {"start": v(84, 139.15) * mm, "end": v(85.36, 139.07) * mm});
            skLineSegment(sketch, "E1541", {"start": v(85.36, 139.07) * mm, "end": v(86.7, 138.82) * mm});
            skLineSegment(sketch, "E1542", {"start": v(86.7, 138.82) * mm, "end": v(88, 138.41) * mm});
            skLineSegment(sketch, "E1543", {"start": v(88, 138.41) * mm, "end": v(89.23, 137.85) * mm});
            skLineSegment(sketch, "E1544", {"start": v(89.23, 137.85) * mm, "end": v(90.4, 137.15) * mm});
            skLineSegment(sketch, "E1545", {"start": v(90.4, 137.15) * mm, "end": v(91.46, 136.3) * mm});
            skLineSegment(sketch, "E1546", {"start": v(91.46, 136.3) * mm, "end": v(92.42, 135.34) * mm});
            skLineSegment(sketch, "E1547", {"start": v(92.42, 135.34) * mm, "end": v(93.25, 134.27) * mm});
            skLineSegment(sketch, "E1548", {"start": v(93.25, 134.27) * mm, "end": v(93.95, 133.1) * mm});
            skLineSegment(sketch, "E1549", {"start": v(93.95, 133.1) * mm, "end": v(94.5, 131.85) * mm});
            skLineSegment(sketch, "E1550", {"start": v(94.5, 131.85) * mm, "end": v(94.9, 130.55) * mm});
            skLineSegment(sketch, "E1551", {"start": v(94.9, 130.55) * mm, "end": v(95.13, 129.21) * mm});
            skLineSegment(sketch, "E1552", {"start": v(144, -34.05) * mm, "end": v(144, 34.05) * mm});
            skLineSegment(sketch, "E1553", {"start": v(-114, -208.15) * mm, "end": v(-114, -198.15) * mm});
            skLineSegment(sketch, "E1554", {"start": v(-114, -208.15) * mm, "end": v(-113.91, -209.46) * mm});
            skLineSegment(sketch, "E1555", {"start": v(-113.91, -209.46) * mm, "end": v(-113.66, -210.74) * mm});
            skLineSegment(sketch, "E1556", {"start": v(-113.66, -210.74) * mm, "end": v(-113.24, -211.98) * mm});
            skLineSegment(sketch, "E1557", {"start": v(-113.24, -211.98) * mm, "end": v(-112.66, -213.15) * mm});
            skLineSegment(sketch, "E1558", {"start": v(-112.66, -213.15) * mm, "end": v(-111.93, -214.24) * mm});
            skLineSegment(sketch, "E1559", {"start": v(-111.93, -214.24) * mm, "end": v(-111.07, -215.22) * mm});
            skLineSegment(sketch, "E1560", {"start": v(-111.07, -215.22) * mm, "end": v(-110.09, -216.08) * mm});
            skLineSegment(sketch, "E1561", {"start": v(-110.09, -216.08) * mm, "end": v(-109, -216.81) * mm});
            skLineSegment(sketch, "E1562", {"start": v(-109, -216.81) * mm, "end": v(-107.83, -217.39) * mm});
            skLineSegment(sketch, "E1563", {"start": v(-107.83, -217.39) * mm, "end": v(-106.59, -217.8) * mm});
            skLineSegment(sketch, "E1564", {"start": v(-106.59, -217.8) * mm, "end": v(-105.3, -218.06) * mm});
            skLineSegment(sketch, "E1565", {"start": v(-105.3, -218.06) * mm, "end": v(-104, -218.15) * mm});
            skLineSegment(sketch, "E1566", {"start": v(114, -208.15) * mm, "end": v(114, -198.15) * mm});
            skLineSegment(sketch, "E1567", {"start": v(114, -198.15) * mm, "end": v(113.86, -169.98) * mm});
            skLineSegment(sketch, "E1568", {"start": v(113.86, -169.98) * mm, "end": v(113.44, -141.8) * mm});
            skLineSegment(sketch, "E1569", {"start": v(113.44, -141.8) * mm, "end": v(112.75, -113.64) * mm});
            skLineSegment(sketch, "E1570", {"start": v(112.75, -113.64) * mm, "end": v(111.78, -85.48) * mm});
            skLineSegment(sketch, "E1571", {"start": v(111.78, -85.48) * mm, "end": v(110.52, -57.34) * mm});
            skLineSegment(sketch, "E1572", {"start": v(110.52, -57.34) * mm, "end": v(109, -29.2) * mm});
            skLineSegment(sketch, "E1573", {"start": v(109, -29.2) * mm, "end": v(107.19, -1.09) * mm});
            skLineSegment(sketch, "E1574", {"start": v(107.19, -1.09) * mm, "end": v(105.1, 27) * mm});
            skLineSegment(sketch, "E1575", {"start": v(105.1, 27) * mm, "end": v(102.74, 55.08) * mm});
            skLineSegment(sketch, "E1576", {"start": v(102.74, 55.08) * mm, "end": v(100.1, 83.13) * mm});
            skLineSegment(sketch, "E1577", {"start": v(100.1, 83.13) * mm, "end": v(97.2, 111.16) * mm});
            skLineSegment(sketch, "E1578", {"start": v(97.2, 111.16) * mm, "end": v(95.13, 129.21) * mm});
            skLineSegment(sketch, "E1579", {"start": v(-30, 237.15) * mm, "end": v(-20, 237.15) * mm});
            skLineSegment(sketch, "E1580", {"start": v(84, 243.15) * mm, "end": v(74, 243.15) * mm});
            skLineSegment(sketch, "E1581", {"start": v(-8.91, 201.15) * mm, "end": v(-7.95, 201.55) * mm});
            skLineSegment(sketch, "E1582", {"start": v(-7.95, 201.55) * mm, "end": v(-6.91, 201.69) * mm});
            skLineSegment(sketch, "E1583", {"start": v(-6.91, 201.69) * mm, "end": v(-6.76, 201.67) * mm});
            skLineSegment(sketch, "E1584", {"start": v(-6.76, 201.67) * mm, "end": v(-5.88, 201.55) * mm});
            skLineSegment(sketch, "E1585", {"start": v(-5.88, 201.55) * mm, "end": v(-4.91, 201.15) * mm});
            skLineSegment(sketch, "E1586", {"start": v(-4.91, 201.15) * mm, "end": v(-4.08, 200.52) * mm});
            skLineSegment(sketch, "E1587", {"start": v(-4.08, 200.52) * mm, "end": v(-3.45, 199.69) * mm});
            skLineSegment(sketch, "E1588", {"start": v(-3.45, 199.69) * mm, "end": v(-3.05, 198.72) * mm});
            skLineSegment(sketch, "E1589", {"start": v(-3.05, 198.72) * mm, "end": v(-2.91, 197.69) * mm});
            skLineSegment(sketch, "E1590", {"start": v(-2.91, 197.69) * mm, "end": v(-3.05, 196.65) * mm});
            skLineSegment(sketch, "E1591", {"start": v(-3.05, 196.65) * mm, "end": v(-3.45, 195.69) * mm});
            skLineSegment(sketch, "E1592", {"start": v(-3.45, 195.69) * mm, "end": v(-4.08, 194.86) * mm});
            skLineSegment(sketch, "E1593", {"start": v(-4.08, 194.86) * mm, "end": v(-4.91, 194.23) * mm});
            skLineSegment(sketch, "E1594", {"start": v(-4.91, 194.23) * mm, "end": v(-5.88, 193.83) * mm});
            skLineSegment(sketch, "E1595", {"start": v(-5.88, 193.83) * mm, "end": v(-6.76, 193.7) * mm});
            skLineSegment(sketch, "E1596", {"start": v(-6.76, 193.7) * mm, "end": v(-6.91, 193.69) * mm});
            skLineSegment(sketch, "E1597", {"start": v(-6.91, 193.69) * mm, "end": v(-7.95, 193.83) * mm});
            skLineSegment(sketch, "E1598", {"start": v(-7.95, 193.83) * mm, "end": v(-8.91, 194.23) * mm});
            skLineSegment(sketch, "E1599", {"start": v(-8.91, 194.23) * mm, "end": v(-9.74, 194.86) * mm});
            skLineSegment(sketch, "E1600", {"start": v(-9.74, 194.86) * mm, "end": v(-10.38, 195.69) * mm});
            skLineSegment(sketch, "E1601", {"start": v(-10.38, 195.69) * mm, "end": v(-10.78, 196.65) * mm});
            skLineSegment(sketch, "E1602", {"start": v(-10.78, 196.65) * mm, "end": v(-10.91, 197.69) * mm});
            skLineSegment(sketch, "E1603", {"start": v(-10.91, 197.69) * mm, "end": v(-10.78, 198.72) * mm});
            skLineSegment(sketch, "E1604", {"start": v(-10.78, 198.72) * mm, "end": v(-10.38, 199.69) * mm});
            skLineSegment(sketch, "E1605", {"start": v(-10.38, 199.69) * mm, "end": v(-9.74, 200.52) * mm});
            skLineSegment(sketch, "E1606", {"start": v(-9.74, 200.52) * mm, "end": v(-8.91, 201.15) * mm});
            skLineSegment(sketch, "E1607", {"start": v(102.7, 240.9) * mm, "end": v(102.94, 241.21) * mm});
            skLineSegment(sketch, "E1608", {"start": v(102.94, 241.21) * mm, "end": v(103.25, 241.45) * mm});
            skLineSegment(sketch, "E1609", {"start": v(103.25, 241.45) * mm, "end": v(103.61, 241.6) * mm});
            skLineSegment(sketch, "E1610", {"start": v(103.61, 241.6) * mm, "end": v(104, 241.65) * mm});
            skLineSegment(sketch, "E1611", {"start": v(104, 241.65) * mm, "end": v(104.39, 241.6) * mm});
            skLineSegment(sketch, "E1612", {"start": v(104.39, 241.6) * mm, "end": v(104.75, 241.45) * mm});
            skLineSegment(sketch, "E1613", {"start": v(104.75, 241.45) * mm, "end": v(105.06, 241.21) * mm});
            skLineSegment(sketch, "E1614", {"start": v(105.06, 241.21) * mm, "end": v(105.3, 240.9) * mm});
            skLineSegment(sketch, "E1615", {"start": v(105.3, 240.9) * mm, "end": v(105.45, 240.54) * mm});
            skLineSegment(sketch, "E1616", {"start": v(105.45, 240.54) * mm, "end": v(105.5, 240.15) * mm});
            skLineSegment(sketch, "E1617", {"start": v(105.5, 240.15) * mm, "end": v(105.45, 239.76) * mm});
            skLineSegment(sketch, "E1618", {"start": v(105.45, 239.76) * mm, "end": v(105.3, 239.4) * mm});
            skLineSegment(sketch, "E1619", {"start": v(105.3, 239.4) * mm, "end": v(105.06, 239.09) * mm});
            skLineSegment(sketch, "E1620", {"start": v(105.06, 239.09) * mm, "end": v(104.75, 238.85) * mm});
            skLineSegment(sketch, "E1621", {"start": v(104.75, 238.85) * mm, "end": v(104.39, 238.7) * mm});
            skLineSegment(sketch, "E1622", {"start": v(104.39, 238.7) * mm, "end": v(104, 238.65) * mm});
            skLineSegment(sketch, "E1623", {"start": v(104, 238.65) * mm, "end": v(103.61, 238.7) * mm});
            skLineSegment(sketch, "E1624", {"start": v(103.61, 238.7) * mm, "end": v(103.25, 238.85) * mm});
            skLineSegment(sketch, "E1625", {"start": v(103.25, 238.85) * mm, "end": v(102.94, 239.09) * mm});
            skLineSegment(sketch, "E1626", {"start": v(102.94, 239.09) * mm, "end": v(102.7, 239.4) * mm});
            skLineSegment(sketch, "E1627", {"start": v(102.7, 239.4) * mm, "end": v(102.55, 239.76) * mm});
            skLineSegment(sketch, "E1628", {"start": v(102.55, 239.76) * mm, "end": v(102.5, 240.15) * mm});
            skLineSegment(sketch, "E1629", {"start": v(102.5, 240.15) * mm, "end": v(102.55, 240.54) * mm});
            skLineSegment(sketch, "E1630", {"start": v(102.55, 240.54) * mm, "end": v(102.7, 240.9) * mm});
            skLineSegment(sketch, "E1631", {"start": v(104, -218.15) * mm, "end": v(-104, -218.15) * mm});
            skLineSegment(sketch, "E1632", {"start": v(104, -218.15) * mm, "end": v(105.3, -218.06) * mm});
            skLineSegment(sketch, "E1633", {"start": v(105.3, -218.06) * mm, "end": v(106.59, -217.8) * mm});
            skLineSegment(sketch, "E1634", {"start": v(106.59, -217.8) * mm, "end": v(107.83, -217.39) * mm});
            skLineSegment(sketch, "E1635", {"start": v(107.83, -217.39) * mm, "end": v(109, -216.81) * mm});
            skLineSegment(sketch, "E1636", {"start": v(109, -216.81) * mm, "end": v(110.09, -216.08) * mm});
            skLineSegment(sketch, "E1637", {"start": v(110.09, -216.08) * mm, "end": v(111.07, -215.22) * mm});
            skLineSegment(sketch, "E1638", {"start": v(111.07, -215.22) * mm, "end": v(111.93, -214.24) * mm});
            skLineSegment(sketch, "E1639", {"start": v(111.93, -214.24) * mm, "end": v(112.66, -213.15) * mm});
            skLineSegment(sketch, "E1640", {"start": v(112.66, -213.15) * mm, "end": v(113.24, -211.98) * mm});
            skLineSegment(sketch, "E1641", {"start": v(113.24, -211.98) * mm, "end": v(113.66, -210.74) * mm});
            skLineSegment(sketch, "E1642", {"start": v(113.66, -210.74) * mm, "end": v(113.91, -209.46) * mm});
            skLineSegment(sketch, "E1643", {"start": v(113.91, -209.46) * mm, "end": v(114, -208.15) * mm});
            skLineSegment(sketch, "E1644", {"start": v(30, 243.15) * mm, "end": v(20, 243.15) * mm});
            skLineSegment(sketch, "E1645", {"start": v(144, -248.15) * mm, "end": v(144, -222.15) * mm});
            skLineSegment(sketch, "E1646", {"start": v(-138, -68.05) * mm, "end": v(-135, -68.05) * mm});
            skLineSegment(sketch, "E1647", {"start": v(84, -243.15) * mm, "end": v(84, -237.15) * mm});
            skLineSegment(sketch, "E1648", {"start": v(-74, -243.15) * mm, "end": v(-74, -237.15) * mm});
            skLineSegment(sketch, "E1649", {"start": v(-150, 94.05) * mm, "end": v(-150, 84.05) * mm});
            skLineSegment(sketch, "E1650", {"start": v(-133, 62.55) * mm, "end": v(-133, 65.55) * mm});
            skLineSegment(sketch, "E1651", {"start": v(-135, 62.55) * mm, "end": v(-135, 60.05) * mm});
            skLineSegment(sketch, "E1652", {"start": v(-138, 65.55) * mm, "end": v(-138, 68.05) * mm});
            skLineSegment(sketch, "E1653", {"start": v(-144, 34.05) * mm, "end": v(-144, -34.05) * mm});
            skLineSegment(sketch, "E1654", {"start": v(-144, -222.15) * mm, "end": v(-144, -248.15) * mm});
            skLineSegment(sketch, "E1655", {"start": v(-138, -65.55) * mm, "end": v(-138, -68.05) * mm});
            skLineSegment(sketch, "E1656", {"start": v(-138, -62.55) * mm, "end": v(-138, -60.05) * mm});
            skLineSegment(sketch, "E1657", {"start": v(-135, -62.55) * mm, "end": v(-135, -60.05) * mm});
            skLineSegment(sketch, "E1658", {"start": v(-144, -94.05) * mm, "end": v(-150, -94.05) * mm});
            skLineSegment(sketch, "E1659", {"start": v(-150, -84.05) * mm, "end": v(-150, -94.05) * mm});
            skLineSegment(sketch, "E1660", {"start": v(-135, -62.55) * mm, "end": v(-133, -62.55) * mm});
            skLineSegment(sketch, "E1661", {"start": v(-144, -34.05) * mm, "end": v(-150, -34.05) * mm});
            skLineSegment(sketch, "E1662", {"start": v(-144, -84.05) * mm, "end": v(-150, -84.05) * mm});
            skLineSegment(sketch, "E1663", {"start": v(-144, -44.05) * mm, "end": v(-150, -44.05) * mm});
            skLineSegment(sketch, "E1664", {"start": v(-12.77, 213.19) * mm, "end": v(-13.47, 214.88) * mm});
            skLineSegment(sketch, "E1665", {"start": v(-13.47, 214.88) * mm, "end": v(-13.71, 216.69) * mm});
            skLineSegment(sketch, "E1666", {"start": v(-13.71, 216.69) * mm, "end": v(-13.47, 218.5) * mm});
            skLineSegment(sketch, "E1667", {"start": v(-13.47, 218.5) * mm, "end": v(-12.77, 220.19) * mm});
            skLineSegment(sketch, "E1668", {"start": v(-12.77, 220.19) * mm, "end": v(-11.66, 221.64) * mm});
            skLineSegment(sketch, "E1669", {"start": v(-11.66, 221.64) * mm, "end": v(-10.21, 222.75) * mm});
            skLineSegment(sketch, "E1670", {"start": v(-10.21, 222.75) * mm, "end": v(-8.52, 223.45) * mm});
            skLineSegment(sketch, "E1671", {"start": v(-8.52, 223.45) * mm, "end": v(-6.71, 223.69) * mm});
            skLineSegment(sketch, "E1672", {"start": v(-6.71, 223.69) * mm, "end": v(-5.76, 223.56) * mm});
            skLineSegment(sketch, "E1673", {"start": v(-5.76, 223.56) * mm, "end": v(-4.9, 223.45) * mm});
            skLineSegment(sketch, "E1674", {"start": v(-4.9, 223.45) * mm, "end": v(-3.21, 222.75) * mm});
            skLineSegment(sketch, "E1675", {"start": v(-3.21, 222.75) * mm, "end": v(-1.76, 221.64) * mm});
            skLineSegment(sketch, "E1676", {"start": v(-1.76, 221.64) * mm, "end": v(-0.65, 220.19) * mm});
            skLineSegment(sketch, "E1677", {"start": v(-0.65, 220.19) * mm, "end": v(0.05, 218.5) * mm});
            skLineSegment(sketch, "E1678", {"start": v(0.05, 218.5) * mm, "end": v(0.29, 216.69) * mm});
            skLineSegment(sketch, "E1679", {"start": v(0.29, 216.69) * mm, "end": v(0.05, 214.88) * mm});
            skLineSegment(sketch, "E1680", {"start": v(0.05, 214.88) * mm, "end": v(-0.65, 213.19) * mm});
            skLineSegment(sketch, "E1681", {"start": v(-0.65, 213.19) * mm, "end": v(-1.76, 211.74) * mm});
            skLineSegment(sketch, "E1682", {"start": v(-1.76, 211.74) * mm, "end": v(-3.21, 210.63) * mm});
            skLineSegment(sketch, "E1683", {"start": v(-3.21, 210.63) * mm, "end": v(-4.9, 209.93) * mm});
            skLineSegment(sketch, "E1684", {"start": v(-4.9, 209.93) * mm, "end": v(-5.76, 209.81) * mm});
            skLineSegment(sketch, "E1685", {"start": v(-5.76, 209.81) * mm, "end": v(-6.71, 209.69) * mm});
            skLineSegment(sketch, "E1686", {"start": v(-6.71, 209.69) * mm, "end": v(-8.52, 209.93) * mm});
            skLineSegment(sketch, "E1687", {"start": v(-8.52, 209.93) * mm, "end": v(-10.21, 210.63) * mm});
            skLineSegment(sketch, "E1688", {"start": v(-10.21, 210.63) * mm, "end": v(-11.66, 211.74) * mm});
            skLineSegment(sketch, "E1689", {"start": v(-11.66, 211.74) * mm, "end": v(-12.77, 213.19) * mm});
            skLineSegment(sketch, "E1690", {"start": v(-135, -65.55) * mm, "end": v(-135, -68.05) * mm});
            skLineSegment(sketch, "E1691", {"start": v(-150, -34.05) * mm, "end": v(-150, -44.05) * mm});
            skLineSegment(sketch, "E1692", {"start": v(-124, -243.15) * mm, "end": v(-124, -237.15) * mm});
            skLineSegment(sketch, "E1693", {"start": v(134, -237.15) * mm, "end": v(124, -237.15) * mm});
            skLineSegment(sketch, "E1694", {"start": v(-30, -237.15) * mm, "end": v(-30, -243.15) * mm});
            skLineSegment(sketch, "E1695", {"start": v(84, -237.15) * mm, "end": v(74, -237.15) * mm});
            skLineSegment(sketch, "E1696", {"start": v(20, -243.15) * mm, "end": v(30, -243.15) * mm});
            skLineSegment(sketch, "E1697", {"start": v(20, -237.15) * mm, "end": v(20, -243.15) * mm});
            skLineSegment(sketch, "E1698", {"start": v(124, -243.15) * mm, "end": v(134, -243.15) * mm});
            skLineSegment(sketch, "E1699", {"start": v(124, -237.15) * mm, "end": v(124, -243.15) * mm});
            skLineSegment(sketch, "E1700", {"start": v(-134, -243.15) * mm, "end": v(-124, -243.15) * mm});
            skLineSegment(sketch, "E1701", {"start": v(-134, -237.15) * mm, "end": v(-134, -243.15) * mm});
            skLineSegment(sketch, "E1702", {"start": v(30, -237.15) * mm, "end": v(20, -237.15) * mm});
            skLineSegment(sketch, "E1703", {"start": v(-20, -237.15) * mm, "end": v(-30, -237.15) * mm});
            skLineSegment(sketch, "E1704", {"start": v(-74, -237.15) * mm, "end": v(-84, -237.15) * mm});
            skLineSegment(sketch, "E1705", {"start": v(-20, -243.15) * mm, "end": v(-20, -237.15) * mm});
            skLineSegment(sketch, "E1706", {"start": v(-30, -243.15) * mm, "end": v(-20, -243.15) * mm});
            skLineSegment(sketch, "E1707", {"start": v(129, 209.69) * mm, "end": v(120.5, 209.69) * mm});
            skLineSegment(sketch, "E1708", {"start": v(129, 223.69) * mm, "end": v(129, 209.69) * mm});
            skLineSegment(sketch, "E1709", {"start": v(120.73, 223.69) * mm, "end": v(129, 223.69) * mm});
            skLineSegment(sketch, "E1710", {"start": v(144, 162.15) * mm, "end": v(144, 94.05) * mm});
            skLineSegment(sketch, "E1711", {"start": v(138, -65.55) * mm, "end": v(138, -68.05) * mm});
            skLineSegment(sketch, "E1712", {"start": v(135, -65.55) * mm, "end": v(133, -65.55) * mm});
            skLineSegment(sketch, "E1713", {"start": v(150, -44.05) * mm, "end": v(150, -34.05) * mm});
            skLineSegment(sketch, "E1714", {"start": v(144, -84.05) * mm, "end": v(150, -84.05) * mm});
            skLineSegment(sketch, "E1715", {"start": v(144, -65.55) * mm, "end": v(138, -65.55) * mm});
            skLineSegment(sketch, "E1716", {"start": v(144, -34.05) * mm, "end": v(150, -34.05) * mm});
            skLineSegment(sketch, "E1717", {"start": v(144, -94.05) * mm, "end": v(150, -94.05) * mm});
            skLineSegment(sketch, "E1718", {"start": v(135, -62.55) * mm, "end": v(133, -62.55) * mm});
            skLineSegment(sketch, "E1719", {"start": v(144, -44.05) * mm, "end": v(150, -44.05) * mm});
            skLineSegment(sketch, "E1720", {"start": v(133, -62.55) * mm, "end": v(133, -65.55) * mm});
            skLineSegment(sketch, "E1721", {"start": v(144, -84.05) * mm, "end": v(144, -65.55) * mm});
            skLineSegment(sketch, "E1722", {"start": v(144, -62.55) * mm, "end": v(138, -62.55) * mm});
            skLineSegment(sketch, "E1723", {"start": v(138, -68.05) * mm, "end": v(135, -68.05) * mm});
            skLineSegment(sketch, "E1724", {"start": v(135, -62.55) * mm, "end": v(135, -60.05) * mm});
            skLineSegment(sketch, "E1725", {"start": v(144, -62.55) * mm, "end": v(144, -44.05) * mm});
            skLineSegment(sketch, "E1726", {"start": v(138, -60.05) * mm, "end": v(135, -60.05) * mm});
            skLineSegment(sketch, "E1727", {"start": v(150, -84.05) * mm, "end": v(150, -94.05) * mm});
            skLineSegment(sketch, "E1728", {"start": v(135, -65.55) * mm, "end": v(135, -68.05) * mm});
            skLineSegment(sketch, "E1729", {"start": v(138, -62.55) * mm, "end": v(138, -60.05) * mm});
            skLineSegment(sketch, "E1730", {"start": v(144, -162.15) * mm, "end": v(144, -94.05) * mm});
            skLineSegment(sketch, "E1731", {"start": v(144, -212.15) * mm, "end": v(150, -212.15) * mm});
            skLineSegment(sketch, "E1732", {"start": v(150, -212.15) * mm, "end": v(150, -222.15) * mm});
            skLineSegment(sketch, "E1733", {"start": v(144, -162.15) * mm, "end": v(150, -162.15) * mm});
            skLineSegment(sketch, "E1734", {"start": v(144, -193.65) * mm, "end": v(138, -193.65) * mm});
            skLineSegment(sketch, "E1735", {"start": v(135, -190.65) * mm, "end": v(135, -188.15) * mm});
            skLineSegment(sketch, "E1736", {"start": v(135, -193.65) * mm, "end": v(135, -196.15) * mm});
            skLineSegment(sketch, "E1737", {"start": v(138, -190.65) * mm, "end": v(138, -188.15) * mm});
            skLineSegment(sketch, "E1738", {"start": v(133, -190.65) * mm, "end": v(133, -193.65) * mm});
            skLineSegment(sketch, "E1739", {"start": v(144, -172.15) * mm, "end": v(150, -172.15) * mm});
            skLineSegment(sketch, "E1740", {"start": v(138, -196.15) * mm, "end": v(135, -196.15) * mm});
            skLineSegment(sketch, "E1741", {"start": v(144, -222.15) * mm, "end": v(150, -222.15) * mm});
            skLineSegment(sketch, "E1742", {"start": v(150, -172.15) * mm, "end": v(150, -162.15) * mm});
            skLineSegment(sketch, "E1743", {"start": v(135, -190.65) * mm, "end": v(133, -190.65) * mm});
            skLineSegment(sketch, "E1744", {"start": v(144, -190.65) * mm, "end": v(138, -190.65) * mm});
            skLineSegment(sketch, "E1745", {"start": v(138, -188.15) * mm, "end": v(135, -188.15) * mm});
            skLineSegment(sketch, "E1746", {"start": v(144, -212.15) * mm, "end": v(144, -193.65) * mm});
            skLineSegment(sketch, "E1747", {"start": v(138, -193.65) * mm, "end": v(138, -196.15) * mm});
            skLineSegment(sketch, "E1748", {"start": v(144, -190.65) * mm, "end": v(144, -172.15) * mm});
            skLineSegment(sketch, "E1749", {"start": v(135, -193.65) * mm, "end": v(133, -193.65) * mm});
            skLineSegment(sketch, "E1750", {"start": v(-144, -248.15) * mm, "end": v(144, -248.15) * mm});
            skLineSegment(sketch, "E1751", {"start": v(-135, 65.55) * mm, "end": v(-135, 68.05) * mm});
            skLineSegment(sketch, "E1752", {"start": v(-144, 62.55) * mm, "end": v(-138, 62.55) * mm});
            skLineSegment(sketch, "E1753", {"start": v(-144, 84.05) * mm, "end": v(-150, 84.05) * mm});
            skLineSegment(sketch, "E1754", {"start": v(-144, 62.55) * mm, "end": v(-144, 44.05) * mm});
            skLineSegment(sketch, "E1755", {"start": v(-150, 44.05) * mm, "end": v(-150, 34.05) * mm});
            skLineSegment(sketch, "E1756", {"start": v(-144, 44.05) * mm, "end": v(-150, 44.05) * mm});
            skLineSegment(sketch, "E1757", {"start": v(-138, 65.55) * mm, "end": v(-144, 65.55) * mm});
            skLineSegment(sketch, "E1758", {"start": v(-144, 34.05) * mm, "end": v(-150, 34.05) * mm});
            skLineSegment(sketch, "E1759", {"start": v(-138, 62.55) * mm, "end": v(-138, 60.05) * mm});
            skLineSegment(sketch, "E1760", {"start": v(-144, 84.05) * mm, "end": v(-144, 65.55) * mm});
            skLineSegment(sketch, "E1761", {"start": v(-138, 60.05) * mm, "end": v(-135, 60.05) * mm});
            skLineSegment(sketch, "E1762", {"start": v(-144, 94.05) * mm, "end": v(-150, 94.05) * mm});
            skLineSegment(sketch, "E1763", {"start": v(-124, -237.15) * mm, "end": v(-134, -237.15) * mm});
            skLineSegment(sketch, "E1764", {"start": v(-135, -65.55) * mm, "end": v(-133, -65.55) * mm});
            skLineSegment(sketch, "E1765", {"start": v(-133, -65.55) * mm, "end": v(-133, -62.55) * mm});
            skLineSegment(sketch, "E1766", {"start": v(-144, -62.55) * mm, "end": v(-138, -62.55) * mm});
            skLineSegment(sketch, "E1767", {"start": v(-144, -65.55) * mm, "end": v(-138, -65.55) * mm});
            skLineSegment(sketch, "E1768", {"start": v(-144, -44.05) * mm, "end": v(-144, -62.55) * mm});
            skLineSegment(sketch, "E1769", {"start": v(-144, -65.55) * mm, "end": v(-144, -84.05) * mm});
            skLineSegment(sketch, "E1770", {"start": v(-138, -60.05) * mm, "end": v(-135, -60.05) * mm});
            skLineSegment(sketch, "E1771", {"start": v(-144, -94.05) * mm, "end": v(-144, -162.15) * mm});
            skLineSegment(sketch, "E1772", {"start": v(-144, -222.15) * mm, "end": v(-150, -222.15) * mm});
            skLineSegment(sketch, "E1773", {"start": v(-144, -190.65) * mm, "end": v(-138, -190.65) * mm});
            skLineSegment(sketch, "E1774", {"start": v(-150, -162.15) * mm, "end": v(-150, -172.15) * mm});
            skLineSegment(sketch, "E1775", {"start": v(-144, -212.15) * mm, "end": v(-150, -212.15) * mm});
            skLineSegment(sketch, "E1776", {"start": v(-138, -193.65) * mm, "end": v(-138, -196.15) * mm});
            skLineSegment(sketch, "E1777", {"start": v(-138, -196.15) * mm, "end": v(-135, -196.15) * mm});
            skLineSegment(sketch, "E1778", {"start": v(-135, -193.65) * mm, "end": v(-135, -196.15) * mm});
            skLineSegment(sketch, "E1779", {"start": v(-135, -193.65) * mm, "end": v(-133, -193.65) * mm});
            skLineSegment(sketch, "E1780", {"start": v(-135, -190.65) * mm, "end": v(-133, -190.65) * mm});
            skLineSegment(sketch, "E1781", {"start": v(-138, -188.15) * mm, "end": v(-135, -188.15) * mm});
            skLineSegment(sketch, "E1782", {"start": v(-138, -190.65) * mm, "end": v(-138, -188.15) * mm});
            skLineSegment(sketch, "E1783", {"start": v(-144, -172.15) * mm, "end": v(-150, -172.15) * mm});
            skLineSegment(sketch, "E1784", {"start": v(-144, -193.65) * mm, "end": v(-138, -193.65) * mm});
            skLineSegment(sketch, "E1785", {"start": v(-144, -172.15) * mm, "end": v(-144, -190.65) * mm});
            skLineSegment(sketch, "E1786", {"start": v(-144, -162.15) * mm, "end": v(-150, -162.15) * mm});
            skLineSegment(sketch, "E1787", {"start": v(-144, -193.65) * mm, "end": v(-144, -212.15) * mm});
            skLineSegment(sketch, "E1788", {"start": v(-135, -190.65) * mm, "end": v(-135, -188.15) * mm});
            skLineSegment(sketch, "E1789", {"start": v(-150, -212.15) * mm, "end": v(-150, -222.15) * mm});
            skLineSegment(sketch, "E1790", {"start": v(-144, 248.15) * mm, "end": v(-144, 222.15) * mm});
            skLineSegment(sketch, "E1791", {"start": v(-138, 68.05) * mm, "end": v(-135, 68.05) * mm});
            skLineSegment(sketch, "E1792", {"start": v(-135, 65.55) * mm, "end": v(-133, 65.55) * mm});
            skLineSegment(sketch, "E1793", {"start": v(-135, 62.55) * mm, "end": v(-133, 62.55) * mm});
            skLineSegment(sketch, "E1794", {"start": v(-133, -193.65) * mm, "end": v(-133, -190.65) * mm});
            skLineSegment(sketch, "E1795", {"start": v(-135, 190.65) * mm, "end": v(-135, 188.15) * mm});
            skLineSegment(sketch, "E1796", {"start": v(-133, 190.65) * mm, "end": v(-133, 193.65) * mm});
            skLineSegment(sketch, "E1797", {"start": v(-138, 196.15) * mm, "end": v(-135, 196.15) * mm});
            skLineSegment(sketch, "E1798", {"start": v(-144, 212.15) * mm, "end": v(-144, 193.65) * mm});
            skLineSegment(sketch, "E1799", {"start": v(-138, 193.65) * mm, "end": v(-138, 196.15) * mm});
            skLineSegment(sketch, "E1800", {"start": v(-144, 162.15) * mm, "end": v(-150, 162.15) * mm});
            skLineSegment(sketch, "E1801", {"start": v(-150, 222.15) * mm, "end": v(-150, 212.15) * mm});
            skLineSegment(sketch, "E1802", {"start": v(-138, 188.15) * mm, "end": v(-135, 188.15) * mm});
            skLineSegment(sketch, "E1803", {"start": v(-144, 222.15) * mm, "end": v(-150, 222.15) * mm});
            skLineSegment(sketch, "E1804", {"start": v(-135, 190.65) * mm, "end": v(-133, 190.65) * mm});
            skLineSegment(sketch, "E1805", {"start": v(-144, 190.65) * mm, "end": v(-138, 190.65) * mm});
            skLineSegment(sketch, "E1806", {"start": v(-150, 172.15) * mm, "end": v(-150, 162.15) * mm});
            skLineSegment(sketch, "E1807", {"start": v(-144, 212.15) * mm, "end": v(-150, 212.15) * mm});
            skLineSegment(sketch, "E1808", {"start": v(-135, 193.65) * mm, "end": v(-135, 196.15) * mm});
            skLineSegment(sketch, "E1809", {"start": v(-144, 190.65) * mm, "end": v(-144, 172.15) * mm});
            skLineSegment(sketch, "E1810", {"start": v(-138, 190.65) * mm, "end": v(-138, 188.15) * mm});
            skLineSegment(sketch, "E1811", {"start": v(-135, 193.65) * mm, "end": v(-133, 193.65) * mm});
            skLineSegment(sketch, "E1812", {"start": v(-138, 193.65) * mm, "end": v(-144, 193.65) * mm});
            skLineSegment(sketch, "E1813", {"start": v(-144, 172.15) * mm, "end": v(-150, 172.15) * mm});
            skLineSegment(sketch, "E1814", {"start": v(-144, 162.15) * mm, "end": v(-144, 94.05) * mm});
            skLineSegment(sketch, "E1815", {"start": v(144, 84.05) * mm, "end": v(150, 84.05) * mm});
            skLineSegment(sketch, "E1816", {"start": v(150, 44.05) * mm, "end": v(150, 34.05) * mm});
            skLineSegment(sketch, "E1817", {"start": v(138, 62.55) * mm, "end": v(138, 60.05) * mm});
            skLineSegment(sketch, "E1818", {"start": v(135, 62.55) * mm, "end": v(135, 60.05) * mm});
            skLineSegment(sketch, "E1819", {"start": v(144, 94.05) * mm, "end": v(150, 94.05) * mm});
            skLineSegment(sketch, "E1820", {"start": v(144, 34.05) * mm, "end": v(150, 34.05) * mm});
            skLineSegment(sketch, "E1821", {"start": v(144, 44.05) * mm, "end": v(150, 44.05) * mm});
            skLineSegment(sketch, "E1822", {"start": v(135, 65.55) * mm, "end": v(135, 68.05) * mm});
            skLineSegment(sketch, "E1823", {"start": v(144, 44.05) * mm, "end": v(144, 62.55) * mm});
            skLineSegment(sketch, "E1824", {"start": v(144, 65.55) * mm, "end": v(138, 65.55) * mm});
            skLineSegment(sketch, "E1825", {"start": v(150, 84.05) * mm, "end": v(150, 94.05) * mm});
            skLineSegment(sketch, "E1826", {"start": v(135, 62.55) * mm, "end": v(133, 62.55) * mm});
            skLineSegment(sketch, "E1827", {"start": v(144, 65.55) * mm, "end": v(144, 84.05) * mm});
            skLineSegment(sketch, "E1828", {"start": v(144, 62.55) * mm, "end": v(138, 62.55) * mm});
            skLineSegment(sketch, "E1829", {"start": v(138, 60.05) * mm, "end": v(135, 60.05) * mm});
            skLineSegment(sketch, "E1830", {"start": v(133, 65.55) * mm, "end": v(133, 62.55) * mm});
            skLineSegment(sketch, "E1831", {"start": v(135, 65.55) * mm, "end": v(133, 65.55) * mm});
            skLineSegment(sketch, "E1832", {"start": v(138, 68.05) * mm, "end": v(135, 68.05) * mm});
            skLineSegment(sketch, "E1833", {"start": v(138, 65.55) * mm, "end": v(138, 68.05) * mm});
            skLineSegment(sketch, "E1834", {"start": v(120.5, 209.69) * mm, "end": v(120.73, 223.69) * mm});
            skPoint(sketch, "E1835.0", {"position": v(-20, 237.15) * mm});
            skSolve(sketch);
        }
        {
            var Q0;
            Q0 = qSketchRegion(id + "F13", true);
            extrude(context, id + "F14", {"entities" : qUnion([Q0]), "depth" : 6 * mm, "offsetDistance" : 25 * mm});
        }
        {
            var Q0;
            Q0=makeQuery(id+"F3.opExtrude","SWEPT_FACE",FACE,{"disambiguationData":[OSD([sQuery(id+"F2.wireOp",EDGE,"E113")])]});
            cPlane(context, id + "F15", {"entities" : qUnion([Q0]), "cplaneType" : CPlaneType.OFFSET, "offset" : 0 * mm, "width" : 150 * mm, "height" : 150 * mm});
        }
        {
            var Q0;
            Q0=qCreatedBy(id+"F15.planeOp",FACE);
            var sketch = newSketch(context, id + "F16", { "sketchPlane" : qUnion([Q0])});
            skCircle(sketch, "E1836", {"center": v(87.61, -208.48) * mm, "radius": 1.5 * mm});
            skCircle(sketch, "E1837", {"center": v(-5.5, -96.15) * mm, "radius": 2 * mm});
            skLineSegment(sketch, "E1838", {"start": v(-144, 190.65) * mm, "end": v(-138, 190.65) * mm});
            skLineSegment(sketch, "E1839", {"start": v(-105.5, 237.15) * mm, "end": v(-105.5, 231.15) * mm});
            skLineSegment(sketch, "E1840", {"start": v(-134, -243.15) * mm, "end": v(-134, -237.15) * mm});
            skLineSegment(sketch, "E1841", {"start": v(-124, -237.15) * mm, "end": v(-124, -243.15) * mm});
            skLineSegment(sketch, "E1842", {"start": v(-134, -237.15) * mm, "end": v(-144, -237.15) * mm});
            skLineSegment(sketch, "E1843", {"start": v(-105.5, 228.15) * mm, "end": v(-108, 228.15) * mm});
            skLineSegment(sketch, "E1844", {"start": v(-105.5, 228.15) * mm, "end": v(-105.5, 226.15) * mm});
            skLineSegment(sketch, "E1845", {"start": v(-144, -222.15) * mm, "end": v(-150, -222.15) * mm});
            skLineSegment(sketch, "E1846", {"start": v(-150, -172.15) * mm, "end": v(-150, -162.15) * mm});
            skLineSegment(sketch, "E1847", {"start": v(-138, -196.15) * mm, "end": v(-135, -196.15) * mm});
            skLineSegment(sketch, "E1848", {"start": v(-135, -193.65) * mm, "end": v(-135, -196.15) * mm});
            skLineSegment(sketch, "E1849", {"start": v(144, -65.55) * mm, "end": v(144, -84.05) * mm});
            skLineSegment(sketch, "E1850", {"start": v(-138, 60.05) * mm, "end": v(-135, 60.05) * mm});
            skLineSegment(sketch, "E1851", {"start": v(-135, 62.55) * mm, "end": v(-135, 60.05) * mm});
            skLineSegment(sketch, "E1852", {"start": v(-144, -162.15) * mm, "end": v(-150, -162.15) * mm});
            skLineSegment(sketch, "E1853", {"start": v(-144, -190.65) * mm, "end": v(-138, -190.65) * mm});
            skLineSegment(sketch, "E1854", {"start": v(-144, -193.65) * mm, "end": v(-138, -193.65) * mm});
            skLineSegment(sketch, "E1855", {"start": v(-144, -212.15) * mm, "end": v(-150, -212.15) * mm});
            skLineSegment(sketch, "E1856", {"start": v(-150, -222.15) * mm, "end": v(-150, -212.15) * mm});
            skLineSegment(sketch, "E1857", {"start": v(-144, -172.15) * mm, "end": v(-150, -172.15) * mm});
            skLineSegment(sketch, "E1858", {"start": v(-4, 231.15) * mm, "end": v(-4, 228.15) * mm});
            skLineSegment(sketch, "E1859", {"start": v(-1.5, 228.15) * mm, "end": v(-4, 228.15) * mm});
            skLineSegment(sketch, "E1860", {"start": v(-1.5, 228.15) * mm, "end": v(-1.5, 226.15) * mm});
            skLineSegment(sketch, "E1861", {"start": v(-1.5, 226.15) * mm, "end": v(1.5, 226.15) * mm});
            skLineSegment(sketch, "E1862", {"start": v(1.5, 228.15) * mm, "end": v(1.5, 226.15) * mm});
            skLineSegment(sketch, "E1863", {"start": v(1.5, 228.15) * mm, "end": v(4, 228.15) * mm});
            skLineSegment(sketch, "E1864", {"start": v(4, 231.15) * mm, "end": v(4, 228.15) * mm});
            skLineSegment(sketch, "E1865", {"start": v(-20, 237.15) * mm, "end": v(-1.5, 237.15) * mm});
            skLineSegment(sketch, "E1866", {"start": v(-134, -243.15) * mm, "end": v(-124, -243.15) * mm});
            skLineSegment(sketch, "E1867", {"start": v(100, -231.15) * mm, "end": v(100, -228.15) * mm});
            skLineSegment(sketch, "E1868", {"start": v(102.5, -231.15) * mm, "end": v(100, -231.15) * mm});
            skLineSegment(sketch, "E1869", {"start": v(144, -237.15) * mm, "end": v(134, -237.15) * mm});
            skLineSegment(sketch, "E1870", {"start": v(124, -237.15) * mm, "end": v(105.5, -237.15) * mm});
            skLineSegment(sketch, "E1871", {"start": v(-1.5, -228.15) * mm, "end": v(-4, -228.15) * mm});
            skLineSegment(sketch, "E1872", {"start": v(-4, -231.15) * mm, "end": v(-4, -228.15) * mm});
            skLineSegment(sketch, "E1873", {"start": v(-1.5, -231.15) * mm, "end": v(-4, -231.15) * mm});
            skLineSegment(sketch, "E1874", {"start": v(102.5, -237.15) * mm, "end": v(84, -237.15) * mm});
            skLineSegment(sketch, "E1875", {"start": v(105.5, -231.15) * mm, "end": v(108, -231.15) * mm});
            skLineSegment(sketch, "E1876", {"start": v(108, -231.15) * mm, "end": v(108, -228.15) * mm});
            skLineSegment(sketch, "E1877", {"start": v(105.5, -228.15) * mm, "end": v(108, -228.15) * mm});
            skLineSegment(sketch, "E1878", {"start": v(105.5, -228.15) * mm, "end": v(105.5, -226.15) * mm});
            skLineSegment(sketch, "E1879", {"start": v(102.5, -226.15) * mm, "end": v(105.5, -226.15) * mm});
            skLineSegment(sketch, "E1880", {"start": v(102.5, -228.15) * mm, "end": v(102.5, -226.15) * mm});
            skLineSegment(sketch, "E1881", {"start": v(102.5, -228.15) * mm, "end": v(100, -228.15) * mm});
            skLineSegment(sketch, "E1882", {"start": v(138, -196.15) * mm, "end": v(135, -196.15) * mm});
            skLineSegment(sketch, "E1883", {"start": v(135, -190.65) * mm, "end": v(135, -188.15) * mm});
            skLineSegment(sketch, "E1884", {"start": v(144, -190.65) * mm, "end": v(138, -190.65) * mm});
            skLineSegment(sketch, "E1885", {"start": v(138, -188.15) * mm, "end": v(135, -188.15) * mm});
            skLineSegment(sketch, "E1886", {"start": v(133, -193.65) * mm, "end": v(133, -190.65) * mm});
            skLineSegment(sketch, "E1887", {"start": v(74, -237.15) * mm, "end": v(30, -237.15) * mm});
            skLineSegment(sketch, "E1888", {"start": v(84, -243.15) * mm, "end": v(74, -243.15) * mm});
            skLineSegment(sketch, "E1889", {"start": v(74, -237.15) * mm, "end": v(74, -243.15) * mm});
            skLineSegment(sketch, "E1890", {"start": v(84, -237.15) * mm, "end": v(84, -243.15) * mm});
            skLineSegment(sketch, "E1891", {"start": v(134, -243.15) * mm, "end": v(124, -243.15) * mm});
            skLineSegment(sketch, "E1892", {"start": v(124, -237.15) * mm, "end": v(124, -243.15) * mm});
            skLineSegment(sketch, "E1893", {"start": v(134, -237.15) * mm, "end": v(134, -243.15) * mm});
            skLineSegment(sketch, "E1894", {"start": v(20, -237.15) * mm, "end": v(1.5, -237.15) * mm});
            skLineSegment(sketch, "E1895", {"start": v(30, -243.15) * mm, "end": v(20, -243.15) * mm});
            skLineSegment(sketch, "E1896", {"start": v(20, -237.15) * mm, "end": v(20, -243.15) * mm});
            skLineSegment(sketch, "E1897", {"start": v(30, -237.15) * mm, "end": v(30, -243.15) * mm});
            skLineSegment(sketch, "E1898", {"start": v(-30, -237.15) * mm, "end": v(-74, -237.15) * mm});
            skLineSegment(sketch, "E1899", {"start": v(-20, -243.15) * mm, "end": v(-30, -243.15) * mm});
            skLineSegment(sketch, "E1900", {"start": v(-30, -237.15) * mm, "end": v(-30, -243.15) * mm});
            skLineSegment(sketch, "E1901", {"start": v(-20, -237.15) * mm, "end": v(-20, -243.15) * mm});
            skLineSegment(sketch, "E1902", {"start": v(-84, -237.15) * mm, "end": v(-102.5, -237.15) * mm});
            skLineSegment(sketch, "E1903", {"start": v(-74, -243.15) * mm, "end": v(-84, -243.15) * mm});
            skLineSegment(sketch, "E1904", {"start": v(144, 190.65) * mm, "end": v(138, 190.65) * mm});
            skLineSegment(sketch, "E1905", {"start": v(144, 162.15) * mm, "end": v(150, 162.15) * mm});
            skLineSegment(sketch, "E1906", {"start": v(144, 172.15) * mm, "end": v(150, 172.15) * mm});
            skLineSegment(sketch, "E1907", {"start": v(135, 193.65) * mm, "end": v(135, 196.15) * mm});
            skLineSegment(sketch, "E1908", {"start": v(135, 190.65) * mm, "end": v(133, 190.65) * mm});
            skLineSegment(sketch, "E1909", {"start": v(135, 190.65) * mm, "end": v(135, 188.15) * mm});
            skLineSegment(sketch, "E1910", {"start": v(144, 62.55) * mm, "end": v(138, 62.55) * mm});
            skLineSegment(sketch, "E1911", {"start": v(144, 34.05) * mm, "end": v(150, 34.05) * mm});
            skLineSegment(sketch, "E1912", {"start": v(135, 62.55) * mm, "end": v(135, 60.05) * mm});
            skLineSegment(sketch, "E1913", {"start": v(138, 68.05) * mm, "end": v(135, 68.05) * mm});
            skLineSegment(sketch, "E1914", {"start": v(138, 65.55) * mm, "end": v(138, 68.05) * mm});
            skLineSegment(sketch, "E1915", {"start": v(135, 65.55) * mm, "end": v(135, 68.05) * mm});
            skLineSegment(sketch, "E1916", {"start": v(144, 44.05) * mm, "end": v(150, 44.05) * mm});
            skLineSegment(sketch, "E1917", {"start": v(-102.5, -231.15) * mm, "end": v(-100, -231.15) * mm});
            skLineSegment(sketch, "E1918", {"start": v(-100, -231.15) * mm, "end": v(-100, -228.15) * mm});
            skLineSegment(sketch, "E1919", {"start": v(-102.5, -228.15) * mm, "end": v(-100, -228.15) * mm});
            skLineSegment(sketch, "E1920", {"start": v(-105.5, -228.15) * mm, "end": v(-105.5, -226.15) * mm});
            skLineSegment(sketch, "E1921", {"start": v(-105.5, -228.15) * mm, "end": v(-108, -228.15) * mm});
            skLineSegment(sketch, "E1922", {"start": v(-108, -231.15) * mm, "end": v(-108, -228.15) * mm});
            skLineSegment(sketch, "E1923", {"start": v(-105.5, -231.15) * mm, "end": v(-108, -231.15) * mm});
            skLineSegment(sketch, "E1924", {"start": v(-1.5, -237.15) * mm, "end": v(-20, -237.15) * mm});
            skLineSegment(sketch, "E1925", {"start": v(-144, -34.05) * mm, "end": v(-144, 34.05) * mm});
            skLineSegment(sketch, "E1926", {"start": v(144, 34.05) * mm, "end": v(144, -34.05) * mm});
            skLineSegment(sketch, "E1927", {"start": v(102.5, -237.15) * mm, "end": v(102.5, -231.15) * mm});
            skLineSegment(sketch, "E1928", {"start": v(-105.5, -237.15) * mm, "end": v(-105.5, -231.15) * mm});
            skLineSegment(sketch, "E1929", {"start": v(1.5, -237.15) * mm, "end": v(1.5, -231.15) * mm});
            skLineSegment(sketch, "E1930", {"start": v(-1.5, -237.15) * mm, "end": v(-1.5, -231.15) * mm});
            skLineSegment(sketch, "E1931", {"start": v(105.5, -237.15) * mm, "end": v(105.5, -231.15) * mm});
            skLineSegment(sketch, "E1932", {"start": v(-102.5, -237.15) * mm, "end": v(-102.5, -231.15) * mm});
            skLineSegment(sketch, "E1933", {"start": v(1.5, 231.15) * mm, "end": v(4, 231.15) * mm});
            skLineSegment(sketch, "E1934", {"start": v(1.5, 237.15) * mm, "end": v(1.5, 231.15) * mm});
            skLineSegment(sketch, "E1935", {"start": v(-1.5, 237.15) * mm, "end": v(-1.5, 231.15) * mm});
            skLineSegment(sketch, "E1936", {"start": v(-1.5, 231.15) * mm, "end": v(-4, 231.15) * mm});
            skLineSegment(sketch, "E1937", {"start": v(1.5, -231.15) * mm, "end": v(4, -231.15) * mm});
            skLineSegment(sketch, "E1938", {"start": v(4, -231.15) * mm, "end": v(4, -228.15) * mm});
            skLineSegment(sketch, "E1939", {"start": v(1.5, -228.15) * mm, "end": v(4, -228.15) * mm});
            skLineSegment(sketch, "E1940", {"start": v(1.5, -228.15) * mm, "end": v(1.5, -226.15) * mm});
            skLineSegment(sketch, "E1941", {"start": v(-1.5, -226.15) * mm, "end": v(1.5, -226.15) * mm});
            skLineSegment(sketch, "E1942", {"start": v(-1.5, -228.15) * mm, "end": v(-1.5, -226.15) * mm});
            skLineSegment(sketch, "E1943", {"start": v(135, 65.55) * mm, "end": v(133, 65.55) * mm});
            skLineSegment(sketch, "E1944", {"start": v(150, 44.05) * mm, "end": v(150, 34.05) * mm});
            skArc(sketch, "E1945", {"start": v(118, -162.15) * mm, "mid": v(116, -160.15) * mm, "end": v(114, -162.15) * mm});
            skArc(sketch, "E1946", {"start": v(106.1, -198.67) * mm, "mid": v(114.95, -181.35) * mm, "end": v(118, -162.15) * mm});
            skLineSegment(sketch, "E1947", {"start": v(144, -62.55) * mm, "end": v(138, -62.55) * mm});
            skLineSegment(sketch, "E1948", {"start": v(144, 162.15) * mm, "end": v(144, 94.05) * mm});
            skLineSegment(sketch, "E1949", {"start": v(144, 190.65) * mm, "end": v(144, 172.15) * mm});
            skLineSegment(sketch, "E1950", {"start": v(144, 212.15) * mm, "end": v(144, 193.65) * mm});
            skLineSegment(sketch, "E1951", {"start": v(144, 237.15) * mm, "end": v(144, 222.15) * mm});
            skLineSegment(sketch, "E1952", {"start": v(108, 231.15) * mm, "end": v(108, 228.15) * mm});
            skLineSegment(sketch, "E1953", {"start": v(100, 231.15) * mm, "end": v(100, 228.15) * mm});
            skLineSegment(sketch, "E1954", {"start": v(-144, 222.15) * mm, "end": v(-144, 237.15) * mm});
            skLineSegment(sketch, "E1955", {"start": v(-144, 94.05) * mm, "end": v(-144, 162.15) * mm});
            skLineSegment(sketch, "E1956", {"start": v(117.5, 211.96) * mm, "end": v(129.5, 211.96) * mm});
            skLineSegment(sketch, "E1957", {"start": v(129.5, 211.96) * mm, "end": v(129.5, 181.96) * mm});
            skLineSegment(sketch, "E1958", {"start": v(144, -222.15) * mm, "end": v(150, -222.15) * mm});
            skLineSegment(sketch, "E1959", {"start": v(150, -212.15) * mm, "end": v(150, -222.15) * mm});
            skLineSegment(sketch, "E1960", {"start": v(135, -193.65) * mm, "end": v(135, -196.15) * mm});
            skLineSegment(sketch, "E1961", {"start": v(144, -193.65) * mm, "end": v(144, -212.15) * mm});
            skLineSegment(sketch, "E1962", {"start": v(144, -44.05) * mm, "end": v(144, -62.55) * mm});
            skLineSegment(sketch, "E1963", {"start": v(144, -222.15) * mm, "end": v(144, -237.15) * mm});
            skLineSegment(sketch, "E1964", {"start": v(150, -84.05) * mm, "end": v(150, -94.05) * mm});
            skLineSegment(sketch, "E1965", {"start": v(144, -44.05) * mm, "end": v(150, -44.05) * mm});
            skLineSegment(sketch, "E1966", {"start": v(144, -65.55) * mm, "end": v(138, -65.55) * mm});
            skLineSegment(sketch, "E1967", {"start": v(144, -94.05) * mm, "end": v(150, -94.05) * mm});
            skCircle(sketch, "E1968", {"center": v(5.5, -96.15) * mm, "radius": 2 * mm});
            skLineSegment(sketch, "E1969", {"start": v(-144, 65.55) * mm, "end": v(-144, 84.05) * mm});
            skCircle(sketch, "E1970", {"center": v(-130, -57.02) * mm, "radius": 1.5 * mm});
            skLineSegment(sketch, "E1971", {"start": v(144, 94.05) * mm, "end": v(150, 94.05) * mm});
            skLineSegment(sketch, "E1972", {"start": v(133, 62.55) * mm, "end": v(133, 65.55) * mm});
            skLineSegment(sketch, "E1973", {"start": v(135, 62.55) * mm, "end": v(133, 62.55) * mm});
            skLineSegment(sketch, "E1974", {"start": v(138, 62.55) * mm, "end": v(138, 60.05) * mm});
            skLineSegment(sketch, "E1975", {"start": v(144, 84.05) * mm, "end": v(150, 84.05) * mm});
            skLineSegment(sketch, "E1976", {"start": v(150, 94.05) * mm, "end": v(150, 84.05) * mm});
            skLineSegment(sketch, "E1977", {"start": v(144, 65.55) * mm, "end": v(138, 65.55) * mm});
            skLineSegment(sketch, "E1978", {"start": v(138, 60.05) * mm, "end": v(135, 60.05) * mm});
            skLineSegment(sketch, "E1979", {"start": v(144, 62.55) * mm, "end": v(144, 44.05) * mm});
            skLineSegment(sketch, "E1980", {"start": v(144, -172.15) * mm, "end": v(144, -190.65) * mm});
            skCircle(sketch, "E1981", {"center": v(-114.5, -41.5) * mm, "radius": 11 * mm});
            skCircle(sketch, "E1982", {"center": v(-99, -26.02) * mm, "radius": 1.5 * mm});
            skLineSegment(sketch, "E1983", {"start": v(-144, -84.05) * mm, "end": v(-144, -65.55) * mm});
            skLineSegment(sketch, "E1984", {"start": v(-144, -190.65) * mm, "end": v(-144, -172.15) * mm});
            skLineSegment(sketch, "E1985", {"start": v(-144, -212.15) * mm, "end": v(-144, -193.65) * mm});
            skLineSegment(sketch, "E1986", {"start": v(-144, -44.05) * mm, "end": v(-150, -44.05) * mm});
            skLineSegment(sketch, "E1987", {"start": v(-144, -34.05) * mm, "end": v(-150, -34.05) * mm});
            skLineSegment(sketch, "E1988", {"start": v(-124, 237.15) * mm, "end": v(-105.5, 237.15) * mm});
            skLineSegment(sketch, "E1989", {"start": v(84, 237.15) * mm, "end": v(84, 243.15) * mm});
            skLineSegment(sketch, "E1990", {"start": v(84, 237.15) * mm, "end": v(102.5, 237.15) * mm});
            skLineSegment(sketch, "E1991", {"start": v(102.5, 226.15) * mm, "end": v(105.5, 226.15) * mm});
            skLineSegment(sketch, "E1992", {"start": v(-105.5, 231.15) * mm, "end": v(-108, 231.15) * mm});
            skLineSegment(sketch, "E1993", {"start": v(-105.5, 226.15) * mm, "end": v(-102.5, 226.15) * mm});
            skLineSegment(sketch, "E1994", {"start": v(-102.5, 228.15) * mm, "end": v(-102.5, 226.15) * mm});
            skLineSegment(sketch, "E1995", {"start": v(-102.5, 228.15) * mm, "end": v(-100, 228.15) * mm});
            skLineSegment(sketch, "E1996", {"start": v(-100, 231.15) * mm, "end": v(-100, 228.15) * mm});
            skLineSegment(sketch, "E1997", {"start": v(-102.5, 231.15) * mm, "end": v(-100, 231.15) * mm});
            skLineSegment(sketch, "E1998", {"start": v(-102.5, 237.15) * mm, "end": v(-102.5, 231.15) * mm});
            skLineSegment(sketch, "E1999", {"start": v(-124, 237.15) * mm, "end": v(-124, 243.15) * mm});
            skLineSegment(sketch, "E2000", {"start": v(-144, 237.15) * mm, "end": v(-134, 237.15) * mm});
            skLineSegment(sketch, "E2001", {"start": v(-134, 243.15) * mm, "end": v(-134, 237.15) * mm});
            skLineSegment(sketch, "E2002", {"start": v(-150, 84.05) * mm, "end": v(-150, 94.05) * mm});
            skLineSegment(sketch, "E2003", {"start": v(-144, 44.05) * mm, "end": v(-150, 44.05) * mm});
            skCircle(sketch, "E2004", {"center": v(99, -57.02) * mm, "radius": 1.5 * mm});
            skLineSegment(sketch, "E2005", {"start": v(-150, -94.05) * mm, "end": v(-150, -84.05) * mm});
            skLineSegment(sketch, "E2006", {"start": v(-144, -65.55) * mm, "end": v(-138, -65.55) * mm});
            skLineSegment(sketch, "E2007", {"start": v(-150, -44.05) * mm, "end": v(-150, -34.05) * mm});
            skLineSegment(sketch, "E2008", {"start": v(-144, -84.05) * mm, "end": v(-150, -84.05) * mm});
            skLineSegment(sketch, "E2009", {"start": v(-144, -94.05) * mm, "end": v(-150, -94.05) * mm});
            skLineSegment(sketch, "E2010", {"start": v(-144, -162.15) * mm, "end": v(-144, -94.05) * mm});
            skLineSegment(sketch, "E2011", {"start": v(-144, -62.55) * mm, "end": v(-144, -44.05) * mm});
            skLineSegment(sketch, "E2012", {"start": v(-138, -193.65) * mm, "end": v(-138, -196.15) * mm});
            skLineSegment(sketch, "E2013", {"start": v(-84, -237.15) * mm, "end": v(-84, -243.15) * mm});
            skLineSegment(sketch, "E2014", {"start": v(-74, -237.15) * mm, "end": v(-74, -243.15) * mm});
            skLineSegment(sketch, "E2015", {"start": v(134, 237.15) * mm, "end": v(144, 237.15) * mm});
            skLineSegment(sketch, "E2016", {"start": v(144, 84.05) * mm, "end": v(144, 65.55) * mm});
            skLineSegment(sketch, "E2017", {"start": v(-144, 94.05) * mm, "end": v(-150, 94.05) * mm});
            skLineSegment(sketch, "E2018", {"start": v(-135, 65.55) * mm, "end": v(-135, 68.05) * mm});
            skLineSegment(sketch, "E2019", {"start": v(-144, 84.05) * mm, "end": v(-150, 84.05) * mm});
            skLineSegment(sketch, "E2020", {"start": v(-144, 65.55) * mm, "end": v(-138, 65.55) * mm});
            skLineSegment(sketch, "E2021", {"start": v(-144, 62.55) * mm, "end": v(-138, 62.55) * mm});
            skLineSegment(sketch, "E2022", {"start": v(-134, 243.15) * mm, "end": v(-124, 243.15) * mm});
            skLineSegment(sketch, "E2023", {"start": v(134, 237.15) * mm, "end": v(134, 243.15) * mm});
            skLineSegment(sketch, "E2024", {"start": v(124, 237.15) * mm, "end": v(124, 243.15) * mm});
            skLineSegment(sketch, "E2025", {"start": v(102.5, 231.15) * mm, "end": v(100, 231.15) * mm});
            skLineSegment(sketch, "E2026", {"start": v(102.5, 228.15) * mm, "end": v(100, 228.15) * mm});
            skCircle(sketch, "E2027", {"center": v(-99, -57.02) * mm, "radius": 1.5 * mm});
            skLineSegment(sketch, "E2028", {"start": v(-144, 212.15) * mm, "end": v(-150, 212.15) * mm});
            skLineSegment(sketch, "E2029", {"start": v(-138, 188.15) * mm, "end": v(-135, 188.15) * mm});
            skLineSegment(sketch, "E2030", {"start": v(-144, 193.65) * mm, "end": v(-138, 193.65) * mm});
            skLineSegment(sketch, "E2031", {"start": v(-144, 222.15) * mm, "end": v(-150, 222.15) * mm});
            skLineSegment(sketch, "E2032", {"start": v(138, 188.15) * mm, "end": v(135, 188.15) * mm});
            skLineSegment(sketch, "E2033", {"start": v(138, 193.65) * mm, "end": v(138, 196.15) * mm});
            skLineSegment(sketch, "E2034", {"start": v(133, 190.65) * mm, "end": v(133, 193.65) * mm});
            skLineSegment(sketch, "E2035", {"start": v(144, 222.15) * mm, "end": v(150, 222.15) * mm});
            skLineSegment(sketch, "E2036", {"start": v(144, -34.05) * mm, "end": v(150, -34.05) * mm});
            skLineSegment(sketch, "E2037", {"start": v(144, -84.05) * mm, "end": v(150, -84.05) * mm});
            skLineSegment(sketch, "E2038", {"start": v(150, -34.05) * mm, "end": v(150, -44.05) * mm});
            skLineSegment(sketch, "E2039", {"start": v(-102.5, -228.15) * mm, "end": v(-102.5, -226.15) * mm});
            skLineSegment(sketch, "E2040", {"start": v(-102.5, -226.15) * mm, "end": v(-105.5, -226.15) * mm});
            skCircle(sketch, "E2041", {"center": v(123.84, -227.5) * mm, "radius": 1.5 * mm});
            skCircle(sketch, "E2042", {"center": v(94.34, -202.48) * mm, "radius": 1.5 * mm});
            skLineSegment(sketch, "E2043", {"start": v(-135, 193.65) * mm, "end": v(-135, 196.15) * mm});
            skLineSegment(sketch, "E2044", {"start": v(-138, 190.65) * mm, "end": v(-138, 188.15) * mm});
            skLineSegment(sketch, "E2045", {"start": v(-150, 162.15) * mm, "end": v(-150, 172.15) * mm});
            skLineSegment(sketch, "E2046", {"start": v(-135, 193.65) * mm, "end": v(-133, 193.65) * mm});
            skLineSegment(sketch, "E2047", {"start": v(-144, 172.15) * mm, "end": v(-150, 172.15) * mm});
            skLineSegment(sketch, "E2048", {"start": v(-135, -193.65) * mm, "end": v(-133, -193.65) * mm});
            skLineSegment(sketch, "E2049", {"start": v(-133, -190.65) * mm, "end": v(-133, -193.65) * mm});
            skLineSegment(sketch, "E2050", {"start": v(-135, -190.65) * mm, "end": v(-133, -190.65) * mm});
            skLineSegment(sketch, "E2051", {"start": v(-135, -190.65) * mm, "end": v(-135, -188.15) * mm});
            skLineSegment(sketch, "E2052", {"start": v(-138, -188.15) * mm, "end": v(-135, -188.15) * mm});
            skLineSegment(sketch, "E2053", {"start": v(-138, -190.65) * mm, "end": v(-138, -188.15) * mm});
            skLineSegment(sketch, "E2054", {"start": v(-144, -62.55) * mm, "end": v(-138, -62.55) * mm});
            skLineSegment(sketch, "E2055", {"start": v(-144, 34.05) * mm, "end": v(-150, 34.05) * mm});
            skLineSegment(sketch, "E2056", {"start": v(-138, 68.05) * mm, "end": v(-135, 68.05) * mm});
            skLineSegment(sketch, "E2057", {"start": v(-138, -65.55) * mm, "end": v(-138, -68.05) * mm});
            skLineSegment(sketch, "E2058", {"start": v(-138, -68.05) * mm, "end": v(-135, -68.05) * mm});
            skLineSegment(sketch, "E2059", {"start": v(-135, -65.55) * mm, "end": v(-135, -68.05) * mm});
            skLineSegment(sketch, "E2060", {"start": v(-135, -65.55) * mm, "end": v(-133, -65.55) * mm});
            skLineSegment(sketch, "E2061", {"start": v(-133, -62.55) * mm, "end": v(-133, -65.55) * mm});
            skLineSegment(sketch, "E2062", {"start": v(-135, -62.55) * mm, "end": v(-133, -62.55) * mm});
            skLineSegment(sketch, "E2063", {"start": v(-135, -62.55) * mm, "end": v(-135, -60.05) * mm});
            skLineSegment(sketch, "E2064", {"start": v(-138, -60.05) * mm, "end": v(-135, -60.05) * mm});
            skLineSegment(sketch, "E2065", {"start": v(-144, 162.15) * mm, "end": v(-150, 162.15) * mm});
            skLineSegment(sketch, "E2066", {"start": v(-138, 193.65) * mm, "end": v(-138, 196.15) * mm});
            skLineSegment(sketch, "E2067", {"start": v(-133, 193.65) * mm, "end": v(-133, 190.65) * mm});
            skLineSegment(sketch, "E2068", {"start": v(-138, -62.55) * mm, "end": v(-138, -60.05) * mm});
            skLineSegment(sketch, "E2069", {"start": v(-138, 62.55) * mm, "end": v(-138, 60.05) * mm});
            skLineSegment(sketch, "E2070", {"start": v(144, -94.05) * mm, "end": v(144, -162.15) * mm});
            skLineSegment(sketch, "E2071", {"start": v(-108, 231.15) * mm, "end": v(-108, 228.15) * mm});
            skLineSegment(sketch, "E2072", {"start": v(102.5, 228.15) * mm, "end": v(102.5, 226.15) * mm});
            skLineSegment(sketch, "E2073", {"start": v(105.5, 237.15) * mm, "end": v(105.5, 231.15) * mm});
            skLineSegment(sketch, "E2074", {"start": v(102.5, 237.15) * mm, "end": v(102.5, 231.15) * mm});
            skLineSegment(sketch, "E2075", {"start": v(105.5, 228.15) * mm, "end": v(105.5, 226.15) * mm});
            skLineSegment(sketch, "E2076", {"start": v(-135, 62.55) * mm, "end": v(-133, 62.55) * mm});
            skLineSegment(sketch, "E2077", {"start": v(-133, 65.55) * mm, "end": v(-133, 62.55) * mm});
            skLineSegment(sketch, "E2078", {"start": v(-135, 65.55) * mm, "end": v(-133, 65.55) * mm});
            skLineSegment(sketch, "E2079", {"start": v(-138, 65.55) * mm, "end": v(-138, 68.05) * mm});
            skLineSegment(sketch, "E2080", {"start": v(138, -62.55) * mm, "end": v(138, -60.05) * mm});
            skLineSegment(sketch, "E2081", {"start": v(138, -60.05) * mm, "end": v(135, -60.05) * mm});
            skLineSegment(sketch, "E2082", {"start": v(135, -62.55) * mm, "end": v(135, -60.05) * mm});
            skLineSegment(sketch, "E2083", {"start": v(135, -62.55) * mm, "end": v(133, -62.55) * mm});
            skLineSegment(sketch, "E2084", {"start": v(133, -65.55) * mm, "end": v(133, -62.55) * mm});
            skLineSegment(sketch, "E2085", {"start": v(135, -65.55) * mm, "end": v(133, -65.55) * mm});
            skLineSegment(sketch, "E2086", {"start": v(135, -65.55) * mm, "end": v(135, -68.05) * mm});
            skLineSegment(sketch, "E2087", {"start": v(138, -68.05) * mm, "end": v(135, -68.05) * mm});
            skLineSegment(sketch, "E2088", {"start": v(138, -65.55) * mm, "end": v(138, -68.05) * mm});
            skLineSegment(sketch, "E2089", {"start": v(138, 196.15) * mm, "end": v(135, 196.15) * mm});
            skLineSegment(sketch, "E2090", {"start": v(150, 222.15) * mm, "end": v(150, 212.15) * mm});
            skLineSegment(sketch, "E2091", {"start": v(138, 190.65) * mm, "end": v(138, 188.15) * mm});
            skLineSegment(sketch, "E2092", {"start": v(135, 193.65) * mm, "end": v(133, 193.65) * mm});
            skLineSegment(sketch, "E2093", {"start": v(144, 193.65) * mm, "end": v(138, 193.65) * mm});
            skLineSegment(sketch, "E2094", {"start": v(144, 212.15) * mm, "end": v(150, 212.15) * mm});
            skLineSegment(sketch, "E2095", {"start": v(150, 172.15) * mm, "end": v(150, 162.15) * mm});
            skLineSegment(sketch, "E2096", {"start": v(-138, 196.15) * mm, "end": v(-135, 196.15) * mm});
            skLineSegment(sketch, "E2097", {"start": v(-144, 193.65) * mm, "end": v(-144, 212.15) * mm});
            skLineSegment(sketch, "E2098", {"start": v(-144, 172.15) * mm, "end": v(-144, 190.65) * mm});
            skLineSegment(sketch, "E2099", {"start": v(138, -193.65) * mm, "end": v(138, -196.15) * mm});
            skLineSegment(sketch, "E2100", {"start": v(135, -193.65) * mm, "end": v(133, -193.65) * mm});
            skLineSegment(sketch, "E2101", {"start": v(150, -162.15) * mm, "end": v(150, -172.15) * mm});
            skLineSegment(sketch, "E2102", {"start": v(144, -172.15) * mm, "end": v(150, -172.15) * mm});
            skLineSegment(sketch, "E2103", {"start": v(144, -212.15) * mm, "end": v(150, -212.15) * mm});
            skCircle(sketch, "E2104", {"center": v(99, -26.02) * mm, "radius": 1.5 * mm});
            skLineSegment(sketch, "E2105", {"start": v(-144, -237.15) * mm, "end": v(-144, -222.15) * mm});
            skLineSegment(sketch, "E2106", {"start": v(74, 243.15) * mm, "end": v(84, 243.15) * mm});
            skLineSegment(sketch, "E2107", {"start": v(117.5, 181.96) * mm, "end": v(117.5, 211.96) * mm});
            skCircle(sketch, "E2108", {"center": v(130, -57.02) * mm, "radius": 1.5 * mm});
            skArc(sketch, "E2109", {"start": v(102.86, -196.33) * mm, "mid": v(111.14, -180.13) * mm, "end": v(114, -162.15) * mm});
            skLineSegment(sketch, "E2110", {"start": v(113, -5.9) * mm, "end": v(116, -5.9) * mm});
            skArc(sketch, "E2111", {"start": v(89.94, -196.1) * mm, "mid": v(100.35, -180.52) * mm, "end": v(104, -162.15) * mm});
            skCircle(sketch, "E2112", {"center": v(-130, -26.02) * mm, "radius": 1.5 * mm});
            skArc(sketch, "E2113", {"start": v(108, -162.15) * mm, "mid": v(106, -160.15) * mm, "end": v(104, -162.15) * mm});
            skArc(sketch, "E2114", {"start": v(92.77, -198.92) * mm, "mid": v(104.04, -182.05) * mm, "end": v(108, -162.15) * mm});
            skArc(sketch, "E2115", {"start": v(89.94, -196.1) * mm, "mid": v(89.94, -198.92) * mm, "end": v(92.77, -198.92) * mm});
            skCircle(sketch, "E2116", {"center": v(130, -26.02) * mm, "radius": 1.5 * mm});
            skLineSegment(sketch, "E2117", {"start": v(-150, 34.05) * mm, "end": v(-150, 44.05) * mm});
            skLineSegment(sketch, "E2118", {"start": v(-144, 44.05) * mm, "end": v(-144, 62.55) * mm});
            skLineSegment(sketch, "E2119", {"start": v(105.5, 237.15) * mm, "end": v(124, 237.15) * mm});
            skLineSegment(sketch, "E2120", {"start": v(74, 237.15) * mm, "end": v(74, 243.15) * mm});
            skLineSegment(sketch, "E2121", {"start": v(-102.5, 237.15) * mm, "end": v(-84, 237.15) * mm});
            skLineSegment(sketch, "E2122", {"start": v(20, 237.15) * mm, "end": v(1.5, 237.15) * mm});
            skLineSegment(sketch, "E2123", {"start": v(-74, 237.15) * mm, "end": v(-30, 237.15) * mm});
            skLineSegment(sketch, "E2124", {"start": v(-84, 243.15) * mm, "end": v(-74, 243.15) * mm});
            skLineSegment(sketch, "E2125", {"start": v(-74, 237.15) * mm, "end": v(-74, 243.15) * mm});
            skLineSegment(sketch, "E2126", {"start": v(-84, 237.15) * mm, "end": v(-84, 243.15) * mm});
            skLineSegment(sketch, "E2127", {"start": v(-105.5, -237.15) * mm, "end": v(-124, -237.15) * mm});
            skLineSegment(sketch, "E2128", {"start": v(124, 243.15) * mm, "end": v(134, 243.15) * mm});
            skLineSegment(sketch, "E2129", {"start": v(135, -190.65) * mm, "end": v(133, -190.65) * mm});
            skLineSegment(sketch, "E2130", {"start": v(138, -190.65) * mm, "end": v(138, -188.15) * mm});
            skLineSegment(sketch, "E2131", {"start": v(144, -193.65) * mm, "end": v(138, -193.65) * mm});
            skLineSegment(sketch, "E2132", {"start": v(-135, 190.65) * mm, "end": v(-135, 188.15) * mm});
            skLineSegment(sketch, "E2133", {"start": v(-135, 190.65) * mm, "end": v(-133, 190.65) * mm});
            skLineSegment(sketch, "E2134", {"start": v(-150, 212.15) * mm, "end": v(-150, 222.15) * mm});
            skLineSegment(sketch, "E2135", {"start": v(-20, 237.15) * mm, "end": v(-20, 243.15) * mm});
            skLineSegment(sketch, "E2136", {"start": v(-30, 243.15) * mm, "end": v(-20, 243.15) * mm});
            skLineSegment(sketch, "E2137", {"start": v(-30, 237.15) * mm, "end": v(-30, 243.15) * mm});
            skLineSegment(sketch, "E2138", {"start": v(105.5, 228.15) * mm, "end": v(108, 228.15) * mm});
            skLineSegment(sketch, "E2139", {"start": v(105.5, 231.15) * mm, "end": v(108, 231.15) * mm});
            skLineSegment(sketch, "E2140", {"start": v(20, 237.15) * mm, "end": v(20, 243.15) * mm});
            skLineSegment(sketch, "E2141", {"start": v(20, 243.15) * mm, "end": v(30, 243.15) * mm});
            skLineSegment(sketch, "E2142", {"start": v(30, 237.15) * mm, "end": v(30, 243.15) * mm});
            skLineSegment(sketch, "E2143", {"start": v(30, 237.15) * mm, "end": v(74, 237.15) * mm});
            skArc(sketch, "E2144", {"start": v(102.86, -196.33) * mm, "mid": v(103.31, -199.13) * mm, "end": v(106.1, -198.67) * mm});
            skCircle(sketch, "E2145", {"center": v(111, -152.15) * mm, "radius": 1.5 * mm});
            skCircle(sketch, "E2146", {"center": v(-5.5, 143.15) * mm, "radius": 2 * mm});
            skLineSegment(sketch, "E2147", {"start": v(150, -162.15) * mm, "end": v(144, -162.15) * mm});
            skLineSegment(sketch, "E2148", {"start": v(117.5, 181.96) * mm, "end": v(129.5, 181.96) * mm});
            skLineSegment(sketch, "E2149", {"start": v(116, -5.9) * mm, "end": v(116, -30.7) * mm});
            skArc(sketch, "E2150", {"start": v(112.99, -30.61) * mm, "mid": v(114.5, -52.5) * mm, "end": v(116.01, -30.61) * mm});
            skCircle(sketch, "E2151", {"center": v(5.5, 143.15) * mm, "radius": 2 * mm});
            skArc(sketch, "E2152", {"start": v(-118, -162.15) * mm, "mid": v(-114.95, -181.35) * mm, "end": v(-106.1, -198.67) * mm});
            skCircle(sketch, "E2153", {"center": v(-94.34, -202.48) * mm, "radius": 1.5 * mm});
            skCircle(sketch, "E2154", {"center": v(-111, -152.15) * mm, "radius": 1.5 * mm});
            skArc(sketch, "E2155", {"start": v(-114, -162.15) * mm, "mid": v(-111.14, -180.13) * mm, "end": v(-102.86, -196.33) * mm});
            skCircle(sketch, "E2156", {"center": v(-87.61, -208.48) * mm, "radius": 1.5 * mm});
            skArc(sketch, "E2157", {"start": v(-106.1, -198.67) * mm, "mid": v(-103.31, -199.13) * mm, "end": v(-102.86, -196.33) * mm});
            skLineSegment(sketch, "E2158", {"start": v(113, -30.7) * mm, "end": v(113, -5.9) * mm});
            skArc(sketch, "E2159", {"start": v(-114, -162.15) * mm, "mid": v(-116, -160.15) * mm, "end": v(-118, -162.15) * mm});
            skPoint(sketch, "E2160.0", {"position": v(-30, 243.15) * mm});
            skSolve(sketch);
        }
        {
            var Q0;
            Q0 = qSketchRegion(id + "F16", true);
            extrude(context, id + "F17", {"entities" : qUnion([Q0]), "depth" : 6 * mm, "offsetDistance" : 25 * mm});
        }
    });
